FCSTD DOCUMENT  (FreeCAD 0.16R6700 (Git))
Label: fuselage_simple2
License: All rights reserved
LicenseURL: http://en.wikipedia.org/wiki/All_rights_reserved
objects: Sketcher::SketchObject×101, PartDesign::Pocket×53, PartDesign::Fillet×46, PartDesign::Pad×29, Part::Extrusion×14, Part::Mirroring×8, Part::MultiFuse×6, PartDesign::Groove×5, Part::FeaturePython×5, Part::Cut×3, Mesh::Feature×2, Part::Part2DObjectPython×2, Part::MultiCommon×2, Part::Sweep×1, Part::Cylinder×1
note: 363 computed .brp shape members not serialized (recipe doc carries the construction recipe); baked Part::Feature solids carry a one-line shape summary decoded from their .brp

FEATURE [Mesh::Feature] cam_holder  label="cam+holder"
  Placement = pos=(-6.5,10.5,19) rot=(1,0,0;0.785398rad)
FEATURE [Sketcher::SketchObject] Sketch
  Placement = pos=(0,3,20) rot=(0.57735,0.57735,0.57735;2.0944rad)
  sketch-geometry (7):
    g0: Circle CenterX=0 CenterY=0 CenterZ=0 NormalX=0 NormalY=0 NormalZ=1 Radius=1.7
    g1: LineSegment StartX=-3.5 StartY=3 StartZ=0 EndX=1 EndY=3 EndZ=0
    g2: LineSegment StartX=3 StartY=1 StartZ=0 EndX=3 EndY=-1 EndZ=0
    g3: LineSegment StartX=1 StartY=-3 StartZ=0 EndX=-3.5 EndY=-3 EndZ=0
    g4: LineSegment StartX=-3.5 StartY=-3 StartZ=0 EndX=-3.5 EndY=3 EndZ=0
    g5: ArcOfCircle CenterX=1 CenterY=1 CenterZ=0 NormalX=0 NormalY=0 NormalZ=1 Radius=2 StartAngle=0 EndAngle=1.5708
    g6: ArcOfCircle CenterX=1 CenterY=-1 CenterZ=0 NormalX=0 NormalY=0 NormalZ=1 Radius=2 StartAngle=4.71239 EndAngle=6.28319
  constraints (18):
    c: Coincident(g0,g-1)
    c: Radius(g0) = 1.7
    c: Coincident(g3,g4)
    c: Coincident(g4,g1)
    c: Horizontal(g1)
    c: Horizontal(g3)
    c: Vertical(g2)
    c: Vertical(g4)
    c: Tangent(g1,g5) = 1.5708
    c: Tangent(g2,g5) = 1.5708
    c: Tangent(g2,g6) = 1.5708
    c: Tangent(g3,g6) = 1.5708
    c: Radius(g5) = 2
    c: Radius(g6) = 2
    c: Symmetric(g1,g3,g-1)
    c: DistanceX(g-1,g2) = 3
    c: DistanceY(g-1,g1) = 3
    c: DistanceX(g1,g-1) = 3.5
FEATURE [PartDesign::Pad] Pad
  Length = 3
  Length2 = 100
  Midplane = true
  Placement = pos=(0,3,20) rot=(0.57735,0.57735,0.57735;2.0944rad)
  Sketch = -> Sketch
  Type = 0
FEATURE [Sketcher::SketchObject] Sketch001
  Placement = pos=(0,0,0) rot=(1,0,0;1.5708rad)
  sketch-geometry (16):
    g0: LineSegment StartX=-10 StartY=40 StartZ=0 EndX=10 EndY=40 EndZ=0
    g1: LineSegment StartX=30 StartY=20 StartZ=0 EndX=30 EndY=-20 EndZ=0
    g2: LineSegment StartX=10 StartY=-40 StartZ=0 EndX=-10 EndY=-40 EndZ=0
    g3: LineSegment StartX=-30 StartY=-20 StartZ=0 EndX=-30 EndY=20 EndZ=0
    g4: ArcOfCircle CenterX=-10 CenterY=20 CenterZ=0 NormalX=0 NormalY=0 NormalZ=1 Radius=20 StartAngle=1.5708 EndAngle=3.14159
    g5: ArcOfCircle CenterX=10 CenterY=20 CenterZ=0 NormalX=0 NormalY=0 NormalZ=1 Radius=20 StartAngle=0 EndAngle=1.5708
    g6: ArcOfCircle CenterX=10 CenterY=-20 CenterZ=0 NormalX=0 NormalY=0 NormalZ=1 Radius=20 StartAngle=4.71239 EndAngle=6.28319
    g7: ArcOfCircle CenterX=-10 CenterY=-20 CenterZ=0 NormalX=0 NormalY=0 NormalZ=1 Radius=20 StartAngle=3.14159 EndAngle=4.71239
    g8: LineSegment StartX=-10 StartY=37 StartZ=0 EndX=10 EndY=37 EndZ=0
    g9: LineSegment StartX=27 StartY=20 StartZ=0 EndX=27 EndY=-20 EndZ=0
    g10: LineSegment StartX=10 StartY=-37 StartZ=0 EndX=-10 EndY=-37 EndZ=0
    g11: LineSegment StartX=-27 StartY=-20 StartZ=0 EndX=-27 EndY=20 EndZ=0
    g12: ArcOfCircle CenterX=-10 CenterY=20 CenterZ=0 NormalX=0 NormalY=0 NormalZ=1 Radius=17 StartAngle=1.5708 EndAngle=3.14159
    g13: ArcOfCircle CenterX=10 CenterY=20 CenterZ=0 NormalX=0 NormalY=0 NormalZ=1 Radius=17 StartAngle=0 EndAngle=1.5708
    g14: ArcOfCircle CenterX=10 CenterY=-20 CenterZ=0 NormalX=0 NormalY=0 NormalZ=1 Radius=17 StartAngle=4.71239 EndAngle=6.28319
    g15: ArcOfCircle CenterX=-10 CenterY=-20 CenterZ=0 NormalX=0 NormalY=0 NormalZ=1 Radius=17 StartAngle=3.14159 EndAngle=4.71239
  constraints (38):
    c: Horizontal(g0)
    c: Horizontal(g2)
    c: Vertical(g1)
    c: Tangent(g0,g4) = 1.5708
    c: Tangent(g3,g4) = 1.5708
    c: Tangent(g0,g5) = 1.5708
    c: Tangent(g1,g5) = 1.5708
    c: Tangent(g1,g6) = 1.5708
    c: Tangent(g2,g6) = 1.5708
    c: Tangent(g2,g7) = 1.5708
    c: Tangent(g3,g7) = 1.5708
    c: Radius(g4) = 20
    c: DistanceX(g3,g1) = 60
    c: Equal(g4,g5)
    c: Equal(g6,g4)
    c: Equal(g7,g4)
    c: DistanceY(g2,g0) = 80
    c: Horizontal(g8)
    c: Horizontal(g10)
    c: Vertical(g9)
    c: Tangent(g8,g12) = 1.5708
    c: Tangent(g11,g12) = 1.5708
    c: Tangent(g8,g13) = 1.5708
    c: Tangent(g9,g13) = 1.5708
    c: Tangent(g9,g14) = 1.5708
    c: Tangent(g10,g14) = 1.5708
    c: Tangent(g10,g15) = 1.5708
    c: Tangent(g11,g15) = 1.5708
    c: DistanceX(g11,g9) = 54
    c: DistanceY(g10,g8) = 74
    c: Radius(g12) = 17
    c: Equal(g12,g13)
    c: Equal(g15,g12)
    c: Equal(g14,g12)
    c: Symmetric(g1,g3,g-2)
    c: Symmetric(g11,g9,g-2)
    c: Symmetric(g8,g10,g-1)
    c: Symmetric(g0,g2,g-1)
FEATURE [Part::Extrusion] Extrude
  Base = -> Sketch001
  Dir = (0,120,0)
  Solid = true
FEATURE [Sketcher::SketchObject] Sketch002
  ExternalGeometry = -> [Extrude]
  Placement = pos=(0,0,0) rot=(1,0,0;1.5708rad)
  Support = -> Extrude [Face17]
  sketch-geometry (8):
    g0: ArcOfCircle CenterX=-10 CenterY=20 CenterZ=0 NormalX=0 NormalY=0 NormalZ=1 Radius=20 StartAngle=1.5708 EndAngle=3.14159
    g1: ArcOfCircle CenterX=10 CenterY=20 CenterZ=0 NormalX=0 NormalY=0 NormalZ=1 Radius=20 StartAngle=1.97396e-06 EndAngle=1.5708
    g2: ArcOfCircle CenterX=10 CenterY=-20 CenterZ=0 NormalX=0 NormalY=0 NormalZ=1 Radius=20 StartAngle=4.71239 EndAngle=6.28319
    g3: ArcOfCircle CenterX=-10 CenterY=-20 CenterZ=0 NormalX=0 NormalY=0 NormalZ=1 Radius=20 StartAngle=3.14159 EndAngle=4.71239
    g4: LineSegment StartX=-30 StartY=20 StartZ=0 EndX=-30 EndY=-20 EndZ=0
    g5: LineSegment StartX=-10 StartY=40 StartZ=0 EndX=10 EndY=40 EndZ=0
    g6: LineSegment StartX=30 StartY=20 StartZ=0 EndX=30 EndY=-20 EndZ=0
    g7: LineSegment StartX=10 StartY=-40 StartZ=0 EndX=-10 EndY=-40 EndZ=0
  constraints (20):
    c: Coincident(g0,g-3)
    c: Coincident(g1,g-4)
    c: Coincident(g3,g-6)
    c: Coincident(g2,g-5)
    c: Coincident(g2,g-5)
    c: Coincident(g2,g7)
    c: Coincident(g3,g7)
    c: Coincident(g3,g-6)
    c: Coincident(g3,g4)
    c: Coincident(g0,g4)
    c: Coincident(g0,g-3)
    c: Coincident(g5,g0)
    c: Coincident(g1,g5)
    c: Coincident(g1,g-4)
    c: Coincident(g1,g6)
    c: Coincident(g6,g2)
    c: Vertical(g6)
    c: Horizontal(g7)
    c: Vertical(g4)
    c: Horizontal(g5)
FEATURE [PartDesign::Pad] Pad001
  Length = 3
  Length2 = 100
  Sketch = -> Sketch002
  Type = 0
FEATURE [Part::Part2DObjectPython] Clone2D  label="Clone of Sketch002 (2D)"  # Draft 2D object (typed FeaturePython)
  Objects = -> [Sketch002]
  Placement = pos=(0,120,0) rot=(1,0,0;1.5708rad)
  Scale = (1,1,1)
FEATURE [PartDesign::Pad] Pad002
  Length = 3
  Length2 = 100
  Placement = pos=(0,120,0) rot=(1,0,0;1.5708rad)
  Reversed = true
  Sketch = -> Clone2D
  Type = 0
FEATURE [PartDesign::Fillet] Fillet
  Base = -> Pad001 [Edge49,Edge47,Edge46,Edge43,Edge42,Edge39,Edge38,Edge35]
  Radius = 17
FEATURE [PartDesign::Fillet] Fillet001
  Base = -> Fillet [Edge70,Edge68,Edge65,Edge79,Edge78,Edge75,Edge74,Edge71]
  Radius = 20
FEATURE [Sketcher::SketchObject] Sketch003
  Placement = pos=(0,-3,0) rot=(1,0,0;1.5708rad)
  Support = -> Fillet001 [Face9]
  sketch-geometry (4):
    g0: ArcOfCircle CenterX=0 CenterY=35 CenterZ=0 NormalX=0 NormalY=0 NormalZ=1 Radius=10 StartAngle=3.70592 EndAngle=5.71885
    g1: LineSegment StartX=-8.44947 StartY=29.6515 StartZ=0 EndX=-15 EndY=40 EndZ=0
    g2: LineSegment StartX=8.44947 StartY=29.6515 StartZ=0 EndX=15 EndY=40 EndZ=0
    g3: LineSegment StartX=-15 StartY=40 StartZ=0 EndX=15 EndY=40 EndZ=0
  constraints (13):
    c: PointOnObject(g0,g-2)
    c: Coincident(g1,g0)
    c: Coincident(g2,g0)
    c: Tangent(g1,g0)
    c: Tangent(g0,g2)
    c: Coincident(g3,g1)
    c: Coincident(g3,g2)
    c: Horizontal(g3)
    c: Symmetric(g2,g1,g-2)
    c: DistanceY(g-1,g2) = 40
    c: DistanceY(g-1,g0) = 35
    c: Radius(g0) = 10
    c: Distance(g3) = 30
FEATURE [PartDesign::Pocket] Pocket
  Length = 10
  Sketch = -> Sketch003
  Type = 0
FEATURE [Sketcher::SketchObject] Sketch004
  ExternalGeometry = -> [Pocket]
  Placement = pos=(0,7,0) rot=(1,0,0;1.5708rad)
  Support = -> Pocket [Face24]
  sketch-geometry (4):
    g0: LineSegment StartX=11.0184 StartY=33.71 StartZ=0 EndX=15.8321 EndY=41.3145 EndZ=0
    g1: LineSegment StartX=15.8321 StartY=41.3145 StartZ=0 EndX=0 EndY=41.3145 EndZ=0
    g2: LineSegment StartX=0 StartY=41.3145 StartZ=0 EndX=0 EndY=33.71 EndZ=0
    g3: LineSegment StartX=11.0184 StartY=33.71 StartZ=0 EndX=0 EndY=33.71 EndZ=0
  constraints (11):
    c: Coincident(g0,g-3)
    c: PointOnObject(g-3,g0)
    c: Distance(g0) = 9
    c: Coincident(g0,g1)
    c: PointOnObject(g1,g-2)
    c: Horizontal(g1)
    c: Horizontal(g3)
    c: Coincident(g2,g3)
    c: Coincident(g1,g2)
    c: Vertical(g2)
    c: Coincident(g0,g3)
FEATURE [PartDesign::Groove] Groove
  Angle = 360
  Axis = (0,0,1)
  Base = (0,7,0)
  ReferenceAxis = -> Sketch004 [V_Axis]
  Sketch = -> Sketch004
FEATURE [Sketcher::SketchObject] Sketch009
  Placement = pos=(15,32.5,-9) rot=(0,0.707107,-0.707107;3.14159rad)
  sketch-geometry (8):
    g0: LineSegment StartX=0 StartY=0 StartZ=0 EndX=20 EndY=0 EndZ=0
    g1: LineSegment StartX=20 StartY=0 StartZ=0 EndX=20 EndY=-26 EndZ=0
    g2: LineSegment StartX=10 StartY=-26 StartZ=0 EndX=0 EndY=-26 EndZ=0
    g3: LineSegment StartX=0 StartY=-26 StartZ=0 EndX=0 EndY=0 EndZ=0
    g4: LineSegment StartX=20 StartY=-26 StartZ=0 EndX=20 EndY=-41 EndZ=0
    g5: LineSegment StartX=20 StartY=-41 StartZ=0 EndX=10 EndY=-41 EndZ=0
    g6: LineSegment StartX=10 StartY=-41 StartZ=0 EndX=10 EndY=-26 EndZ=0
    g7: LineSegment [constr] StartX=10 StartY=-26 StartZ=0 EndX=20 EndY=-26 EndZ=0
  constraints (22):
    c: Coincident(g0,g1)
    c: Coincident(g2,g3)
    c: Coincident(g3,g0)
    c: Horizontal(g0)
    c: Horizontal(g2)
    c: Vertical(g1)
    c: Vertical(g3)
    c: Distance(g0) = 20
    c: DistanceY(g1,g1) = 26
    c: Coincident(g4,g1)
    c: Vertical(g4)
    c: DistanceY(g4,g4) = 15
    c: Coincident(g5,g4)
    c: Horizontal(g5)
    c: Distance(g5) = 10
    c: Coincident(g6,g5)
    c: Vertical(g6)
    c: Coincident(g2,g6)
    c: Coincident(g7,g2)
    c: Coincident(g7,g1)
    c: Horizontal(g7)
    c: Coincident(g0,g-1)
FEATURE [PartDesign::Pad] Pad003  label="video_tx_base"
  Length = 6
  Length2 = 100
  Placement = pos=(15,32.5,-9) rot=(0,0.707107,-0.707107;3.14159rad)
  Sketch = -> Sketch009
  Type = 0
FEATURE [Sketcher::SketchObject] Sketch010
  ExternalGeometry = -> [Pad003]
  Placement = pos=(15,26.5,-9) rot=(0,0.707107,-0.707107;3.14159rad)
  Support = -> Pad003 [Face9]
  sketch-geometry (8):
    g0: LineSegment StartX=0.5 StartY=-3 StartZ=0 EndX=19.5 EndY=-3 EndZ=0
    g1: LineSegment StartX=19.5 StartY=-3 StartZ=0 EndX=19.5 EndY=-23 EndZ=0
    g2: LineSegment StartX=19.5 StartY=-23 StartZ=0 EndX=0.5 EndY=-23 EndZ=0
    g3: LineSegment StartX=0.5 StartY=-23 StartZ=0 EndX=0.5 EndY=-3 EndZ=0
    g4: LineSegment StartX=10 StartY=-26 StartZ=0 EndX=20 EndY=-26 EndZ=0
    g5: LineSegment StartX=20 StartY=-26 StartZ=0 EndX=20 EndY=-41 EndZ=0
    g6: LineSegment StartX=20 StartY=-41 StartZ=0 EndX=10 EndY=-41 EndZ=0
    g7: LineSegment StartX=10 StartY=-26 StartZ=0 EndX=10 EndY=-41 EndZ=0
  constraints (21):
    c: Coincident(g0,g1)
    c: Coincident(g1,g2)
    c: Coincident(g2,g3)
    c: Coincident(g3,g0)
    c: Horizontal(g0)
    c: Horizontal(g2)
    c: Vertical(g1)
    c: Vertical(g3)
    c: Coincident(g4,g5)
    c: Coincident(g5,g6)
    c: Horizontal(g4)
    c: Horizontal(g6)
    c: Vertical(g5)
    c: Coincident(g4,g-3)
    c: Coincident(g5,g-4)
    c: Distance(g2) = 19
    c: Distance(g1) = 20
    c: DistanceX(g-1,g0) = 0.5
    c: DistanceY(g0,g-1) = 3
    c: Coincident(g7,g4)
    c: Coincident(g7,g6)
FEATURE [PartDesign::Pad] Pad004  label="video_tx"
  Length = 3
  Length2 = 100
  Placement = pos=(15,32.5,-9) rot=(0,0.707107,-0.707107;3.14159rad)
  Sketch = -> Sketch010
  Type = 0
FEATURE [Sketcher::SketchObject] Sketch011
  Placement = pos=(0,0,40) rot=(0,0,1;0rad)
  Support = -> Groove [Face10]
  sketch-geometry (1):
    g0: Circle CenterX=0 CenterY=28 CenterZ=0 NormalX=0 NormalY=0 NormalZ=1 Radius=5
  constraints (3):
    c: PointOnObject(g0,g-2)
    c: Radius(g0) = 5
    c: DistanceY(g-1,g0) = 28
FEATURE [PartDesign::Pocket] Pocket001
  Length = 5
  Sketch = -> Sketch011
  Type = 0
FEATURE [Sketcher::SketchObject] Sketch012
  ExternalGeometry = -> [Groove]
  Placement = pos=(27,0,0) rot=(0.57735,-0.57735,-0.57735;2.0944rad)
  Support = -> Groove [Face18]
  sketch-geometry (4):
    g0: LineSegment StartX=-29 StartY=16.5 StartZ=0 EndX=-25 EndY=16.5 EndZ=0
    g1: LineSegment StartX=-25 StartY=16.5 StartZ=0 EndX=-25 EndY=-11.5 EndZ=0
    g2: LineSegment StartX=-25 StartY=-11.5 StartZ=0 EndX=-29 EndY=-11.5 EndZ=0
    g3: LineSegment StartX=-29 StartY=-11.5 StartZ=0 EndX=-29 EndY=16.5 EndZ=0
  constraints (12):
    c: Coincident(g0,g1)
    c: Coincident(g1,g2)
    c: Coincident(g2,g3)
    c: Coincident(g3,g0)
    c: Horizontal(g0)
    c: Horizontal(g2)
    c: Vertical(g1)
    c: Vertical(g3)
    c: Distance(g2) = 4
    c: Distance(g1) = 28
    c: DistanceY(g0,g-3) = 3.5
    c: DistanceX(g0,g-3) = 8
FEATURE [PartDesign::Pad] Pad005
  Length = 55
  Length2 = 100
  Sketch = -> Sketch012
  Type = 0
FEATURE [Sketcher::SketchObject] Sketch013
  Placement = pos=(0,25,0) rot=(1,0,0;1.5708rad)
  Support = -> Pad005 [Face32]
  sketch-geometry (4):
    g0: LineSegment StartX=-4.75 StartY=14.25 StartZ=0 EndX=14.75 EndY=14.25 EndZ=0
    g1: LineSegment StartX=14.75 StartY=14.25 StartZ=0 EndX=14.75 EndY=-6.25 EndZ=0
    g2: LineSegment StartX=14.75 StartY=-6.25 StartZ=0 EndX=-4.75 EndY=-6.25 EndZ=0
    g3: LineSegment StartX=-4.75 StartY=-6.25 StartZ=0 EndX=-4.75 EndY=14.25 EndZ=0
  constraints (12):
    c: Coincident(g0,g1)
    c: Coincident(g1,g2)
    c: Coincident(g2,g3)
    c: Coincident(g3,g0)
    c: Horizontal(g0)
    c: Horizontal(g2)
    c: Vertical(g1)
    c: Vertical(g3)
    c: Distance(g0) = 19.5
    c: Distance(g1) = 20.5
    c: DistanceY(g2,g-1) = 6.25
    c: DistanceX(g2,g-1) = 4.75
FEATURE [PartDesign::Pocket] Pocket002
  Length = 5
  Sketch = -> Sketch013
  Type = 0
FEATURE [Sketcher::SketchObject] Sketch014
  Placement = pos=(0,29,0) rot=(0,0.707107,0.707107;3.14159rad)
  Support = -> Pocket002 [Face30]
  sketch-geometry (4):
    g0: LineSegment StartX=-15.25 StartY=17.25 StartZ=0 EndX=5.25 EndY=17.25 EndZ=0
    g1: LineSegment StartX=5.25 StartY=17.25 StartZ=0 EndX=5.25 EndY=-9.25 EndZ=0
    g2: LineSegment StartX=5.25 StartY=-9.25 StartZ=0 EndX=-15.25 EndY=-9.25 EndZ=0
    g3: LineSegment StartX=-15.25 StartY=-9.25 StartZ=0 EndX=-15.25 EndY=17.25 EndZ=0
  constraints (12):
    c: Coincident(g0,g1)
    c: Coincident(g1,g2)
    c: Coincident(g2,g3)
    c: Coincident(g3,g0)
    c: Horizontal(g0)
    c: Horizontal(g2)
    c: Vertical(g1)
    c: Vertical(g3)
    c: Distance(g2) = 20.5
    c: DistanceY(g3,g3) = 26.5
    c: DistanceY(g1,g-1) = 9.25
    c: DistanceX(g-1,g1) = 5.25
FEATURE [PartDesign::Pocket] Pocket003
  Length = 2
  Sketch = -> Sketch014
  Type = 0
FEATURE [Sketcher::SketchObject] Sketch015
  Placement = pos=(0,0,40) rot=(0,0,1;0rad)
  Support = -> Pocket003 [Face10]
  sketch-geometry (1):
    g0: Circle CenterX=0 CenterY=28 CenterZ=0 NormalX=0 NormalY=0 NormalZ=1 Radius=5
  constraints (3):
    c: Radius(g0) = 5
    c: DistanceY(g-1,g0) = 28
    c: PointOnObject(g0,g-2)
FEATURE [PartDesign::Pocket] Pocket004
  Length = 5
  Sketch = -> Sketch015
  Type = 0
FEATURE [Sketcher::SketchObject] Sketch016
  Placement = pos=(-17.5,40,5) rot=(0,0,1;0rad)
  sketch-geometry (4):
    g0: LineSegment StartX=0 StartY=80 StartZ=0 EndX=35 EndY=80 EndZ=0
    g1: LineSegment StartX=35 StartY=80 StartZ=0 EndX=35 EndY=0 EndZ=0
    g2: LineSegment StartX=35 StartY=0 StartZ=0 EndX=0 EndY=0 EndZ=0
    g3: LineSegment StartX=0 StartY=0 StartZ=0 EndX=0 EndY=80 EndZ=0
  constraints (11):
    c: Coincident(g0,g1)
    c: Coincident(g1,g2)
    c: Coincident(g2,g3)
    c: Coincident(g3,g0)
    c: Horizontal(g0)
    c: Horizontal(g2)
    c: Vertical(g1)
    c: Vertical(g3)
    c: Coincident(g2,g-1)
    c: Distance(g3) = 80
    c: Distance(g2) = 35
FEATURE [PartDesign::Pad] Pad006  label="battery"
  Length = 27
  Length2 = 100
  Placement = pos=(-17.5,40,5) rot=(0,0,1;0rad)
  Sketch = -> Sketch016
  Type = 0
FEATURE [Sketcher::SketchObject] Sketch017
  Placement = pos=(27,0,0) rot=(0.57735,-0.57735,-0.57735;2.0944rad)
  Support = -> Pocket004 [Face18]
  sketch-geometry (4):
    g0: LineSegment StartX=-39 StartY=30 StartZ=0 EndX=-34 EndY=30 EndZ=0
    g1: LineSegment StartX=-34 StartY=30 StartZ=0 EndX=-34 EndY=-10 EndZ=0
    g2: LineSegment StartX=-34 StartY=-10 StartZ=0 EndX=-39 EndY=-10 EndZ=0
    g3: LineSegment StartX=-39 StartY=-10 StartZ=0 EndX=-39 EndY=30 EndZ=0
  constraints (12):
    c: Coincident(g0,g1)
    c: Coincident(g1,g2)
    c: Coincident(g2,g3)
    c: Coincident(g3,g0)
    c: Horizontal(g0)
    c: Horizontal(g2)
    c: Vertical(g1)
    c: Vertical(g3)
    c: Distance(g2) = 5
    c: DistanceX(g0,g-1) = 34
    c: DistanceY(g1,g1) = 40
    c: DistanceY(g1,g-1) = 10
FEATURE [PartDesign::Pad] Pad007
  Length = 54
  Length2 = 100
  Sketch = -> Sketch017
  Type = 0
FEATURE [PartDesign::Fillet] Fillet002
  Base = -> Pad007 [Edge73,Edge79,Edge54,Edge64]
  Radius = 4
FEATURE [Sketcher::SketchObject] Sketch018
  Placement = pos=(0,39,0) rot=(0,0.707107,0.707107;3.14159rad)
  Support = -> Fillet002 [Face17]
  sketch-geometry (4):
    g0: LineSegment StartX=-27.5 StartY=4 StartZ=0 EndX=27.5 EndY=4 EndZ=0
    g1: LineSegment StartX=27.5 StartY=4 StartZ=0 EndX=27.5 EndY=0 EndZ=0
    g2: LineSegment StartX=27.5 StartY=0 StartZ=0 EndX=-27.5 EndY=0 EndZ=0
    g3: LineSegment StartX=-27.5 StartY=0 StartZ=0 EndX=-27.5 EndY=4 EndZ=0
  constraints (12):
    c: Coincident(g0,g1)
    c: Coincident(g1,g2)
    c: Coincident(g2,g3)
    c: Coincident(g3,g0)
    c: Horizontal(g0)
    c: Horizontal(g2)
    c: Vertical(g1)
    c: Vertical(g3)
    c: DistanceY(g3,g3) = 4
    c: PointOnObject(g1,g-1)
    c: Distance(g2) = 55
    c: Symmetric(g1,g2,g-2)
FEATURE [PartDesign::Pad] Pad008
  Length = 80
  Length2 = 100
  Sketch = -> Sketch018
  Type = 0
FEATURE [PartDesign::Fillet] Fillet003
  Base = -> Pad008 [Edge17,Edge74]
  Radius = 5
FEATURE [PartDesign::Fillet] Fillet004
  Base = -> Fillet003 [Edge41,Edge8]
  Radius = 2
FEATURE [Sketcher::SketchObject] Sketch019
  Placement = pos=(0,0,0) rot=(1,0,0;3.14159rad)
  Support = -> Fillet004 [Face27]
  sketch-geometry (4):
    g0: LineSegment StartX=-18 StartY=-119 StartZ=0 EndX=-26 EndY=-119 EndZ=0
    g1: LineSegment StartX=-26 StartY=-119 StartZ=0 EndX=-26 EndY=-111 EndZ=0
    g2: LineSegment StartX=-18 StartY=-119 StartZ=0 EndX=-18 EndY=-111 EndZ=0
    g3: ArcOfCircle CenterX=-22 CenterY=-111 CenterZ=0 NormalX=0 NormalY=0 NormalZ=1 Radius=4 StartAngle=6.70092e-06 EndAngle=3.14159
  constraints (13):
    c: Horizontal(g0)
    c: Coincident(g1,g0)
    c: Vertical(g1)
    c: Coincident(g2,g0)
    c: Vertical(g2)
    c: Coincident(g3,g2)
    c: Coincident(g3,g1)
    c: Tangent(g3,g1)
    c: Distance(g0) = 8
    c: Distance(g2) = 8
    c: DistanceY(g0,g-1) = 119
    c: DistanceX(g0,g-1) = 18
    c: Tangent(g3,g2)
FEATURE [PartDesign::Pocket] Pocket005
  Length = 10
  Midplane = true
  Sketch = -> Sketch019
  Type = 0
FEATURE [Mesh::Feature] cc3d_model  label="cc3d-model"
  Placement = pos=(0,67,-10) rot=(0,0,-1;1.5708rad)
FEATURE [Sketcher::SketchObject] Sketch020
  ExternalGeometry = -> [Pocket005]
  Placement = pos=(0,120,0) rot=(0,0.707107,0.707107;3.14159rad)
  Support = -> Pocket005 [Face6]
  sketch-geometry (8):
    g0: ArcOfCircle CenterX=-10 CenterY=20 CenterZ=0 NormalX=0 NormalY=0 NormalZ=1 Radius=20 StartAngle=1.5708 EndAngle=3.1416
    g1: ArcOfCircle CenterX=10 CenterY=20 CenterZ=0 NormalX=0 NormalY=0 NormalZ=1 Radius=20 StartAngle=4.90195e-07 EndAngle=1.5708
    g2: ArcOfCircle CenterX=10 CenterY=-20 CenterZ=0 NormalX=0 NormalY=0 NormalZ=1 Radius=20 StartAngle=4.71239 EndAngle=6.28319
    g3: ArcOfCircle CenterX=-10 CenterY=-20 CenterZ=0 NormalX=0 NormalY=0 NormalZ=1 Radius=20 StartAngle=3.14159 EndAngle=4.71239
    g4: LineSegment StartX=-30 StartY=19.9999 StartZ=0 EndX=-30 EndY=-20 EndZ=0
    g5: LineSegment StartX=30 StartY=20 StartZ=0 EndX=30 EndY=-20 EndZ=0
    g6: LineSegment StartX=-10 StartY=40 StartZ=0 EndX=10 EndY=40 EndZ=0
    g7: LineSegment StartX=-10 StartY=-40 StartZ=0 EndX=10 EndY=-40 EndZ=0
  constraints (20):
    c: Coincident(g0,g-6)
    c: Coincident(g0,g-6)
    c: Coincident(g1,g-3)
    c: Coincident(g1,g-3)
    c: Coincident(g2,g-4)
    c: Coincident(g2,g-4)
    c: Coincident(g3,g-5)
    c: Coincident(g3,g-5)
    c: Coincident(g4,g0)
    c: Coincident(g4,g3)
    c: Vertical(g4)
    c: Coincident(g5,g1)
    c: Coincident(g5,g2)
    c: Vertical(g5)
    c: Coincident(g6,g0)
    c: Coincident(g6,g1)
    c: Coincident(g7,g3)
    c: Coincident(g7,g2)
    c: Horizontal(g7)
    c: PointOnObject(g-5,g4)
FEATURE [Part::Extrusion] Extrude004
  Base = -> Sketch020
  Dir = (0,5,0)
  Solid = true
FEATURE [PartDesign::Fillet] Fillet005  label="rear"
  Base = -> Extrude004 [Edge4,Edge7,Edge10,Edge13,Edge16,Edge19,Edge22,Edge24]
  Radius = 4
FEATURE [Sketcher::SketchObject] Sketch021
  Placement = pos=(-30,0,1e-12) rot=(0.57735,-0.57735,-0.57735;2.0944rad)
  Support = -> Pocket005 [Face26]
  sketch-geometry (17):
    g0: LineSegment StartX=-60 StartY=15 StartZ=0 EndX=-40 EndY=15 EndZ=0
    g1: LineSegment StartX=-40 StartY=15 StartZ=0 EndX=-40 EndY=-15 EndZ=0
    g2: LineSegment StartX=-40 StartY=-15 StartZ=0 EndX=-60 EndY=-15 EndZ=0
    g3: LineSegment StartX=-60 StartY=-15 StartZ=0 EndX=-60 EndY=15 EndZ=0
    g4: Circle [constr] CenterX=-56.5 CenterY=11.5 CenterZ=0 NormalX=0 NormalY=0 NormalZ=1 Radius=3.5
    g5: Circle CenterX=-56.5 CenterY=11.5 CenterZ=0 NormalX=0 NormalY=0 NormalZ=1 Radius=1.7
    g6: GeomPoint [constr] X=-60 Y=11.5 Z=0
    g7: GeomPoint [constr] X=-56.5 Y=15 Z=0
    g8: Circle CenterX=-56.5 CenterY=-11.5 CenterZ=0 NormalX=0 NormalY=0 NormalZ=1 Radius=1.7
    g9: Circle [constr] CenterX=-56.5 CenterY=-11.5 CenterZ=0 NormalX=0 NormalY=0 NormalZ=1 Radius=3.5
    g10: Circle CenterX=-43.5 CenterY=11.5 CenterZ=0 NormalX=0 NormalY=0 NormalZ=1 Radius=1.7
    g11: Circle [constr] CenterX=-43.5 CenterY=11.5 CenterZ=0 NormalX=0 NormalY=0 NormalZ=1 Radius=3.5
    g12: LineSegment [constr] StartX=-56.5 StartY=11.5 StartZ=0 EndX=-43.5 EndY=11.5 EndZ=0
    g13: LineSegment [constr] StartX=-43.5 StartY=11.5 StartZ=0 EndX=-43.5 EndY=-11.5 EndZ=0
    g14: LineSegment [constr] StartX=-56.5 StartY=-11.5 StartZ=0 EndX=-43.5 EndY=-11.5 EndZ=0
    g15: Circle [constr] CenterX=-43.5 CenterY=-11.5 CenterZ=0 NormalX=0 NormalY=0 NormalZ=1 Radius=3.5
    g16: Circle CenterX=-43.5 CenterY=-11.5 CenterZ=0 NormalX=0 NormalY=0 NormalZ=1 Radius=1.7
  constraints (43):
    c: Coincident(g0,g1)
    c: Coincident(g1,g2)
    c: Coincident(g2,g3)
    c: Coincident(g3,g0)
    c: Horizontal(g0)
    c: Horizontal(g2)
    c: Vertical(g1)
    c: Vertical(g3)
    c: Radius(g4) = 3.5
    c: Coincident(g5,g4)
    c: Radius(g5) = 1.7
    c: PointOnObject(g6,g3)
    c: PointOnObject(g7,g0)
    c: PointOnObject(g7,g4)
    c: PointOnObject(g6,g4)
    c: Tangent(g4,g0)
    c: Tangent(g4,g3)
    c: Equal(g4,g9) = 3.5
    c: Coincident(g8,g9)
    c: Equal(g5,g8) = 1.7
    c: Tangent(g9,g3)
    c: Tangent(g9,g2)
    c: Distance(g3) = 30
    c: Equal(g4,g11) = 3.5
    c: Coincident(g10,g11)
    c: Equal(g5,g10) = 1.7
    c: Tangent(g11,g1)
    c: Coincident(g12,g4)
    c: Coincident(g12,g10)
    c: Horizontal(g12)
    c: Coincident(g13,g10)
    c: Vertical(g13)
    c: Coincident(g14,g8)
    c: Coincident(g14,g13)
    c: Horizontal(g14)
    c: Coincident(g16,g15)
    c: Coincident(g12,g13)
    c: Equal(g15,g4)
    c: Equal(g16,g5)
    c: Coincident(g13,g15)
    c: Distance(g0) = 20
    c: DistanceX(g0,g-1) = 40
    c: DistanceY(g-1,g0) = 15
FEATURE [Part::Extrusion] Extrude005  label="arm base"
  Base = -> Sketch021
  Dir = (-5,0,0)
  Solid = true
FEATURE [Sketcher::SketchObject] Sketch022
  Placement = pos=(0,0,0) rot=(1,0,0;1.5708rad)
  sketch-geometry (16):
    g0: LineSegment StartX=-10 StartY=40 StartZ=0 EndX=10 EndY=40 EndZ=0
    g1: LineSegment StartX=30 StartY=20 StartZ=0 EndX=30 EndY=-20 EndZ=0
    g2: LineSegment StartX=10 StartY=-40 StartZ=0 EndX=-10 EndY=-40 EndZ=0
    g3: LineSegment StartX=-30 StartY=-20 StartZ=0 EndX=-30 EndY=20 EndZ=0
    g4: ArcOfCircle CenterX=-10 CenterY=20 CenterZ=0 NormalX=0 NormalY=0 NormalZ=1 Radius=20 StartAngle=1.5708 EndAngle=3.14159
    g5: ArcOfCircle CenterX=10 CenterY=20 CenterZ=0 NormalX=0 NormalY=0 NormalZ=1 Radius=20 StartAngle=0 EndAngle=1.5708
    g6: ArcOfCircle CenterX=10 CenterY=-20 CenterZ=0 NormalX=0 NormalY=0 NormalZ=1 Radius=20 StartAngle=4.71239 EndAngle=6.28319
    g7: ArcOfCircle CenterX=-10 CenterY=-20 CenterZ=0 NormalX=0 NormalY=0 NormalZ=1 Radius=20 StartAngle=3.14159 EndAngle=4.71239
    g8: LineSegment StartX=-10 StartY=37 StartZ=0 EndX=10 EndY=37 EndZ=0
    g9: LineSegment StartX=27 StartY=20 StartZ=0 EndX=27 EndY=-20 EndZ=0
    g10: LineSegment StartX=10 StartY=-37 StartZ=0 EndX=-10 EndY=-37 EndZ=0
    g11: LineSegment StartX=-27 StartY=-20 StartZ=0 EndX=-27 EndY=20 EndZ=0
    g12: ArcOfCircle CenterX=-10 CenterY=20 CenterZ=0 NormalX=0 NormalY=0 NormalZ=1 Radius=17 StartAngle=1.5708 EndAngle=3.14159
    g13: ArcOfCircle CenterX=10 CenterY=20 CenterZ=0 NormalX=0 NormalY=0 NormalZ=1 Radius=17 StartAngle=0 EndAngle=1.5708
    g14: ArcOfCircle CenterX=10 CenterY=-20 CenterZ=0 NormalX=0 NormalY=0 NormalZ=1 Radius=17 StartAngle=4.71239 EndAngle=6.28319
    g15: ArcOfCircle CenterX=-10 CenterY=-20 CenterZ=0 NormalX=0 NormalY=0 NormalZ=1 Radius=17 StartAngle=3.14159 EndAngle=4.71239
  constraints (38):
    c: Horizontal(g0)
    c: Horizontal(g2)
    c: Vertical(g1)
    c: Tangent(g0,g4) = 1.5708
    c: Tangent(g3,g4) = 1.5708
    c: Tangent(g0,g5) = 1.5708
    c: Tangent(g1,g5) = 1.5708
    c: Tangent(g1,g6) = 1.5708
    c: Tangent(g2,g6) = 1.5708
    c: Tangent(g2,g7) = 1.5708
    c: Tangent(g3,g7) = 1.5708
    c: Radius(g4) = 20
    c: DistanceX(g3,g1) = 60
    c: Equal(g4,g5)
    c: Equal(g6,g4)
    c: Equal(g7,g4)
    c: DistanceY(g2,g0) = 80
    c: Horizontal(g8)
    c: Horizontal(g10)
    c: Vertical(g9)
    c: Tangent(g8,g12) = 1.5708
    c: Tangent(g11,g12) = 1.5708
    c: Tangent(g8,g13) = 1.5708
    c: Tangent(g9,g13) = 1.5708
    c: Tangent(g9,g14) = 1.5708
    c: Tangent(g10,g14) = 1.5708
    c: Tangent(g10,g15) = 1.5708
    c: Tangent(g11,g15) = 1.5708
    c: DistanceX(g11,g9) = 54
    c: DistanceY(g10,g8) = 74
    c: Radius(g12) = 17
    c: Equal(g12,g13)
    c: Equal(g15,g12)
    c: Equal(g14,g12)
    c: Symmetric(g1,g3,g-2)
    c: Symmetric(g11,g9,g-2)
    c: Symmetric(g8,g10,g-1)
    c: Symmetric(g0,g2,g-1)
FEATURE [Part::Extrusion] Extrude006
  Base = -> Sketch022
  Dir = (0,120,0)
  Solid = true
FEATURE [Sketcher::SketchObject] Sketch023
  ExternalGeometry = -> [Extrude006]
  Placement = pos=(0,0,0) rot=(1,0,0;1.5708rad)
  Support = -> Extrude006 [Face17]
  sketch-geometry (8):
    g0: ArcOfCircle CenterX=-10 CenterY=20 CenterZ=0 NormalX=0 NormalY=0 NormalZ=1 Radius=20 StartAngle=1.5708 EndAngle=3.14159
    g1: ArcOfCircle CenterX=10 CenterY=20 CenterZ=0 NormalX=0 NormalY=0 NormalZ=1 Radius=20 StartAngle=1.97396e-06 EndAngle=1.5708
    g2: ArcOfCircle CenterX=10 CenterY=-20 CenterZ=0 NormalX=0 NormalY=0 NormalZ=1 Radius=20 StartAngle=4.71239 EndAngle=6.28319
    g3: ArcOfCircle CenterX=-10 CenterY=-20 CenterZ=0 NormalX=0 NormalY=0 NormalZ=1 Radius=20 StartAngle=3.14159 EndAngle=4.71239
    g4: LineSegment StartX=-30 StartY=20 StartZ=0 EndX=-30 EndY=-20 EndZ=0
    g5: LineSegment StartX=-10 StartY=40 StartZ=0 EndX=10 EndY=40 EndZ=0
    g6: LineSegment StartX=30 StartY=20 StartZ=0 EndX=30 EndY=-20 EndZ=0
    g7: LineSegment StartX=10 StartY=-40 StartZ=0 EndX=-10 EndY=-40 EndZ=0
  constraints (20):
    c: Coincident(g0,g-3)
    c: Coincident(g1,g-4)
    c: Coincident(g3,g-6)
    c: Coincident(g2,g-5)
    c: Coincident(g2,g-5)
    c: Coincident(g2,g7)
    c: Coincident(g3,g7)
    c: Coincident(g3,g-6)
    c: Coincident(g3,g4)
    c: Coincident(g0,g4)
    c: Coincident(g0,g-3)
    c: Coincident(g5,g0)
    c: Coincident(g1,g5)
    c: Coincident(g1,g-4)
    c: Coincident(g1,g6)
    c: Coincident(g6,g2)
    c: Vertical(g6)
    c: Horizontal(g7)
    c: Vertical(g4)
    c: Horizontal(g5)
FEATURE [PartDesign::Pad] Pad009
  Length = 3
  Length2 = 100
  Sketch = -> Sketch023
  Type = 0
FEATURE [PartDesign::Fillet] Fillet006
  Base = -> Pad009 [Edge49,Edge47,Edge46,Edge43,Edge42,Edge39,Edge38,Edge35]
  Radius = 17
FEATURE [PartDesign::Fillet] Fillet007
  Base = -> Fillet006 [Edge70,Edge68,Edge65,Edge79,Edge78,Edge75,Edge74,Edge71]
  Radius = 20
FEATURE [Sketcher::SketchObject] Sketch024
  Placement = pos=(0,-3,0) rot=(1,0,0;1.5708rad)
  Support = -> Fillet007 [Face9]
  sketch-geometry (4):
    g0: ArcOfCircle CenterX=0 CenterY=35 CenterZ=0 NormalX=0 NormalY=0 NormalZ=1 Radius=10 StartAngle=3.70592 EndAngle=5.71885
    g1: LineSegment StartX=-8.44947 StartY=29.6515 StartZ=0 EndX=-15 EndY=40 EndZ=0
    g2: LineSegment StartX=8.44947 StartY=29.6515 StartZ=0 EndX=15 EndY=40 EndZ=0
    g3: LineSegment StartX=-15 StartY=40 StartZ=0 EndX=15 EndY=40 EndZ=0
  constraints (13):
    c: PointOnObject(g0,g-2)
    c: Coincident(g1,g0)
    c: Coincident(g2,g0)
    c: Tangent(g1,g0)
    c: Tangent(g0,g2)
    c: Coincident(g3,g1)
    c: Coincident(g3,g2)
    c: Horizontal(g3)
    c: Symmetric(g2,g1,g-2)
    c: DistanceY(g-1,g2) = 40
    c: DistanceY(g-1,g0) = 35
    c: Radius(g0) = 10
    c: Distance(g3) = 30
FEATURE [PartDesign::Pocket] Pocket006
  Length = 10
  Sketch = -> Sketch024
  Type = 0
FEATURE [Sketcher::SketchObject] Sketch025
  ExternalGeometry = -> [Pocket006]
  Placement = pos=(0,7,0) rot=(1,0,0;1.5708rad)
  Support = -> Pocket006 [Face24]
  sketch-geometry (4):
    g0: LineSegment StartX=11.0184 StartY=33.71 StartZ=0 EndX=15.8321 EndY=41.3145 EndZ=0
    g1: LineSegment StartX=15.8321 StartY=41.3145 StartZ=0 EndX=0 EndY=41.3145 EndZ=0
    g2: LineSegment StartX=0 StartY=41.3145 StartZ=0 EndX=0 EndY=33.71 EndZ=0
    g3: LineSegment StartX=11.0184 StartY=33.71 StartZ=0 EndX=0 EndY=33.71 EndZ=0
  constraints (11):
    c: Coincident(g0,g-3)
    c: PointOnObject(g-3,g0)
    c: Distance(g0) = 9
    c: Coincident(g0,g1)
    c: PointOnObject(g1,g-2)
    c: Horizontal(g1)
    c: Horizontal(g3)
    c: Coincident(g2,g3)
    c: Coincident(g1,g2)
    c: Vertical(g2)
    c: Coincident(g0,g3)
FEATURE [PartDesign::Groove] Groove001
  Angle = 360
  Axis = (0,0,1)
  Base = (0,7,0)
  ReferenceAxis = -> Sketch025 [V_Axis]
  Sketch = -> Sketch025
FEATURE [Sketcher::SketchObject] Sketch026
  ExternalGeometry = -> [Groove001]
  Placement = pos=(27,0,0) rot=(0.57735,-0.57735,-0.57735;2.0944rad)
  Support = -> Groove001 [Face18]
  sketch-geometry (4):
    g0: LineSegment StartX=-29 StartY=16.5 StartZ=0 EndX=-25 EndY=16.5 EndZ=0
    g1: LineSegment StartX=-25 StartY=16.5 StartZ=0 EndX=-25 EndY=-11.5 EndZ=0
    g2: LineSegment StartX=-25 StartY=-11.5 StartZ=0 EndX=-29 EndY=-11.5 EndZ=0
    g3: LineSegment StartX=-29 StartY=-11.5 StartZ=0 EndX=-29 EndY=16.5 EndZ=0
  constraints (12):
    c: Coincident(g0,g1)
    c: Coincident(g1,g2)
    c: Coincident(g2,g3)
    c: Coincident(g3,g0)
    c: Horizontal(g0)
    c: Horizontal(g2)
    c: Vertical(g1)
    c: Vertical(g3)
    c: Distance(g2) = 4
    c: Distance(g1) = 28
    c: DistanceY(g0,g-3) = 3.5
    c: DistanceX(g0,g-3) = 8
FEATURE [PartDesign::Pad] Pad010
  Length = 55
  Length2 = 100
  Sketch = -> Sketch026
  Type = 0
FEATURE [Sketcher::SketchObject] Sketch027
  Placement = pos=(0,25,0) rot=(1,0,0;1.5708rad)
  Support = -> Pad010 [Face32]
  sketch-geometry (4):
    g0: LineSegment StartX=-4.75 StartY=14.25 StartZ=0 EndX=14.75 EndY=14.25 EndZ=0
    g1: LineSegment StartX=14.75 StartY=14.25 StartZ=0 EndX=14.75 EndY=-6.25 EndZ=0
    g2: LineSegment StartX=14.75 StartY=-6.25 StartZ=0 EndX=-4.75 EndY=-6.25 EndZ=0
    g3: LineSegment StartX=-4.75 StartY=-6.25 StartZ=0 EndX=-4.75 EndY=14.25 EndZ=0
  constraints (12):
    c: Coincident(g0,g1)
    c: Coincident(g1,g2)
    c: Coincident(g2,g3)
    c: Coincident(g3,g0)
    c: Horizontal(g0)
    c: Horizontal(g2)
    c: Vertical(g1)
    c: Vertical(g3)
    c: Distance(g0) = 19.5
    c: Distance(g1) = 20.5
    c: DistanceY(g2,g-1) = 6.25
    c: DistanceX(g2,g-1) = 4.75
FEATURE [PartDesign::Pocket] Pocket007
  Length = 5
  Sketch = -> Sketch027
  Type = 0
FEATURE [Sketcher::SketchObject] Sketch028
  Placement = pos=(0,29,0) rot=(0,0.707107,0.707107;3.14159rad)
  Support = -> Pocket007 [Face30]
  sketch-geometry (4):
    g0: LineSegment StartX=-15.25 StartY=17.25 StartZ=0 EndX=5.25 EndY=17.25 EndZ=0
    g1: LineSegment StartX=5.25 StartY=17.25 StartZ=0 EndX=5.25 EndY=-9.25 EndZ=0
    g2: LineSegment StartX=5.25 StartY=-9.25 StartZ=0 EndX=-15.25 EndY=-9.25 EndZ=0
    g3: LineSegment StartX=-15.25 StartY=-9.25 StartZ=0 EndX=-15.25 EndY=17.25 EndZ=0
  constraints (12):
    c: Coincident(g0,g1)
    c: Coincident(g1,g2)
    c: Coincident(g2,g3)
    c: Coincident(g3,g0)
    c: Horizontal(g0)
    c: Horizontal(g2)
    c: Vertical(g1)
    c: Vertical(g3)
    c: Distance(g2) = 20.5
    c: DistanceY(g3,g3) = 26.5
    c: DistanceY(g1,g-1) = 9.25
    c: DistanceX(g-1,g1) = 5.25
FEATURE [PartDesign::Pocket] Pocket008
  Length = 2
  Sketch = -> Sketch028
  Type = 0
FEATURE [Sketcher::SketchObject] Sketch029
  Placement = pos=(0,0,40) rot=(0,0,1;0rad)
  Support = -> Pocket008 [Face10]
  sketch-geometry (1):
    g0: Circle CenterX=0 CenterY=28 CenterZ=0 NormalX=0 NormalY=0 NormalZ=1 Radius=5
  constraints (3):
    c: Radius(g0) = 5
    c: DistanceY(g-1,g0) = 28
    c: PointOnObject(g0,g-2)
FEATURE [PartDesign::Pocket] Pocket009
  Length = 5
  Sketch = -> Sketch029
  Type = 0
FEATURE [Sketcher::SketchObject] Sketch030
  Placement = pos=(27,0,0) rot=(0.57735,-0.57735,-0.57735;2.0944rad)
  Support = -> Pocket009 [Face18]
  sketch-geometry (4):
    g0: LineSegment StartX=-39 StartY=30 StartZ=0 EndX=-34 EndY=30 EndZ=0
    g1: LineSegment StartX=-34 StartY=30 StartZ=0 EndX=-34 EndY=-10 EndZ=0
    g2: LineSegment StartX=-34 StartY=-10 StartZ=0 EndX=-39 EndY=-10 EndZ=0
    g3: LineSegment StartX=-39 StartY=-10 StartZ=0 EndX=-39 EndY=30 EndZ=0
  constraints (12):
    c: Coincident(g0,g1)
    c: Coincident(g1,g2)
    c: Coincident(g2,g3)
    c: Coincident(g3,g0)
    c: Horizontal(g0)
    c: Horizontal(g2)
    c: Vertical(g1)
    c: Vertical(g3)
    c: Distance(g2) = 5
    c: DistanceX(g0,g-1) = 34
    c: DistanceY(g1,g1) = 40
    c: DistanceY(g1,g-1) = 10
FEATURE [PartDesign::Pad] Pad011
  Length = 54
  Length2 = 100
  Sketch = -> Sketch030
  Type = 0
FEATURE [PartDesign::Fillet] Fillet008
  Base = -> Pad011 [Edge73,Edge79,Edge54,Edge64]
  Radius = 4
FEATURE [Sketcher::SketchObject] Sketch031
  Placement = pos=(0,39,0) rot=(0,0.707107,0.707107;3.14159rad)
  Support = -> Fillet008 [Face17]
  sketch-geometry (4):
    g0: LineSegment StartX=-27.5 StartY=4 StartZ=0 EndX=27.5 EndY=4 EndZ=0
    g1: LineSegment StartX=27.5 StartY=4 StartZ=0 EndX=27.5 EndY=0 EndZ=0
    g2: LineSegment StartX=27.5 StartY=0 StartZ=0 EndX=-27.5 EndY=0 EndZ=0
    g3: LineSegment StartX=-27.5 StartY=0 StartZ=0 EndX=-27.5 EndY=4 EndZ=0
  constraints (12):
    c: Coincident(g0,g1)
    c: Coincident(g1,g2)
    c: Coincident(g2,g3)
    c: Coincident(g3,g0)
    c: Horizontal(g0)
    c: Horizontal(g2)
    c: Vertical(g1)
    c: Vertical(g3)
    c: DistanceY(g3,g3) = 4
    c: PointOnObject(g1,g-1)
    c: Distance(g2) = 55
    c: Symmetric(g1,g2,g-2)
FEATURE [PartDesign::Pad] Pad012
  Length = 80
  Length2 = 100
  Sketch = -> Sketch031
  Type = 0
FEATURE [PartDesign::Fillet] Fillet009
  Base = -> Pad012 [Edge17,Edge74]
  Radius = 5
FEATURE [PartDesign::Fillet] Fillet010
  Base = -> Fillet009 [Edge41,Edge8]
  Radius = 2
FEATURE [Sketcher::SketchObject] Sketch032
  Placement = pos=(0,0,0) rot=(1,0,0;3.14159rad)
  Support = -> Fillet010 [Face27]
  sketch-geometry (4):
    g0: LineSegment StartX=-18 StartY=-119 StartZ=0 EndX=-26 EndY=-119 EndZ=0
    g1: LineSegment StartX=-26 StartY=-119 StartZ=0 EndX=-26 EndY=-111 EndZ=0
    g2: LineSegment StartX=-18 StartY=-119 StartZ=0 EndX=-18 EndY=-111 EndZ=0
    g3: ArcOfCircle CenterX=-22 CenterY=-111 CenterZ=0 NormalX=0 NormalY=0 NormalZ=1 Radius=4 StartAngle=6.70092e-06 EndAngle=3.14159
  constraints (13):
    c: Horizontal(g0)
    c: Coincident(g1,g0)
    c: Vertical(g1)
    c: Coincident(g2,g0)
    c: Vertical(g2)
    c: Coincident(g3,g2)
    c: Coincident(g3,g1)
    c: Tangent(g3,g1)
    c: Distance(g0) = 8
    c: Distance(g2) = 8
    c: DistanceY(g0,g-1) = 119
    c: DistanceX(g0,g-1) = 18
    c: Tangent(g3,g2)
FEATURE [PartDesign::Pocket] Pocket010
  Length = 10
  Midplane = true
  Sketch = -> Sketch032
  Type = 0
FEATURE [Sketcher::SketchObject] Sketch033
  Placement = pos=(-30,0,1e-12) rot=(0.57735,-0.57735,-0.57735;2.0944rad)
  Support = -> Pocket010 [Face26]
  sketch-geometry (7):
    g0: Circle CenterX=-61.5 CenterY=-8.5 CenterZ=0 NormalX=0 NormalY=0 NormalZ=1 Radius=1.7
    g1: Circle CenterX=-61.5 CenterY=-16.5 CenterZ=0 NormalX=0 NormalY=0 NormalZ=1 Radius=1.7
    g2: Circle CenterX=-43.5 CenterY=-8.5 CenterZ=0 NormalX=0 NormalY=0 NormalZ=1 Radius=1.7
    g3: LineSegment [constr] StartX=-61.5 StartY=-8.5 StartZ=0 EndX=-43.5 EndY=-8.5 EndZ=0
    g4: LineSegment [constr] StartX=-43.5 StartY=-8.5 StartZ=0 EndX=-43.5 EndY=-16.5 EndZ=0
    g5: LineSegment [constr] StartX=-61.5 StartY=-16.5 StartZ=0 EndX=-43.5 EndY=-16.5 EndZ=0
    g6: Circle CenterX=-43.5 CenterY=-16.5 CenterZ=0 NormalX=0 NormalY=0 NormalZ=1 Radius=1.7
  constraints (19):
    c: Radius(g0) = 1.7
    c: Equal(g0,g1) = 1.7
    c: Equal(g0,g2) = 1.7
    c: Coincident(g3,g2)
    c: Horizontal(g3)
    c: Coincident(g4,g2)
    c: Vertical(g4)
    c: Coincident(g5,g1)
    c: Coincident(g5,g4)
    c: Horizontal(g5)
    c: Coincident(g3,g4)
    c: Equal(g6,g0)
    c: DistanceX(g2,g-1) = 43.5
    c: DistanceY(g2,g-1) = 8.5
    c: DistanceX(g3,g3) = 18
    c: DistanceY(g4,g4) = 8
    c: DistanceX(g5,g5) = 18
    c: Coincident(g0,g3)
    c: Coincident(g4,g6)
FEATURE [PartDesign::Pocket] Pocket011
  Length = 100
  Sketch = -> Sketch033
  Type = 0
FEATURE [Sketcher::SketchObject] Sketch034
  Placement = pos=(0,0,0) rot=(1,0,0;1.5708rad)
  sketch-geometry (16):
    g0: LineSegment StartX=-10 StartY=40 StartZ=0 EndX=10 EndY=40 EndZ=0
    g1: LineSegment StartX=30 StartY=20 StartZ=0 EndX=30 EndY=-20 EndZ=0
    g2: LineSegment StartX=10 StartY=-40 StartZ=0 EndX=-10 EndY=-40 EndZ=0
    g3: LineSegment StartX=-30 StartY=-20 StartZ=0 EndX=-30 EndY=20 EndZ=0
    g4: ArcOfCircle CenterX=-10 CenterY=20 CenterZ=0 NormalX=0 NormalY=0 NormalZ=1 Radius=20 StartAngle=1.5708 EndAngle=3.14159
    g5: ArcOfCircle CenterX=10 CenterY=20 CenterZ=0 NormalX=0 NormalY=0 NormalZ=1 Radius=20 StartAngle=0 EndAngle=1.5708
    g6: ArcOfCircle CenterX=10 CenterY=-20 CenterZ=0 NormalX=0 NormalY=0 NormalZ=1 Radius=20 StartAngle=4.71239 EndAngle=6.28319
    g7: ArcOfCircle CenterX=-10 CenterY=-20 CenterZ=0 NormalX=0 NormalY=0 NormalZ=1 Radius=20 StartAngle=3.14159 EndAngle=4.71239
    g8: LineSegment StartX=-10 StartY=37 StartZ=0 EndX=10 EndY=37 EndZ=0
    g9: LineSegment StartX=27 StartY=20 StartZ=0 EndX=27 EndY=-20 EndZ=0
    g10: LineSegment StartX=10 StartY=-37 StartZ=0 EndX=-10 EndY=-37 EndZ=0
    g11: LineSegment StartX=-27 StartY=-20 StartZ=0 EndX=-27 EndY=20 EndZ=0
    g12: ArcOfCircle CenterX=-10 CenterY=20 CenterZ=0 NormalX=0 NormalY=0 NormalZ=1 Radius=17 StartAngle=1.5708 EndAngle=3.14159
    g13: ArcOfCircle CenterX=10 CenterY=20 CenterZ=0 NormalX=0 NormalY=0 NormalZ=1 Radius=17 StartAngle=0 EndAngle=1.5708
    g14: ArcOfCircle CenterX=10 CenterY=-20 CenterZ=0 NormalX=0 NormalY=0 NormalZ=1 Radius=17 StartAngle=4.71239 EndAngle=6.28319
    g15: ArcOfCircle CenterX=-10 CenterY=-20 CenterZ=0 NormalX=0 NormalY=0 NormalZ=1 Radius=17 StartAngle=3.14159 EndAngle=4.71239
  constraints (38):
    c: Horizontal(g0)
    c: Horizontal(g2)
    c: Vertical(g1)
    c: Tangent(g0,g4) = 1.5708
    c: Tangent(g3,g4) = 1.5708
    c: Tangent(g0,g5) = 1.5708
    c: Tangent(g1,g5) = 1.5708
    c: Tangent(g1,g6) = 1.5708
    c: Tangent(g2,g6) = 1.5708
    c: Tangent(g2,g7) = 1.5708
    c: Tangent(g3,g7) = 1.5708
    c: Radius(g4) = 20
    c: DistanceX(g3,g1) = 60
    c: Equal(g4,g5)
    c: Equal(g6,g4)
    c: Equal(g7,g4)
    c: DistanceY(g2,g0) = 80
    c: Horizontal(g8)
    c: Horizontal(g10)
    c: Vertical(g9)
    c: Tangent(g8,g12) = 1.5708
    c: Tangent(g11,g12) = 1.5708
    c: Tangent(g8,g13) = 1.5708
    c: Tangent(g9,g13) = 1.5708
    c: Tangent(g9,g14) = 1.5708
    c: Tangent(g10,g14) = 1.5708
    c: Tangent(g10,g15) = 1.5708
    c: Tangent(g11,g15) = 1.5708
    c: DistanceX(g11,g9) = 54
    c: DistanceY(g10,g8) = 74
    c: Radius(g12) = 17
    c: Equal(g12,g13)
    c: Equal(g15,g12)
    c: Equal(g14,g12)
    c: Symmetric(g1,g3,g-2)
    c: Symmetric(g11,g9,g-2)
    c: Symmetric(g8,g10,g-1)
    c: Symmetric(g0,g2,g-1)
FEATURE [Part::Extrusion] Extrude007
  Base = -> Sketch034
  Dir = (0,120,0)
  Solid = true
FEATURE [Sketcher::SketchObject] Sketch035
  ExternalGeometry = -> [Extrude007]
  Placement = pos=(0,0,0) rot=(1,0,0;1.5708rad)
  Support = -> Extrude007 [Face17]
  sketch-geometry (8):
    g0: ArcOfCircle CenterX=-10 CenterY=20 CenterZ=0 NormalX=0 NormalY=0 NormalZ=1 Radius=20 StartAngle=1.5708 EndAngle=3.14159
    g1: ArcOfCircle CenterX=10 CenterY=20 CenterZ=0 NormalX=0 NormalY=0 NormalZ=1 Radius=20 StartAngle=1.97396e-06 EndAngle=1.5708
    g2: ArcOfCircle CenterX=10 CenterY=-20 CenterZ=0 NormalX=0 NormalY=0 NormalZ=1 Radius=20 StartAngle=4.71239 EndAngle=6.28319
    g3: ArcOfCircle CenterX=-10 CenterY=-20 CenterZ=0 NormalX=0 NormalY=0 NormalZ=1 Radius=20 StartAngle=3.14159 EndAngle=4.71239
    g4: LineSegment StartX=-30 StartY=20 StartZ=0 EndX=-30 EndY=-20 EndZ=0
    g5: LineSegment StartX=-10 StartY=40 StartZ=0 EndX=10 EndY=40 EndZ=0
    g6: LineSegment StartX=30 StartY=20 StartZ=0 EndX=30 EndY=-20 EndZ=0
    g7: LineSegment StartX=10 StartY=-40 StartZ=0 EndX=-10 EndY=-40 EndZ=0
  constraints (20):
    c: Coincident(g0,g-3)
    c: Coincident(g1,g-4)
    c: Coincident(g3,g-6)
    c: Coincident(g2,g-5)
    c: Coincident(g2,g-5)
    c: Coincident(g2,g7)
    c: Coincident(g3,g7)
    c: Coincident(g3,g-6)
    c: Coincident(g3,g4)
    c: Coincident(g0,g4)
    c: Coincident(g0,g-3)
    c: Coincident(g5,g0)
    c: Coincident(g1,g5)
    c: Coincident(g1,g-4)
    c: Coincident(g1,g6)
    c: Coincident(g6,g2)
    c: Vertical(g6)
    c: Horizontal(g7)
    c: Vertical(g4)
    c: Horizontal(g5)
FEATURE [PartDesign::Pad] Pad013
  Length = 3
  Length2 = 100
  Sketch = -> Sketch035
  Type = 0
FEATURE [PartDesign::Fillet] Fillet011
  Base = -> Pad013 [Edge49,Edge47,Edge46,Edge43,Edge42,Edge39,Edge38,Edge35]
  Radius = 17
FEATURE [PartDesign::Fillet] Fillet012
  Base = -> Fillet011 [Edge70,Edge68,Edge65,Edge79,Edge78,Edge75,Edge74,Edge71]
  Radius = 20
FEATURE [Sketcher::SketchObject] Sketch036
  Placement = pos=(0,-3,0) rot=(1,0,0;1.5708rad)
  Support = -> Fillet012 [Face9]
  sketch-geometry (4):
    g0: ArcOfCircle CenterX=0 CenterY=35 CenterZ=0 NormalX=0 NormalY=0 NormalZ=1 Radius=10 StartAngle=3.70592 EndAngle=5.71885
    g1: LineSegment StartX=-8.44947 StartY=29.6515 StartZ=0 EndX=-15 EndY=40 EndZ=0
    g2: LineSegment StartX=8.44947 StartY=29.6515 StartZ=0 EndX=15 EndY=40 EndZ=0
    g3: LineSegment StartX=-15 StartY=40 StartZ=0 EndX=15 EndY=40 EndZ=0
  constraints (13):
    c: PointOnObject(g0,g-2)
    c: Coincident(g1,g0)
    c: Coincident(g2,g0)
    c: Tangent(g1,g0)
    c: Tangent(g0,g2)
    c: Coincident(g3,g1)
    c: Coincident(g3,g2)
    c: Horizontal(g3)
    c: Symmetric(g2,g1,g-2)
    c: DistanceY(g-1,g2) = 40
    c: DistanceY(g-1,g0) = 35
    c: Radius(g0) = 10
    c: Distance(g3) = 30
FEATURE [PartDesign::Pocket] Pocket012
  Length = 10
  Sketch = -> Sketch036
  Type = 0
FEATURE [Sketcher::SketchObject] Sketch037
  ExternalGeometry = -> [Pocket012]
  Placement = pos=(0,7,0) rot=(1,0,0;1.5708rad)
  Support = -> Pocket012 [Face24]
  sketch-geometry (4):
    g0: LineSegment StartX=11.0184 StartY=33.71 StartZ=0 EndX=15.8321 EndY=41.3145 EndZ=0
    g1: LineSegment StartX=15.8321 StartY=41.3145 StartZ=0 EndX=0 EndY=41.3145 EndZ=0
    g2: LineSegment StartX=0 StartY=41.3145 StartZ=0 EndX=0 EndY=33.71 EndZ=0
    g3: LineSegment StartX=11.0184 StartY=33.71 StartZ=0 EndX=0 EndY=33.71 EndZ=0
  constraints (11):
    c: Coincident(g0,g-3)
    c: PointOnObject(g-3,g0)
    c: Distance(g0) = 9
    c: Coincident(g0,g1)
    c: PointOnObject(g1,g-2)
    c: Horizontal(g1)
    c: Horizontal(g3)
    c: Coincident(g2,g3)
    c: Coincident(g1,g2)
    c: Vertical(g2)
    c: Coincident(g0,g3)
FEATURE [PartDesign::Groove] Groove002
  Angle = 360
  Axis = (0,0,1)
  Base = (0,7,0)
  ReferenceAxis = -> Sketch037 [V_Axis]
  Sketch = -> Sketch037
FEATURE [Sketcher::SketchObject] Sketch038
  ExternalGeometry = -> [Groove002]
  Placement = pos=(27,0,0) rot=(0.57735,-0.57735,-0.57735;2.0944rad)
  Support = -> Groove002 [Face18]
  sketch-geometry (4):
    g0: LineSegment StartX=-29 StartY=16.5 StartZ=0 EndX=-25 EndY=16.5 EndZ=0
    g1: LineSegment StartX=-25 StartY=16.5 StartZ=0 EndX=-25 EndY=-11.5 EndZ=0
    g2: LineSegment StartX=-25 StartY=-11.5 StartZ=0 EndX=-29 EndY=-11.5 EndZ=0
    g3: LineSegment StartX=-29 StartY=-11.5 StartZ=0 EndX=-29 EndY=16.5 EndZ=0
  constraints (12):
    c: Coincident(g0,g1)
    c: Coincident(g1,g2)
    c: Coincident(g2,g3)
    c: Coincident(g3,g0)
    c: Horizontal(g0)
    c: Horizontal(g2)
    c: Vertical(g1)
    c: Vertical(g3)
    c: Distance(g2) = 4
    c: Distance(g1) = 28
    c: DistanceY(g0,g-3) = 3.5
    c: DistanceX(g0,g-3) = 8
FEATURE [PartDesign::Pad] Pad014
  Length = 55
  Length2 = 100
  Sketch = -> Sketch038
  Type = 0
FEATURE [Sketcher::SketchObject] Sketch039
  Placement = pos=(0,25,0) rot=(1,0,0;1.5708rad)
  Support = -> Pad014 [Face32]
  sketch-geometry (4):
    g0: LineSegment StartX=-4.75 StartY=14.25 StartZ=0 EndX=14.75 EndY=14.25 EndZ=0
    g1: LineSegment StartX=14.75 StartY=14.25 StartZ=0 EndX=14.75 EndY=-6.25 EndZ=0
    g2: LineSegment StartX=14.75 StartY=-6.25 StartZ=0 EndX=-4.75 EndY=-6.25 EndZ=0
    g3: LineSegment StartX=-4.75 StartY=-6.25 StartZ=0 EndX=-4.75 EndY=14.25 EndZ=0
  constraints (12):
    c: Coincident(g0,g1)
    c: Coincident(g1,g2)
    c: Coincident(g2,g3)
    c: Coincident(g3,g0)
    c: Horizontal(g0)
    c: Horizontal(g2)
    c: Vertical(g1)
    c: Vertical(g3)
    c: Distance(g0) = 19.5
    c: Distance(g1) = 20.5
    c: DistanceY(g2,g-1) = 6.25
    c: DistanceX(g2,g-1) = 4.75
FEATURE [PartDesign::Pocket] Pocket013
  Length = 5
  Sketch = -> Sketch039
  Type = 0
FEATURE [Sketcher::SketchObject] Sketch040
  Placement = pos=(0,29,0) rot=(0,0.707107,0.707107;3.14159rad)
  Support = -> Pocket013 [Face30]
  sketch-geometry (4):
    g0: LineSegment StartX=-15.25 StartY=17.25 StartZ=0 EndX=5.25 EndY=17.25 EndZ=0
    g1: LineSegment StartX=5.25 StartY=17.25 StartZ=0 EndX=5.25 EndY=-9.25 EndZ=0
    g2: LineSegment StartX=5.25 StartY=-9.25 StartZ=0 EndX=-15.25 EndY=-9.25 EndZ=0
    g3: LineSegment StartX=-15.25 StartY=-9.25 StartZ=0 EndX=-15.25 EndY=17.25 EndZ=0
  constraints (12):
    c: Coincident(g0,g1)
    c: Coincident(g1,g2)
    c: Coincident(g2,g3)
    c: Coincident(g3,g0)
    c: Horizontal(g0)
    c: Horizontal(g2)
    c: Vertical(g1)
    c: Vertical(g3)
    c: Distance(g2) = 20.5
    c: DistanceY(g3,g3) = 26.5
    c: DistanceY(g1,g-1) = 9.25
    c: DistanceX(g-1,g1) = 5.25
FEATURE [PartDesign::Pocket] Pocket014
  Length = 2
  Sketch = -> Sketch040
  Type = 0
FEATURE [Sketcher::SketchObject] Sketch041
  Placement = pos=(0,0,40) rot=(0,0,1;0rad)
  Support = -> Pocket014 [Face10]
  sketch-geometry (1):
    g0: Circle CenterX=0 CenterY=28 CenterZ=0 NormalX=0 NormalY=0 NormalZ=1 Radius=5
  constraints (3):
    c: Radius(g0) = 5
    c: DistanceY(g-1,g0) = 28
    c: PointOnObject(g0,g-2)
FEATURE [PartDesign::Pocket] Pocket015
  Length = 5
  Sketch = -> Sketch041
  Type = 0
FEATURE [Sketcher::SketchObject] Sketch042
  Placement = pos=(27,0,0) rot=(0.57735,-0.57735,-0.57735;2.0944rad)
  Support = -> Pocket015 [Face18]
  sketch-geometry (4):
    g0: LineSegment StartX=-39 StartY=30 StartZ=0 EndX=-34 EndY=30 EndZ=0
    g1: LineSegment StartX=-34 StartY=30 StartZ=0 EndX=-34 EndY=-10 EndZ=0
    g2: LineSegment StartX=-34 StartY=-10 StartZ=0 EndX=-39 EndY=-10 EndZ=0
    g3: LineSegment StartX=-39 StartY=-10 StartZ=0 EndX=-39 EndY=30 EndZ=0
  constraints (12):
    c: Coincident(g0,g1)
    c: Coincident(g1,g2)
    c: Coincident(g2,g3)
    c: Coincident(g3,g0)
    c: Horizontal(g0)
    c: Horizontal(g2)
    c: Vertical(g1)
    c: Vertical(g3)
    c: Distance(g2) = 5
    c: DistanceX(g0,g-1) = 34
    c: DistanceY(g1,g1) = 40
    c: DistanceY(g1,g-1) = 10
FEATURE [PartDesign::Pad] Pad015
  Length = 54
  Length2 = 100
  Sketch = -> Sketch042
  Type = 0
FEATURE [PartDesign::Fillet] Fillet013
  Base = -> Pad015 [Edge73,Edge79,Edge54,Edge64]
  Radius = 4
FEATURE [Sketcher::SketchObject] Sketch043
  Placement = pos=(0,39,0) rot=(0,0.707107,0.707107;3.14159rad)
  Support = -> Fillet013 [Face17]
  sketch-geometry (4):
    g0: LineSegment StartX=-27.5 StartY=4 StartZ=0 EndX=27.5 EndY=4 EndZ=0
    g1: LineSegment StartX=27.5 StartY=4 StartZ=0 EndX=27.5 EndY=0 EndZ=0
    g2: LineSegment StartX=27.5 StartY=0 StartZ=0 EndX=-27.5 EndY=0 EndZ=0
    g3: LineSegment StartX=-27.5 StartY=0 StartZ=0 EndX=-27.5 EndY=4 EndZ=0
  constraints (12):
    c: Coincident(g0,g1)
    c: Coincident(g1,g2)
    c: Coincident(g2,g3)
    c: Coincident(g3,g0)
    c: Horizontal(g0)
    c: Horizontal(g2)
    c: Vertical(g1)
    c: Vertical(g3)
    c: DistanceY(g3,g3) = 4
    c: PointOnObject(g1,g-1)
    c: Distance(g2) = 55
    c: Symmetric(g1,g2,g-2)
FEATURE [PartDesign::Pad] Pad016
  Length = 80
  Length2 = 100
  Sketch = -> Sketch043
  Type = 0
FEATURE [PartDesign::Fillet] Fillet014
  Base = -> Pad016 [Edge17,Edge74]
  Radius = 5
FEATURE [PartDesign::Fillet] Fillet015
  Base = -> Fillet014 [Edge41,Edge8]
  Radius = 2
FEATURE [Sketcher::SketchObject] Sketch046
  Placement = pos=(0,0,0) rot=(1,0,0;1.5708rad)
  sketch-geometry (16):
    g0: LineSegment StartX=-10 StartY=40 StartZ=0 EndX=10 EndY=40 EndZ=0
    g1: LineSegment StartX=30 StartY=20 StartZ=0 EndX=30 EndY=-20 EndZ=0
    g2: LineSegment StartX=10 StartY=-40 StartZ=0 EndX=-10 EndY=-40 EndZ=0
    g3: LineSegment StartX=-30 StartY=-20 StartZ=0 EndX=-30 EndY=20 EndZ=0
    g4: ArcOfCircle CenterX=-10 CenterY=20 CenterZ=0 NormalX=0 NormalY=0 NormalZ=1 Radius=20 StartAngle=1.5708 EndAngle=3.14159
    g5: ArcOfCircle CenterX=10 CenterY=20 CenterZ=0 NormalX=0 NormalY=0 NormalZ=1 Radius=20 StartAngle=0 EndAngle=1.5708
    g6: ArcOfCircle CenterX=10 CenterY=-20 CenterZ=0 NormalX=0 NormalY=0 NormalZ=1 Radius=20 StartAngle=4.71239 EndAngle=6.28319
    g7: ArcOfCircle CenterX=-10 CenterY=-20 CenterZ=0 NormalX=0 NormalY=0 NormalZ=1 Radius=20 StartAngle=3.14159 EndAngle=4.71239
    g8: LineSegment StartX=-10 StartY=37 StartZ=0 EndX=10 EndY=37 EndZ=0
    g9: LineSegment StartX=27 StartY=20 StartZ=0 EndX=27 EndY=-20 EndZ=0
    g10: LineSegment StartX=10 StartY=-37 StartZ=0 EndX=-10 EndY=-37 EndZ=0
    g11: LineSegment StartX=-27 StartY=-20 StartZ=0 EndX=-27 EndY=20 EndZ=0
    g12: ArcOfCircle CenterX=-10 CenterY=20 CenterZ=0 NormalX=0 NormalY=0 NormalZ=1 Radius=17 StartAngle=1.5708 EndAngle=3.14159
    g13: ArcOfCircle CenterX=10 CenterY=20 CenterZ=0 NormalX=0 NormalY=0 NormalZ=1 Radius=17 StartAngle=0 EndAngle=1.5708
    g14: ArcOfCircle CenterX=10 CenterY=-20 CenterZ=0 NormalX=0 NormalY=0 NormalZ=1 Radius=17 StartAngle=4.71239 EndAngle=6.28319
    g15: ArcOfCircle CenterX=-10 CenterY=-20 CenterZ=0 NormalX=0 NormalY=0 NormalZ=1 Radius=17 StartAngle=3.14159 EndAngle=4.71239
  constraints (38):
    c: Horizontal(g0)
    c: Horizontal(g2)
    c: Vertical(g1)
    c: Tangent(g0,g4) = 1.5708
    c: Tangent(g3,g4) = 1.5708
    c: Tangent(g0,g5) = 1.5708
    c: Tangent(g1,g5) = 1.5708
    c: Tangent(g1,g6) = 1.5708
    c: Tangent(g2,g6) = 1.5708
    c: Tangent(g2,g7) = 1.5708
    c: Tangent(g3,g7) = 1.5708
    c: Radius(g4) = 20
    c: DistanceX(g3,g1) = 60
    c: Equal(g4,g5)
    c: Equal(g6,g4)
    c: Equal(g7,g4)
    c: DistanceY(g2,g0) = 80
    c: Horizontal(g8)
    c: Horizontal(g10)
    c: Vertical(g9)
    c: Tangent(g8,g12) = 1.5708
    c: Tangent(g11,g12) = 1.5708
    c: Tangent(g8,g13) = 1.5708
    c: Tangent(g9,g13) = 1.5708
    c: Tangent(g9,g14) = 1.5708
    c: Tangent(g10,g14) = 1.5708
    c: Tangent(g10,g15) = 1.5708
    c: Tangent(g11,g15) = 1.5708
    c: DistanceX(g11,g9) = 54
    c: DistanceY(g10,g8) = 74
    c: Radius(g12) = 17
    c: Equal(g12,g13)
    c: Equal(g15,g12)
    c: Equal(g14,g12)
    c: Symmetric(g1,g3,g-2)
    c: Symmetric(g11,g9,g-2)
    c: Symmetric(g8,g10,g-1)
    c: Symmetric(g0,g2,g-1)
FEATURE [Part::Extrusion] Extrude008
  Base = -> Sketch046
  Dir = (0,120,0)
  Solid = true
FEATURE [Sketcher::SketchObject] Sketch047
  ExternalGeometry = -> [Extrude008]
  Placement = pos=(0,0,0) rot=(1,0,0;1.5708rad)
  Support = -> Extrude008 [Face17]
  sketch-geometry (8):
    g0: ArcOfCircle CenterX=-10 CenterY=20 CenterZ=0 NormalX=0 NormalY=0 NormalZ=1 Radius=20 StartAngle=1.5708 EndAngle=3.14159
    g1: ArcOfCircle CenterX=10 CenterY=20 CenterZ=0 NormalX=0 NormalY=0 NormalZ=1 Radius=20 StartAngle=1.97396e-06 EndAngle=1.5708
    g2: ArcOfCircle CenterX=10 CenterY=-20 CenterZ=0 NormalX=0 NormalY=0 NormalZ=1 Radius=20 StartAngle=4.71239 EndAngle=6.28319
    g3: ArcOfCircle CenterX=-10 CenterY=-20 CenterZ=0 NormalX=0 NormalY=0 NormalZ=1 Radius=20 StartAngle=3.14159 EndAngle=4.71239
    g4: LineSegment StartX=-30 StartY=20 StartZ=0 EndX=-30 EndY=-20 EndZ=0
    g5: LineSegment StartX=-10 StartY=40 StartZ=0 EndX=10 EndY=40 EndZ=0
    g6: LineSegment StartX=30 StartY=20 StartZ=0 EndX=30 EndY=-20 EndZ=0
    g7: LineSegment StartX=10 StartY=-40 StartZ=0 EndX=-10 EndY=-40 EndZ=0
  constraints (20):
    c: Coincident(g0,g-3)
    c: Coincident(g1,g-4)
    c: Coincident(g3,g-6)
    c: Coincident(g2,g-5)
    c: Coincident(g2,g-5)
    c: Coincident(g2,g7)
    c: Coincident(g3,g7)
    c: Coincident(g3,g-6)
    c: Coincident(g3,g4)
    c: Coincident(g0,g4)
    c: Coincident(g0,g-3)
    c: Coincident(g5,g0)
    c: Coincident(g1,g5)
    c: Coincident(g1,g-4)
    c: Coincident(g1,g6)
    c: Coincident(g6,g2)
    c: Vertical(g6)
    c: Horizontal(g7)
    c: Vertical(g4)
    c: Horizontal(g5)
FEATURE [PartDesign::Pad] Pad017
  Length = 3
  Length2 = 100
  Sketch = -> Sketch047
  Type = 0
FEATURE [PartDesign::Fillet] Fillet016
  Base = -> Pad017 [Edge49,Edge47,Edge46,Edge43,Edge42,Edge39,Edge38,Edge35]
  Radius = 17
FEATURE [PartDesign::Fillet] Fillet017
  Base = -> Fillet016 [Edge70,Edge68,Edge65,Edge79,Edge78,Edge75,Edge74,Edge71]
  Radius = 20
FEATURE [Sketcher::SketchObject] Sketch048
  Placement = pos=(0,-3,0) rot=(1,0,0;1.5708rad)
  Support = -> Fillet017 [Face9]
  sketch-geometry (4):
    g0: ArcOfCircle CenterX=0 CenterY=35 CenterZ=0 NormalX=0 NormalY=0 NormalZ=1 Radius=10 StartAngle=3.70592 EndAngle=5.71885
    g1: LineSegment StartX=-8.44947 StartY=29.6515 StartZ=0 EndX=-15 EndY=40 EndZ=0
    g2: LineSegment StartX=8.44947 StartY=29.6515 StartZ=0 EndX=15 EndY=40 EndZ=0
    g3: LineSegment StartX=-15 StartY=40 StartZ=0 EndX=15 EndY=40 EndZ=0
  constraints (13):
    c: PointOnObject(g0,g-2)
    c: Coincident(g1,g0)
    c: Coincident(g2,g0)
    c: Tangent(g1,g0)
    c: Tangent(g0,g2)
    c: Coincident(g3,g1)
    c: Coincident(g3,g2)
    c: Horizontal(g3)
    c: Symmetric(g2,g1,g-2)
    c: DistanceY(g-1,g2) = 40
    c: DistanceY(g-1,g0) = 35
    c: Radius(g0) = 10
    c: Distance(g3) = 30
FEATURE [PartDesign::Pocket] Pocket018
  Length = 10
  Sketch = -> Sketch048
  Type = 0
FEATURE [Sketcher::SketchObject] Sketch049
  ExternalGeometry = -> [Pocket018]
  Placement = pos=(0,7,0) rot=(1,0,0;1.5708rad)
  Support = -> Pocket018 [Face24]
  sketch-geometry (4):
    g0: LineSegment StartX=11.0184 StartY=33.71 StartZ=0 EndX=15.8321 EndY=41.3145 EndZ=0
    g1: LineSegment StartX=15.8321 StartY=41.3145 StartZ=0 EndX=0 EndY=41.3145 EndZ=0
    g2: LineSegment StartX=0 StartY=41.3145 StartZ=0 EndX=0 EndY=33.71 EndZ=0
    g3: LineSegment StartX=11.0184 StartY=33.71 StartZ=0 EndX=0 EndY=33.71 EndZ=0
  constraints (11):
    c: Coincident(g0,g-3)
    c: PointOnObject(g-3,g0)
    c: Distance(g0) = 9
    c: Coincident(g0,g1)
    c: PointOnObject(g1,g-2)
    c: Horizontal(g1)
    c: Horizontal(g3)
    c: Coincident(g2,g3)
    c: Coincident(g1,g2)
    c: Vertical(g2)
    c: Coincident(g0,g3)
FEATURE [PartDesign::Groove] Groove003
  Angle = 360
  Axis = (0,0,1)
  Base = (0,7,0)
  ReferenceAxis = -> Sketch049 [V_Axis]
  Sketch = -> Sketch049
FEATURE [Sketcher::SketchObject] Sketch050
  ExternalGeometry = -> [Groove003]
  Placement = pos=(27,0,0) rot=(0.57735,-0.57735,-0.57735;2.0944rad)
  Support = -> Groove003 [Face18]
  sketch-geometry (4):
    g0: LineSegment StartX=-29 StartY=16.5 StartZ=0 EndX=-25 EndY=16.5 EndZ=0
    g1: LineSegment StartX=-25 StartY=16.5 StartZ=0 EndX=-25 EndY=-11.5 EndZ=0
    g2: LineSegment StartX=-25 StartY=-11.5 StartZ=0 EndX=-29 EndY=-11.5 EndZ=0
    g3: LineSegment StartX=-29 StartY=-11.5 StartZ=0 EndX=-29 EndY=16.5 EndZ=0
  constraints (12):
    c: Coincident(g0,g1)
    c: Coincident(g1,g2)
    c: Coincident(g2,g3)
    c: Coincident(g3,g0)
    c: Horizontal(g0)
    c: Horizontal(g2)
    c: Vertical(g1)
    c: Vertical(g3)
    c: Distance(g2) = 4
    c: Distance(g1) = 28
    c: DistanceY(g0,g-3) = 3.5
    c: DistanceX(g0,g-3) = 8
FEATURE [PartDesign::Pad] Pad018
  Length = 55
  Length2 = 100
  Sketch = -> Sketch050
  Type = 0
FEATURE [Sketcher::SketchObject] Sketch051
  Placement = pos=(0,25,0) rot=(1,0,0;1.5708rad)
  Support = -> Pad018 [Face32]
  sketch-geometry (4):
    g0: LineSegment StartX=-4.75 StartY=14.25 StartZ=0 EndX=14.75 EndY=14.25 EndZ=0
    g1: LineSegment StartX=14.75 StartY=14.25 StartZ=0 EndX=14.75 EndY=-6.25 EndZ=0
    g2: LineSegment StartX=14.75 StartY=-6.25 StartZ=0 EndX=-4.75 EndY=-6.25 EndZ=0
    g3: LineSegment StartX=-4.75 StartY=-6.25 StartZ=0 EndX=-4.75 EndY=14.25 EndZ=0
  constraints (12):
    c: Coincident(g0,g1)
    c: Coincident(g1,g2)
    c: Coincident(g2,g3)
    c: Coincident(g3,g0)
    c: Horizontal(g0)
    c: Horizontal(g2)
    c: Vertical(g1)
    c: Vertical(g3)
    c: Distance(g0) = 19.5
    c: Distance(g1) = 20.5
    c: DistanceY(g2,g-1) = 6.25
    c: DistanceX(g2,g-1) = 4.75
FEATURE [PartDesign::Pocket] Pocket019
  Length = 5
  Sketch = -> Sketch051
  Type = 0
FEATURE [Sketcher::SketchObject] Sketch052
  Placement = pos=(0,29,0) rot=(0,0.707107,0.707107;3.14159rad)
  Support = -> Pocket019 [Face30]
  sketch-geometry (4):
    g0: LineSegment StartX=-15.25 StartY=17.25 StartZ=0 EndX=5.25 EndY=17.25 EndZ=0
    g1: LineSegment StartX=5.25 StartY=17.25 StartZ=0 EndX=5.25 EndY=-9.25 EndZ=0
    g2: LineSegment StartX=5.25 StartY=-9.25 StartZ=0 EndX=-15.25 EndY=-9.25 EndZ=0
    g3: LineSegment StartX=-15.25 StartY=-9.25 StartZ=0 EndX=-15.25 EndY=17.25 EndZ=0
  constraints (12):
    c: Coincident(g0,g1)
    c: Coincident(g1,g2)
    c: Coincident(g2,g3)
    c: Coincident(g3,g0)
    c: Horizontal(g0)
    c: Horizontal(g2)
    c: Vertical(g1)
    c: Vertical(g3)
    c: Distance(g2) = 20.5
    c: DistanceY(g3,g3) = 26.5
    c: DistanceY(g1,g-1) = 9.25
    c: DistanceX(g-1,g1) = 5.25
FEATURE [PartDesign::Pocket] Pocket020
  Length = 2
  Sketch = -> Sketch052
  Type = 0
FEATURE [Sketcher::SketchObject] Sketch053
  Placement = pos=(0,0,40) rot=(0,0,1;0rad)
  Support = -> Pocket020 [Face10]
  sketch-geometry (1):
    g0: Circle CenterX=0 CenterY=28 CenterZ=0 NormalX=0 NormalY=0 NormalZ=1 Radius=5
  constraints (3):
    c: Radius(g0) = 5
    c: DistanceY(g-1,g0) = 28
    c: PointOnObject(g0,g-2)
FEATURE [PartDesign::Pocket] Pocket021
  Length = 5
  Sketch = -> Sketch053
  Type = 0
FEATURE [Sketcher::SketchObject] Sketch054
  Placement = pos=(27,0,0) rot=(0.57735,-0.57735,-0.57735;2.0944rad)
  Support = -> Pocket021 [Face18]
  sketch-geometry (4):
    g0: LineSegment StartX=-39 StartY=30 StartZ=0 EndX=-34 EndY=30 EndZ=0
    g1: LineSegment StartX=-34 StartY=30 StartZ=0 EndX=-34 EndY=-10 EndZ=0
    g2: LineSegment StartX=-34 StartY=-10 StartZ=0 EndX=-39 EndY=-10 EndZ=0
    g3: LineSegment StartX=-39 StartY=-10 StartZ=0 EndX=-39 EndY=30 EndZ=0
  constraints (12):
    c: Coincident(g0,g1)
    c: Coincident(g1,g2)
    c: Coincident(g2,g3)
    c: Coincident(g3,g0)
    c: Horizontal(g0)
    c: Horizontal(g2)
    c: Vertical(g1)
    c: Vertical(g3)
    c: Distance(g2) = 5
    c: DistanceX(g0,g-1) = 34
    c: DistanceY(g1,g1) = 40
    c: DistanceY(g1,g-1) = 10
FEATURE [PartDesign::Pad] Pad019
  Length = 54
  Length2 = 100
  Sketch = -> Sketch054
  Type = 0
FEATURE [PartDesign::Fillet] Fillet018
  Base = -> Pad019 [Edge73,Edge79,Edge54,Edge64]
  Radius = 4
FEATURE [Sketcher::SketchObject] Sketch055
  Placement = pos=(0,39,0) rot=(0,0.707107,0.707107;3.14159rad)
  Support = -> Fillet018 [Face17]
  sketch-geometry (4):
    g0: LineSegment StartX=-27.5 StartY=4 StartZ=0 EndX=27.5 EndY=4 EndZ=0
    g1: LineSegment StartX=27.5 StartY=4 StartZ=0 EndX=27.5 EndY=0 EndZ=0
    g2: LineSegment StartX=27.5 StartY=0 StartZ=0 EndX=-27.5 EndY=0 EndZ=0
    g3: LineSegment StartX=-27.5 StartY=0 StartZ=0 EndX=-27.5 EndY=4 EndZ=0
  constraints (12):
    c: Coincident(g0,g1)
    c: Coincident(g1,g2)
    c: Coincident(g2,g3)
    c: Coincident(g3,g0)
    c: Horizontal(g0)
    c: Horizontal(g2)
    c: Vertical(g1)
    c: Vertical(g3)
    c: DistanceY(g3,g3) = 4
    c: PointOnObject(g1,g-1)
    c: Distance(g2) = 55
    c: Symmetric(g1,g2,g-2)
FEATURE [PartDesign::Pad] Pad020
  Length = 80
  Length2 = 100
  Sketch = -> Sketch055
  Type = 0
FEATURE [PartDesign::Fillet] Fillet019
  Base = -> Pad020 [Edge17,Edge74]
  Radius = 5
FEATURE [PartDesign::Fillet] Fillet020
  Base = -> Fillet019 [Edge41,Edge8]
  Radius = 2
FEATURE [Sketcher::SketchObject] Sketch056
  Placement = pos=(0,0,0) rot=(1,0,0;3.14159rad)
  Support = -> Fillet020 [Face27]
  sketch-geometry (4):
    g0: LineSegment StartX=-18 StartY=-119 StartZ=0 EndX=-26 EndY=-119 EndZ=0
    g1: LineSegment StartX=-26 StartY=-119 StartZ=0 EndX=-26 EndY=-111 EndZ=0
    g2: LineSegment StartX=-18 StartY=-119 StartZ=0 EndX=-18 EndY=-111 EndZ=0
    g3: ArcOfCircle CenterX=-22 CenterY=-111 CenterZ=0 NormalX=0 NormalY=0 NormalZ=1 Radius=4 StartAngle=6.70092e-06 EndAngle=3.14159
  constraints (13):
    c: Horizontal(g0)
    c: Coincident(g1,g0)
    c: Vertical(g1)
    c: Coincident(g2,g0)
    c: Vertical(g2)
    c: Coincident(g3,g2)
    c: Coincident(g3,g1)
    c: Tangent(g3,g1)
    c: Distance(g0) = 8
    c: Distance(g2) = 8
    c: DistanceY(g0,g-1) = 119
    c: DistanceX(g0,g-1) = 18
    c: Tangent(g3,g2)
FEATURE [PartDesign::Pocket] Pocket022
  Length = 10
  Midplane = true
  Sketch = -> Sketch056
  Type = 0
FEATURE [Sketcher::SketchObject] Sketch057
  Placement = pos=(-30,0,1e-12) rot=(0.57735,-0.57735,-0.57735;2.0944rad)
  Support = -> Pocket022 [Face26]
  sketch-geometry (7):
    g0: Circle CenterX=-56.5 CenterY=11.5 CenterZ=0 NormalX=0 NormalY=0 NormalZ=1 Radius=1.7
    g1: Circle CenterX=-56.5 CenterY=-11.5 CenterZ=0 NormalX=0 NormalY=0 NormalZ=1 Radius=1.7
    g2: Circle CenterX=-43.5 CenterY=11.5 CenterZ=0 NormalX=0 NormalY=0 NormalZ=1 Radius=1.7
    g3: LineSegment [constr] StartX=-56.5 StartY=11.5 StartZ=0 EndX=-43.5 EndY=11.5 EndZ=0
    g4: LineSegment [constr] StartX=-43.5 StartY=11.5 StartZ=0 EndX=-43.5 EndY=-11.5 EndZ=0
    g5: LineSegment [constr] StartX=-56.5 StartY=-11.5 StartZ=0 EndX=-43.5 EndY=-11.5 EndZ=0
    g6: Circle CenterX=-43.5 CenterY=-11.5 CenterZ=0 NormalX=0 NormalY=0 NormalZ=1 Radius=1.7
  constraints (19):
    c: Radius(g0) = 1.7
    c: Equal(g0,g1) = 1.7
    c: Equal(g0,g2) = 1.7
    c: Coincident(g3,g2)
    c: Horizontal(g3)
    c: Coincident(g4,g2)
    c: Vertical(g4)
    c: Coincident(g5,g1)
    c: Coincident(g5,g4)
    c: Horizontal(g5)
    c: Coincident(g3,g4)
    c: Equal(g6,g0)
    c: DistanceX(g2,g-1) = 43.5
    c: DistanceX(g3,g3) = 13
    c: DistanceY(g4,g4) = 23
    c: DistanceX(g5,g5) = 13
    c: Coincident(g0,g3)
    c: Coincident(g4,g6)
    c: DistanceY(g4,g-1) = 11.5
FEATURE [PartDesign::Pocket] Pocket023
  Length = 100
  Sketch = -> Sketch057
  Type = 0
FEATURE [Sketcher::SketchObject] Sketch058
  Placement = pos=(0,0,0) rot=(1,0,0;1.5708rad)
  sketch-geometry (16):
    g0: LineSegment StartX=-10 StartY=40 StartZ=0 EndX=10 EndY=40 EndZ=0
    g1: LineSegment StartX=30 StartY=20 StartZ=0 EndX=30 EndY=-20 EndZ=0
    g2: LineSegment StartX=10 StartY=-40 StartZ=0 EndX=-10 EndY=-40 EndZ=0
    g3: LineSegment StartX=-30 StartY=-20 StartZ=0 EndX=-30 EndY=20 EndZ=0
    g4: ArcOfCircle CenterX=-10 CenterY=20 CenterZ=0 NormalX=0 NormalY=0 NormalZ=1 Radius=20 StartAngle=1.5708 EndAngle=3.14159
    g5: ArcOfCircle CenterX=10 CenterY=20 CenterZ=0 NormalX=0 NormalY=0 NormalZ=1 Radius=20 StartAngle=0 EndAngle=1.5708
    g6: ArcOfCircle CenterX=10 CenterY=-20 CenterZ=0 NormalX=0 NormalY=0 NormalZ=1 Radius=20 StartAngle=4.71239 EndAngle=6.28319
    g7: ArcOfCircle CenterX=-10 CenterY=-20 CenterZ=0 NormalX=0 NormalY=0 NormalZ=1 Radius=20 StartAngle=3.14159 EndAngle=4.71239
    g8: LineSegment StartX=-10 StartY=37 StartZ=0 EndX=10 EndY=37 EndZ=0
    g9: LineSegment StartX=27 StartY=20 StartZ=0 EndX=27 EndY=-20 EndZ=0
    g10: LineSegment StartX=10 StartY=-37 StartZ=0 EndX=-10 EndY=-37 EndZ=0
    g11: LineSegment StartX=-27 StartY=-20 StartZ=0 EndX=-27 EndY=20 EndZ=0
    g12: ArcOfCircle CenterX=-10 CenterY=20 CenterZ=0 NormalX=0 NormalY=0 NormalZ=1 Radius=17 StartAngle=1.5708 EndAngle=3.14159
    g13: ArcOfCircle CenterX=10 CenterY=20 CenterZ=0 NormalX=0 NormalY=0 NormalZ=1 Radius=17 StartAngle=0 EndAngle=1.5708
    g14: ArcOfCircle CenterX=10 CenterY=-20 CenterZ=0 NormalX=0 NormalY=0 NormalZ=1 Radius=17 StartAngle=4.71239 EndAngle=6.28319
    g15: ArcOfCircle CenterX=-10 CenterY=-20 CenterZ=0 NormalX=0 NormalY=0 NormalZ=1 Radius=17 StartAngle=3.14159 EndAngle=4.71239
  constraints (38):
    c: Horizontal(g0)
    c: Horizontal(g2)
    c: Vertical(g1)
    c: Tangent(g0,g4) = 1.5708
    c: Tangent(g3,g4) = 1.5708
    c: Tangent(g0,g5) = 1.5708
    c: Tangent(g1,g5) = 1.5708
    c: Tangent(g1,g6) = 1.5708
    c: Tangent(g2,g6) = 1.5708
    c: Tangent(g2,g7) = 1.5708
    c: Tangent(g3,g7) = 1.5708
    c: Radius(g4) = 20
    c: DistanceX(g3,g1) = 60
    c: Equal(g4,g5)
    c: Equal(g6,g4)
    c: Equal(g7,g4)
    c: DistanceY(g2,g0) = 80
    c: Horizontal(g8)
    c: Horizontal(g10)
    c: Vertical(g9)
    c: Tangent(g8,g12) = 1.5708
    c: Tangent(g11,g12) = 1.5708
    c: Tangent(g8,g13) = 1.5708
    c: Tangent(g9,g13) = 1.5708
    c: Tangent(g9,g14) = 1.5708
    c: Tangent(g10,g14) = 1.5708
    c: Tangent(g10,g15) = 1.5708
    c: Tangent(g11,g15) = 1.5708
    c: DistanceX(g11,g9) = 54
    c: DistanceY(g10,g8) = 74
    c: Radius(g12) = 17
    c: Equal(g12,g13)
    c: Equal(g15,g12)
    c: Equal(g14,g12)
    c: Symmetric(g1,g3,g-2)
    c: Symmetric(g11,g9,g-2)
    c: Symmetric(g8,g10,g-1)
    c: Symmetric(g0,g2,g-1)
FEATURE [Part::Extrusion] Extrude009
  Base = -> Sketch058
  Dir = (0,120,0)
  Solid = true
FEATURE [Sketcher::SketchObject] Sketch059
  ExternalGeometry = -> [Extrude009]
  Placement = pos=(0,0,0) rot=(1,0,0;1.5708rad)
  Support = -> Extrude009 [Face17]
  sketch-geometry (8):
    g0: ArcOfCircle CenterX=-10 CenterY=20 CenterZ=0 NormalX=0 NormalY=0 NormalZ=1 Radius=20 StartAngle=1.5708 EndAngle=3.14159
    g1: ArcOfCircle CenterX=10 CenterY=20 CenterZ=0 NormalX=0 NormalY=0 NormalZ=1 Radius=20 StartAngle=1.97396e-06 EndAngle=1.5708
    g2: ArcOfCircle CenterX=10 CenterY=-20 CenterZ=0 NormalX=0 NormalY=0 NormalZ=1 Radius=20 StartAngle=4.71239 EndAngle=6.28319
    g3: ArcOfCircle CenterX=-10 CenterY=-20 CenterZ=0 NormalX=0 NormalY=0 NormalZ=1 Radius=20 StartAngle=3.14159 EndAngle=4.71239
    g4: LineSegment StartX=-30 StartY=20 StartZ=0 EndX=-30 EndY=-20 EndZ=0
    g5: LineSegment StartX=-10 StartY=40 StartZ=0 EndX=10 EndY=40 EndZ=0
    g6: LineSegment StartX=30 StartY=20 StartZ=0 EndX=30 EndY=-20 EndZ=0
    g7: LineSegment StartX=10 StartY=-40 StartZ=0 EndX=-10 EndY=-40 EndZ=0
  constraints (20):
    c: Coincident(g0,g-3)
    c: Coincident(g1,g-4)
    c: Coincident(g3,g-6)
    c: Coincident(g2,g-5)
    c: Coincident(g2,g-5)
    c: Coincident(g2,g7)
    c: Coincident(g3,g7)
    c: Coincident(g3,g-6)
    c: Coincident(g3,g4)
    c: Coincident(g0,g4)
    c: Coincident(g0,g-3)
    c: Coincident(g5,g0)
    c: Coincident(g1,g5)
    c: Coincident(g1,g-4)
    c: Coincident(g1,g6)
    c: Coincident(g6,g2)
    c: Vertical(g6)
    c: Horizontal(g7)
    c: Vertical(g4)
    c: Horizontal(g5)
FEATURE [PartDesign::Pad] Pad021
  Length = 3
  Length2 = 100
  Sketch = -> Sketch059
  Type = 0
FEATURE [PartDesign::Fillet] Fillet021
  Base = -> Pad021 [Edge49,Edge47,Edge46,Edge43,Edge42,Edge39,Edge38,Edge35]
  Radius = 17
FEATURE [PartDesign::Fillet] Fillet022
  Base = -> Fillet021 [Edge70,Edge68,Edge65,Edge79,Edge78,Edge75,Edge74,Edge71]
  Radius = 20
FEATURE [Sketcher::SketchObject] Sketch060
  Placement = pos=(0,-3,0) rot=(1,0,0;1.5708rad)
  Support = -> Fillet022 [Face9]
  sketch-geometry (4):
    g0: ArcOfCircle CenterX=0 CenterY=35 CenterZ=0 NormalX=0 NormalY=0 NormalZ=1 Radius=10 StartAngle=3.70592 EndAngle=5.71885
    g1: LineSegment StartX=-8.44947 StartY=29.6515 StartZ=0 EndX=-15 EndY=40 EndZ=0
    g2: LineSegment StartX=8.44947 StartY=29.6515 StartZ=0 EndX=15 EndY=40 EndZ=0
    g3: LineSegment StartX=-15 StartY=40 StartZ=0 EndX=15 EndY=40 EndZ=0
  constraints (13):
    c: PointOnObject(g0,g-2)
    c: Coincident(g1,g0)
    c: Coincident(g2,g0)
    c: Tangent(g1,g0)
    c: Tangent(g0,g2)
    c: Coincident(g3,g1)
    c: Coincident(g3,g2)
    c: Horizontal(g3)
    c: Symmetric(g2,g1,g-2)
    c: DistanceY(g-1,g2) = 40
    c: DistanceY(g-1,g0) = 35
    c: Radius(g0) = 10
    c: Distance(g3) = 30
FEATURE [PartDesign::Pocket] Pocket024
  Length = 10
  Sketch = -> Sketch060
  Type = 0
FEATURE [Sketcher::SketchObject] Sketch061
  ExternalGeometry = -> [Pocket024]
  Placement = pos=(0,7,0) rot=(1,0,0;1.5708rad)
  Support = -> Pocket024 [Face24]
  sketch-geometry (4):
    g0: LineSegment StartX=11.0184 StartY=33.71 StartZ=0 EndX=15.8321 EndY=41.3145 EndZ=0
    g1: LineSegment StartX=15.8321 StartY=41.3145 StartZ=0 EndX=0 EndY=41.3145 EndZ=0
    g2: LineSegment StartX=0 StartY=41.3145 StartZ=0 EndX=0 EndY=33.71 EndZ=0
    g3: LineSegment StartX=11.0184 StartY=33.71 StartZ=0 EndX=0 EndY=33.71 EndZ=0
  constraints (11):
    c: Coincident(g0,g-3)
    c: PointOnObject(g-3,g0)
    c: Distance(g0) = 9
    c: Coincident(g0,g1)
    c: PointOnObject(g1,g-2)
    c: Horizontal(g1)
    c: Horizontal(g3)
    c: Coincident(g2,g3)
    c: Coincident(g1,g2)
    c: Vertical(g2)
    c: Coincident(g0,g3)
FEATURE [PartDesign::Groove] Groove004
  Angle = 360
  Axis = (0,0,1)
  Base = (0,7,0)
  ReferenceAxis = -> Sketch061 [V_Axis]
  Sketch = -> Sketch061
FEATURE [Sketcher::SketchObject] Sketch062
  ExternalGeometry = -> [Groove004]
  Placement = pos=(27,0,0) rot=(0.57735,-0.57735,-0.57735;2.0944rad)
  Support = -> Groove004 [Face18]
  sketch-geometry (4):
    g0: LineSegment StartX=-29 StartY=16.5 StartZ=0 EndX=-25 EndY=16.5 EndZ=0
    g1: LineSegment StartX=-25 StartY=16.5 StartZ=0 EndX=-25 EndY=-11.5 EndZ=0
    g2: LineSegment StartX=-25 StartY=-11.5 StartZ=0 EndX=-29 EndY=-11.5 EndZ=0
    g3: LineSegment StartX=-29 StartY=-11.5 StartZ=0 EndX=-29 EndY=16.5 EndZ=0
  constraints (12):
    c: Coincident(g0,g1)
    c: Coincident(g1,g2)
    c: Coincident(g2,g3)
    c: Coincident(g3,g0)
    c: Horizontal(g0)
    c: Horizontal(g2)
    c: Vertical(g1)
    c: Vertical(g3)
    c: Distance(g2) = 4
    c: Distance(g1) = 28
    c: DistanceY(g0,g-3) = 3.5
    c: DistanceX(g0,g-3) = 8
FEATURE [PartDesign::Pad] Pad022
  Length = 55
  Length2 = 100
  Sketch = -> Sketch062
  Type = 0
FEATURE [Sketcher::SketchObject] Sketch063
  Placement = pos=(0,25,0) rot=(1,0,0;1.5708rad)
  Support = -> Pad022 [Face32]
  sketch-geometry (4):
    g0: LineSegment StartX=-4.75 StartY=14.25 StartZ=0 EndX=14.75 EndY=14.25 EndZ=0
    g1: LineSegment StartX=14.75 StartY=14.25 StartZ=0 EndX=14.75 EndY=-6.25 EndZ=0
    g2: LineSegment StartX=14.75 StartY=-6.25 StartZ=0 EndX=-4.75 EndY=-6.25 EndZ=0
    g3: LineSegment StartX=-4.75 StartY=-6.25 StartZ=0 EndX=-4.75 EndY=14.25 EndZ=0
  constraints (12):
    c: Coincident(g0,g1)
    c: Coincident(g1,g2)
    c: Coincident(g2,g3)
    c: Coincident(g3,g0)
    c: Horizontal(g0)
    c: Horizontal(g2)
    c: Vertical(g1)
    c: Vertical(g3)
    c: Distance(g0) = 19.5
    c: Distance(g1) = 20.5
    c: DistanceY(g2,g-1) = 6.25
    c: DistanceX(g2,g-1) = 4.75
FEATURE [PartDesign::Pocket] Pocket025
  Length = 5
  Sketch = -> Sketch063
  Type = 0
FEATURE [Sketcher::SketchObject] Sketch064
  Placement = pos=(0,29,0) rot=(0,0.707107,0.707107;3.14159rad)
  Support = -> Pocket025 [Face30]
  sketch-geometry (4):
    g0: LineSegment StartX=-15.25 StartY=17.25 StartZ=0 EndX=5.25 EndY=17.25 EndZ=0
    g1: LineSegment StartX=5.25 StartY=17.25 StartZ=0 EndX=5.25 EndY=-9.25 EndZ=0
    g2: LineSegment StartX=5.25 StartY=-9.25 StartZ=0 EndX=-15.25 EndY=-9.25 EndZ=0
    g3: LineSegment StartX=-15.25 StartY=-9.25 StartZ=0 EndX=-15.25 EndY=17.25 EndZ=0
  constraints (12):
    c: Coincident(g0,g1)
    c: Coincident(g1,g2)
    c: Coincident(g2,g3)
    c: Coincident(g3,g0)
    c: Horizontal(g0)
    c: Horizontal(g2)
    c: Vertical(g1)
    c: Vertical(g3)
    c: Distance(g2) = 20.5
    c: DistanceY(g3,g3) = 26.5
    c: DistanceY(g1,g-1) = 9.25
    c: DistanceX(g-1,g1) = 5.25
FEATURE [PartDesign::Pocket] Pocket026
  Length = 2
  Sketch = -> Sketch064
  Type = 0
FEATURE [Sketcher::SketchObject] Sketch065
  Placement = pos=(0,0,40) rot=(0,0,1;0rad)
  Support = -> Pocket026 [Face10]
  sketch-geometry (1):
    g0: Circle CenterX=0 CenterY=28 CenterZ=0 NormalX=0 NormalY=0 NormalZ=1 Radius=5
  constraints (3):
    c: Radius(g0) = 5
    c: DistanceY(g-1,g0) = 28
    c: PointOnObject(g0,g-2)
FEATURE [PartDesign::Pocket] Pocket027
  Length = 5
  Sketch = -> Sketch065
  Type = 0
FEATURE [Sketcher::SketchObject] Sketch066
  Placement = pos=(27,0,0) rot=(0.57735,-0.57735,-0.57735;2.0944rad)
  Support = -> Pocket027 [Face18]
  sketch-geometry (4):
    g0: LineSegment StartX=-39 StartY=30 StartZ=0 EndX=-34 EndY=30 EndZ=0
    g1: LineSegment StartX=-34 StartY=30 StartZ=0 EndX=-34 EndY=-10 EndZ=0
    g2: LineSegment StartX=-34 StartY=-10 StartZ=0 EndX=-39 EndY=-10 EndZ=0
    g3: LineSegment StartX=-39 StartY=-10 StartZ=0 EndX=-39 EndY=30 EndZ=0
  constraints (12):
    c: Coincident(g0,g1)
    c: Coincident(g1,g2)
    c: Coincident(g2,g3)
    c: Coincident(g3,g0)
    c: Horizontal(g0)
    c: Horizontal(g2)
    c: Vertical(g1)
    c: Vertical(g3)
    c: Distance(g2) = 5
    c: DistanceX(g0,g-1) = 34
    c: DistanceY(g1,g1) = 40
    c: DistanceY(g1,g-1) = 10
FEATURE [PartDesign::Pad] Pad023
  Length = 54
  Length2 = 100
  Sketch = -> Sketch066
  Type = 0
FEATURE [PartDesign::Fillet] Fillet023
  Base = -> Pad023 [Edge73,Edge79,Edge54,Edge64]
  Radius = 4
FEATURE [Sketcher::SketchObject] Sketch067
  Placement = pos=(0,39,0) rot=(0,0.707107,0.707107;3.14159rad)
  Support = -> Fillet023 [Face17]
  sketch-geometry (4):
    g0: LineSegment StartX=-27.5 StartY=4 StartZ=0 EndX=27.5 EndY=4 EndZ=0
    g1: LineSegment StartX=27.5 StartY=4 StartZ=0 EndX=27.5 EndY=0 EndZ=0
    g2: LineSegment StartX=27.5 StartY=0 StartZ=0 EndX=-27.5 EndY=0 EndZ=0
    g3: LineSegment StartX=-27.5 StartY=0 StartZ=0 EndX=-27.5 EndY=4 EndZ=0
  constraints (12):
    c: Coincident(g0,g1)
    c: Coincident(g1,g2)
    c: Coincident(g2,g3)
    c: Coincident(g3,g0)
    c: Horizontal(g0)
    c: Horizontal(g2)
    c: Vertical(g1)
    c: Vertical(g3)
    c: DistanceY(g3,g3) = 4
    c: PointOnObject(g1,g-1)
    c: Distance(g2) = 55
    c: Symmetric(g1,g2,g-2)
FEATURE [PartDesign::Pad] Pad024
  Length = 80
  Length2 = 100
  Sketch = -> Sketch067
  Type = 0
FEATURE [PartDesign::Fillet] Fillet024
  Base = -> Pad024 [Edge17,Edge74]
  Radius = 5
FEATURE [PartDesign::Fillet] Fillet025
  Base = -> Fillet024 [Edge41,Edge8]
  Radius = 2
FEATURE [Sketcher::SketchObject] Sketch068
  Placement = pos=(0,0,0) rot=(1,0,0;3.14159rad)
  Support = -> Fillet025 [Face27]
  sketch-geometry (4):
    g0: LineSegment StartX=-18 StartY=-119 StartZ=0 EndX=-26 EndY=-119 EndZ=0
    g1: LineSegment StartX=-26 StartY=-119 StartZ=0 EndX=-26 EndY=-111 EndZ=0
    g2: LineSegment StartX=-18 StartY=-119 StartZ=0 EndX=-18 EndY=-111 EndZ=0
    g3: ArcOfCircle CenterX=-22 CenterY=-111 CenterZ=0 NormalX=0 NormalY=0 NormalZ=1 Radius=4 StartAngle=6.70092e-06 EndAngle=3.14159
  constraints (13):
    c: Horizontal(g0)
    c: Coincident(g1,g0)
    c: Vertical(g1)
    c: Coincident(g2,g0)
    c: Vertical(g2)
    c: Coincident(g3,g2)
    c: Coincident(g3,g1)
    c: Tangent(g3,g1)
    c: Distance(g0) = 8
    c: Distance(g2) = 8
    c: DistanceY(g0,g-1) = 119
    c: DistanceX(g0,g-1) = 18
    c: Tangent(g3,g2)
FEATURE [PartDesign::Pocket] Pocket028
  Length = 10
  Midplane = true
  Sketch = -> Sketch068
  Type = 0
FEATURE [Sketcher::SketchObject] Sketch070
  ExternalGeometry = -> [Extrude005]
  Placement = pos=(-35,0,1e-12) rot=(0.57735,-0.57735,-0.57735;2.0944rad)
  Support = -> Extrude005 [Face10]
  sketch-geometry (5):
    g0: ArcOfCircle CenterX=-50 CenterY=2.5 CenterZ=0 NormalX=0 NormalY=0 NormalZ=1 Radius=7.5 StartAngle=0 EndAngle=3.14159
    g1: ArcOfCircle CenterX=-50 CenterY=-2.5 CenterZ=0 NormalX=0 NormalY=0 NormalZ=1 Radius=7.5 StartAngle=3.14159 EndAngle=6.28319
    g2: LineSegment StartX=-57.5 StartY=2.5 StartZ=0 EndX=-57.5 EndY=-2.5 EndZ=0
    g3: LineSegment StartX=-42.5 StartY=2.5 StartZ=0 EndX=-42.5 EndY=-2.5 EndZ=0
    g4: LineSegment [constr] StartX=-50 StartY=10 StartZ=0 EndX=-50 EndY=-10 EndZ=0
  constraints (14):
    c: Tangent(g0,g3) = 1.5708
    c: Tangent(g0,g2) = -1.5708
    c: Tangent(g2,g1) = -1.5708
    c: Tangent(g3,g1) = 1.5708
    c: Vertical(g2)
    c: Equal(g0,g1)
    c: Distance(g0,g0) = 15
    c: PointOnObject(g4,g0)
    c: PointOnObject(g4,g1)
    c: PointOnObject(g1,g4)
    c: PointOnObject(g0,g4)
    c: Symmetric(g-3,g-3,g4)
    c: DistanceY(g4,g4) = 20
    c: DistanceY(g4,g-3) = 5
FEATURE [Sketcher::SketchObject] Sketch071
  ExternalGeometry = -> [Extrude005]
  Placement = pos=(0,0,15) rot=(0,0,1;0rad)
  Support = -> Extrude005 [Face1]
  sketch-geometry (1):
    g0: LineSegment StartX=-35 StartY=47.5 StartZ=0 EndX=-85 EndY=22.5 EndZ=0
  constraints (4):
    c: PointOnObject(g0,g-3)
    c: Distance(g0,g-3) = 12.5
    c: DistanceX(g0,g0) = 50
    c: DistanceY(g0,g0) = 25
FEATURE [Part::Sweep] Sweep
  Frenet = true
  Sections = -> [Sketch070]
  Solid = true
  Spine = -> Sketch071 [Edge1]
  Transition = 1
FEATURE [Part::MultiFuse] Fusion
  Shapes = -> [Extrude005,Sweep]
FEATURE [Part::Part2DObjectPython] Clone2D001  label="Clone of Sketch057 (2D)"  # Draft 2D object (typed FeaturePython)
  Objects = -> [Sketch057]
  Placement = pos=(-30,60,1e-12) rot=(0.57735,-0.57735,-0.57735;2.0944rad)
  Scale = (1,1,1)
FEATURE [Part::Extrusion] Extrude010
  Base = -> Clone2D001
  Dir = (100,0,0)
  Solid = true
FEATURE [Part::Cut] Cut
  Base = -> Pocket023
  Tool = -> Extrude010
FEATURE [Part::Cylinder] Cylinder
  Angle = 360
  Height = 20
  Placement = pos=(-85,25,-10) rot=(0,0,1;0rad)
  Radius = 10
FEATURE [PartDesign::Fillet] Fillet026
  Base = -> Cylinder [Edge3]
  Placement = pos=(-85,25,-10) rot=(0,0,1;0rad)
  Radius = 5
FEATURE [Part::MultiFuse] Fusion001
  Shapes = -> [Fillet026,Fusion]
FEATURE [Sketcher::SketchObject] Sketch072
  Placement = pos=(0,0,10) rot=(0,0,1;0rad)
  Support = -> Fusion001 [Face19]
  sketch-geometry (1):
    g0: Circle CenterX=-85 CenterY=25 CenterZ=0 NormalX=0 NormalY=0 NormalZ=1 Radius=2.5
  constraints (3):
    c: Radius(g0) = 2.5
    c: DistanceX(g0,g-1) = 85
    c: DistanceY(g-1,g0) = 25
FEATURE [PartDesign::Pocket] Pocket029
  Length = 2
  Sketch = -> Sketch072
  Type = 0
FEATURE [Sketcher::SketchObject] Sketch073
  Placement = pos=(0,0,10) rot=(0,0,1;0rad)
  Support = -> Pocket029 [Face19]
  sketch-geometry (7):
    g0: Circle CenterX=-85 CenterY=30.5 CenterZ=0 NormalX=0 NormalY=0 NormalZ=1 Radius=1.2
    g1: Circle [constr] CenterX=-85 CenterY=25 CenterZ=0 NormalX=0 NormalY=0 NormalZ=1 Radius=5.5
    g2: LineSegment [constr] StartX=-85 StartY=30.5 StartZ=0 EndX=-85 EndY=19.5 EndZ=0
    g3: LineSegment [constr] StartX=-79.5 StartY=25 StartZ=0 EndX=-90.5 EndY=25 EndZ=0
    g4: Circle CenterX=-79.5 CenterY=25 CenterZ=0 NormalX=0 NormalY=0 NormalZ=1 Radius=1.2
    g5: Circle CenterX=-90.5 CenterY=25 CenterZ=0 NormalX=0 NormalY=0 NormalZ=1 Radius=1.2
    g6: Circle CenterX=-85 CenterY=19.5 CenterZ=0 NormalX=0 NormalY=0 NormalZ=1 Radius=1.2
  constraints (19):
    c: Radius(g1) = 5.5
    c: PointOnObject(g0,g1)
    c: DistanceX(g1,g-1) = 85
    c: DistanceY(g-1,g1) = 25
    c: Coincident(g2,g0)
    c: PointOnObject(g2,g1)
    c: PointOnObject(g3,g1)
    c: PointOnObject(g3,g1)
    c: Horizontal(g3)
    c: PointOnObject(g1,g3)
    c: PointOnObject(g1,g2)
    c: Vertical(g2)
    c: Radius(g0) = 1.2
    c: Equal(g0,g4) = 1.2
    c: Equal(g0,g5) = 1.2
    c: Equal(g0,g6) = 1.2
    c: Coincident(g4,g3)
    c: Coincident(g5,g3)
    c: Coincident(g6,g2)
FEATURE [PartDesign::Pocket] Pocket030
  Length = 20
  Sketch = -> Sketch073
  Type = 0
FEATURE [Sketcher::SketchObject] Sketch074
  Placement = pos=(0,0,-10) rot=(1,0,0;3.14159rad)
  Support = -> Pocket030 [Face20]
  sketch-geometry (7):
    g0: Circle [constr] CenterX=-85 CenterY=-25 CenterZ=0 NormalX=0 NormalY=0 NormalZ=1 Radius=5.5
    g1: LineSegment [constr] StartX=-85 StartY=-19.5 StartZ=0 EndX=-85 EndY=-30.5 EndZ=0
    g2: LineSegment [constr] StartX=-90.5 StartY=-25 StartZ=0 EndX=-79.5 EndY=-25 EndZ=0
    g3: Circle CenterX=-79.5 CenterY=-25 CenterZ=0 NormalX=0 NormalY=0 NormalZ=1 Radius=2.25
    g4: Circle CenterX=-85 CenterY=-30.5 CenterZ=0 NormalX=0 NormalY=0 NormalZ=1 Radius=2.25
    g5: Circle CenterX=-90.5 CenterY=-25 CenterZ=0 NormalX=0 NormalY=0 NormalZ=1 Radius=2.25
    g6: Circle CenterX=-85 CenterY=-19.5 CenterZ=0 NormalX=0 NormalY=0 NormalZ=1 Radius=2.25
  constraints (19):
    c: PointOnObject(g1,g0)
    c: PointOnObject(g2,g0)
    c: Horizontal(g2)
    c: PointOnObject(g0,g1)
    c: PointOnObject(g0,g2)
    c: Radius(g0) = 5.5
    c: Coincident(g3,g2)
    c: Radius(g3) = 2.25
    c: Equal(g3,g4) = 2.25
    c: Equal(g3,g5) = 2.25
    c: Equal(g3,g6) = 2.25
    c: Coincident(g2,g5)
    c: PointOnObject(g2,g0)
    c: PointOnObject(g1,g0)
    c: Coincident(g6,g1)
    c: Vertical(g1)
    c: Coincident(g1,g4)
    c: DistanceX(g0,g-1) = 85
    c: DistanceY(g0,g-1) = 25
FEATURE [PartDesign::Pocket] Pocket031
  Length = 18
  Sketch = -> Sketch074
  Type = 0
FEATURE [Sketcher::SketchObject] Sketch075
  Placement = pos=(-30,60,1e-12) rot=(-0.164647,0.697457,0.697457;3.46796rad)
  Support = -> Pocket031 [Face14]
  sketch-geometry (4):
    g0: LineSegment StartX=10 StartY=6.5 StartZ=0 EndX=45 EndY=6.5 EndZ=0
    g1: LineSegment StartX=45 StartY=6.5 StartZ=0 EndX=45 EndY=-6.5 EndZ=0
    g2: LineSegment StartX=45 StartY=-6.5 StartZ=0 EndX=10 EndY=-6.5 EndZ=0
    g3: LineSegment StartX=10 StartY=-6.5 StartZ=0 EndX=10 EndY=6.5 EndZ=0
  constraints (12):
    c: Coincident(g0,g1)
    c: Coincident(g1,g2)
    c: Coincident(g2,g3)
    c: Coincident(g3,g0)
    c: Horizontal(g0)
    c: Horizontal(g2)
    c: Vertical(g1)
    c: Vertical(g3)
    c: Distance(g3) = 13
    c: DistanceX(g0,g0) = 35
    c: Symmetric(g0,g1,g-1)
    c: DistanceX(g-1,g0) = 10
FEATURE [PartDesign::Pocket] Pocket032
  Length = 3
  Sketch = -> Sketch075
  Type = 0
FEATURE [Sketcher::SketchObject] Sketch076
  Placement = pos=(-30,60,1e-12) rot=(-0.164647,0.697457,0.697457;3.46796rad)
  Support = -> Pocket032 [Face14]
  sketch-geometry (4):
    g0: LineSegment StartX=0 StartY=-2.5 StartZ=0 EndX=10 EndY=-2.5 EndZ=0
    g1: LineSegment StartX=10 StartY=-2.5 StartZ=0 EndX=10 EndY=-6.5 EndZ=0
    g2: LineSegment StartX=10 StartY=-6.5 StartZ=0 EndX=0 EndY=-6.5 EndZ=0
    g3: LineSegment StartX=0 StartY=-6.5 StartZ=0 EndX=0 EndY=-2.5 EndZ=0
  constraints (12):
    c: Coincident(g0,g1)
    c: Coincident(g1,g2)
    c: Coincident(g2,g3)
    c: Coincident(g3,g0)
    c: Horizontal(g0)
    c: Horizontal(g2)
    c: Vertical(g1)
    c: Vertical(g3)
    c: PointOnObject(g0,g-2)
    c: Distance(g0) = 10
    c: DistanceY(g1,g1) = 4
    c: DistanceY(g0,g-1) = 2.5
FEATURE [PartDesign::Pocket] Pocket033  label="arm_rf"
  Length = 5
  Midplane = true
  Sketch = -> Sketch076
  Type = 0
FEATURE [Sketcher::SketchObject] Sketch077
  Placement = pos=(-30,0,1e-12) rot=(0.57735,-0.57735,-0.57735;2.0944rad)
  Support = -> Cut [Face31]
  sketch-geometry (9):
    g0: ArcOfCircle CenterX=-68 CenterY=-4.5 CenterZ=0 NormalX=0 NormalY=0 NormalZ=1 Radius=1.5 StartAngle=1.5708 EndAngle=4.71239
    g1: ArcOfCircle CenterX=-59 CenterY=-4.5 CenterZ=0 NormalX=0 NormalY=0 NormalZ=1 Radius=1.5 StartAngle=4.71239 EndAngle=7.85398
    g2: LineSegment StartX=-68 StartY=-6 StartZ=0 EndX=-59 EndY=-6 EndZ=0
    g3: LineSegment StartX=-68 StartY=-3 StartZ=0 EndX=-59 EndY=-3 EndZ=0
    g4: ArcOfCircle CenterX=-101 CenterY=-4.5 CenterZ=0 NormalX=0 NormalY=0 NormalZ=1 Radius=1.5 StartAngle=1.5708 EndAngle=4.71239
    g5: ArcOfCircle CenterX=-92 CenterY=-4.5 CenterZ=0 NormalX=0 NormalY=0 NormalZ=1 Radius=1.5 StartAngle=4.71239 EndAngle=7.85398
    g6: LineSegment StartX=-101 StartY=-6 StartZ=0 EndX=-92 EndY=-6 EndZ=0
    g7: LineSegment StartX=-101 StartY=-3 StartZ=0 EndX=-92 EndY=-3 EndZ=0
    g8: LineSegment [constr] StartX=-92 StartY=-4.5 StartZ=0 EndX=-68 EndY=-4.5 EndZ=0
  constraints (22):
    c: Tangent(g0,g3) = 1.5708
    c: Tangent(g0,g2) = -1.5708
    c: Tangent(g2,g1) = -1.5708
    c: Tangent(g3,g1) = 1.5708
    c: Horizontal(g2)
    c: Equal(g0,g1)
    c: DistanceY(g0,g0) = 3
    c: Distance(g3) = 9
    c: DistanceX(g1,g-1) = 59
    c: DistanceY(g1,g-1) = 3
    c: Tangent(g4,g7) = 1.5708
    c: Tangent(g4,g6) = -1.5708
    c: Tangent(g6,g5) = -1.5708
    c: Tangent(g7,g5) = 1.5708
    c: Horizontal(g6)
    c: Equal(g4,g5)
    c: Equal(g0,g4) = 3
    c: Equal(g3,g7) = 9
    c: Coincident(g8,g5)
    c: Coincident(g0,g8)
    c: Horizontal(g8)
    c: DistanceX(g8,g8) = 24
FEATURE [Part::FeaturePython] Clone  label="Clone of arm"  # Draft clone (typed FeaturePython)
  Objects = -> [Pocket033]
  Scale = (1,1,1)
FEATURE [Part::Mirroring] Part__Mirroring  label="arm_rr"
  Base = (0,0,0)
  Normal = (0,1,0)
  Placement = pos=(0,160,0) rot=(0,0,1;0rad)
  Source = -> Clone
FEATURE [PartDesign::Pocket] Pocket034
  Length = 100
  Sketch = -> Sketch077
  Type = 0
FEATURE [Part::FeaturePython] Clone001  label="Clone of arm_rf"  # Draft clone (typed FeaturePython)
  Objects = -> [Pocket033]
  Scale = (1,1,1)
FEATURE [Part::FeaturePython] Clone002  label="Clone of arm_rr"  # Draft clone (typed FeaturePython)
  Objects = -> [Part__Mirroring]
  Placement = pos=(0,160,0) rot=(0,0,1;0rad)
  Scale = (1,1,1)
FEATURE [Part::Mirroring] Part__Mirroring001  label="arm_lf"
  Base = (0,37.5069,1e-12)
  Normal = (1,0,-1.19209e-07)
  Source = -> Clone001
FEATURE [Part::Mirroring] Part__Mirroring002  label="arm_lr"
  Base = (0,0,0)
  Normal = (1,0,0)
  Source = -> Clone002
FEATURE [Sketcher::SketchObject] Sketch078
  Placement = pos=(30,0,0) rot=(0.57735,0.57735,0.57735;2.0944rad)
  Support = -> Pocket034 [Face41]
  sketch-geometry (8):
    g0: LineSegment StartX=62.5 StartY=-8 StartZ=0 EndX=71.5 EndY=-8 EndZ=0
    g1: LineSegment StartX=72.5 StartY=-9 StartZ=0 EndX=72.5 EndY=-17 EndZ=0
    g2: LineSegment StartX=71.5 StartY=-18 StartZ=0 EndX=62.5 EndY=-18 EndZ=0
    g3: LineSegment StartX=61.5 StartY=-17 StartZ=0 EndX=61.5 EndY=-9 EndZ=0
    g4: ArcOfCircle CenterX=62.5 CenterY=-9 CenterZ=0 NormalX=0 NormalY=0 NormalZ=1 Radius=1 StartAngle=1.5708 EndAngle=3.14159
    g5: ArcOfCircle CenterX=71.5 CenterY=-9 CenterZ=0 NormalX=0 NormalY=0 NormalZ=1 Radius=1 StartAngle=0 EndAngle=1.5708
    g6: ArcOfCircle CenterX=71.5 CenterY=-17 CenterZ=0 NormalX=0 NormalY=0 NormalZ=1 Radius=1 StartAngle=4.71239 EndAngle=6.28319
    g7: ArcOfCircle CenterX=62.5 CenterY=-17 CenterZ=0 NormalX=0 NormalY=0 NormalZ=1 Radius=1 StartAngle=3.14159 EndAngle=4.71239
  constraints (20):
    c: Horizontal(g0)
    c: Horizontal(g2)
    c: Vertical(g1)
    c: Vertical(g3)
    c: Tangent(g0,g4) = 1.5708
    c: Tangent(g3,g4) = 1.5708
    c: Tangent(g0,g5) = 1.5708
    c: Tangent(g1,g5) = 1.5708
    c: Tangent(g1,g6) = 1.5708
    c: Tangent(g2,g6) = 1.5708
    c: Tangent(g3,g7) = 1.5708
    c: Tangent(g2,g7) = 1.5708
    c: Radius(g7) = 1
    c: Radius(g4) = 1
    c: Radius(g5) = 1
    c: Radius(g6) = 1
    c: DistanceY(g2,g0) = 10
    c: DistanceX(g3,g1) = 11
    c: DistanceX(g-1,g3) = 61.5
    c: DistanceY(g3,g-1) = 17
FEATURE [PartDesign::Pocket] Pocket035
  Length = 5
  Sketch = -> Sketch078
  Type = 0
FEATURE [Sketcher::SketchObject] Sketch079
  Placement = pos=(-27,0,0) rot=(0.57735,0.57735,0.57735;2.0944rad)
  Support = -> Pocket035 [Face1]
  sketch-geometry (60):
    g0: LineSegment StartX=116.5 StartY=17.1003 StartZ=0 EndX=111.65 EndY=14.3001 EndZ=0
    g1: LineSegment StartX=111.65 StartY=14.3001 StartZ=0 EndX=111.65 EndY=8.69985 EndZ=0
    g2: LineSegment StartX=111.65 StartY=8.69985 StartZ=0 EndX=116.5 EndY=5.8997 EndZ=0
    g3: LineSegment StartX=116.5 StartY=5.8997 StartZ=0 EndX=121.35 EndY=8.69985 EndZ=0
    g4: LineSegment StartX=121.35 StartY=8.69985 StartZ=0 EndX=121.35 EndY=14.3001 EndZ=0
    g5: LineSegment StartX=121.35 StartY=14.3001 StartZ=0 EndX=116.5 EndY=17.1003 EndZ=0
    g6: Circle [constr] CenterX=116.5 CenterY=11.5 CenterZ=0 NormalX=0 NormalY=0 NormalZ=1 Radius=5.6003
    g7: LineSegment StartX=116.5 StartY=14.7909 StartZ=0 EndX=113.65 EndY=13.1454 EndZ=0
    g8: LineSegment StartX=113.65 StartY=13.1454 StartZ=0 EndX=113.65 EndY=9.85455 EndZ=0
    g9: LineSegment StartX=113.65 StartY=9.85455 StartZ=0 EndX=116.5 EndY=8.2091 EndZ=0
    g10: LineSegment StartX=116.5 StartY=8.2091 StartZ=0 EndX=119.35 EndY=9.85455 EndZ=0
    g11: LineSegment StartX=119.35 StartY=9.85455 StartZ=0 EndX=119.35 EndY=13.1454 EndZ=0
    g12: LineSegment StartX=119.35 StartY=13.1454 StartZ=0 EndX=116.5 EndY=14.7909 EndZ=0
    g13: Circle [constr] CenterX=116.5 CenterY=11.5 CenterZ=0 NormalX=0 NormalY=0 NormalZ=1 Radius=3.2909
    g14: LineSegment StartX=103.5 StartY=17.1003 StartZ=0 EndX=98.65 EndY=14.3001 EndZ=0
    g15: LineSegment StartX=98.65 StartY=14.3001 StartZ=0 EndX=98.65 EndY=8.69985 EndZ=0
    g16: LineSegment StartX=98.65 StartY=8.69985 StartZ=0 EndX=103.5 EndY=5.8997 EndZ=0
    g17: LineSegment StartX=103.5 StartY=5.8997 StartZ=0 EndX=108.35 EndY=8.69985 EndZ=0
    g18: LineSegment StartX=108.35 StartY=8.69985 StartZ=0 EndX=108.35 EndY=14.3001 EndZ=0
    g19: LineSegment StartX=108.35 StartY=14.3001 StartZ=0 EndX=103.5 EndY=17.1003 EndZ=0
    g20: Circle [constr] CenterX=103.5 CenterY=11.5 CenterZ=0 NormalX=0 NormalY=0 NormalZ=1 Radius=5.6003
    g21: LineSegment StartX=103.5 StartY=14.7909 StartZ=0 EndX=100.65 EndY=13.1454 EndZ=0
    g22: LineSegment StartX=100.65 StartY=13.1454 StartZ=0 EndX=100.65 EndY=9.85455 EndZ=0
    g23: LineSegment StartX=100.65 StartY=9.85455 StartZ=0 EndX=103.5 EndY=8.2091 EndZ=0
    g24: LineSegment StartX=103.5 StartY=8.2091 StartZ=0 EndX=106.35 EndY=9.85455 EndZ=0
    g25: LineSegment StartX=106.35 StartY=9.85455 StartZ=0 EndX=106.35 EndY=13.1454 EndZ=0
    g26: LineSegment StartX=106.35 StartY=13.1454 StartZ=0 EndX=103.5 EndY=14.7909 EndZ=0
    g27: Circle [constr] CenterX=103.5 CenterY=11.5 CenterZ=0 NormalX=0 NormalY=0 NormalZ=1 Radius=3.2909
    g28: LineSegment StartX=116.5 StartY=-5.8997 StartZ=0 EndX=111.65 EndY=-8.69985 EndZ=0
    g29: LineSegment StartX=111.65 StartY=-8.69985 StartZ=0 EndX=111.65 EndY=-14.3001 EndZ=0
    g30: LineSegment StartX=111.65 StartY=-14.3001 StartZ=0 EndX=116.5 EndY=-17.1003 EndZ=0
    g31: LineSegment StartX=116.5 StartY=-17.1003 StartZ=0 EndX=121.35 EndY=-14.3001 EndZ=0
    g32: LineSegment StartX=121.35 StartY=-14.3001 StartZ=0 EndX=121.35 EndY=-8.69985 EndZ=0
    g33: LineSegment StartX=121.35 StartY=-8.69985 StartZ=0 EndX=116.5 EndY=-5.8997 EndZ=0
    g34: Circle [constr] CenterX=116.5 CenterY=-11.5 CenterZ=0 NormalX=0 NormalY=0 NormalZ=1 Radius=5.6003
    g35: LineSegment StartX=116.5 StartY=-8.2091 StartZ=0 EndX=113.65 EndY=-9.85455 EndZ=0
    g36: LineSegment StartX=113.65 StartY=-9.85455 StartZ=0 EndX=113.65 EndY=-13.1454 EndZ=0
    g37: LineSegment StartX=113.65 StartY=-13.1454 StartZ=0 EndX=116.5 EndY=-14.7909 EndZ=0
    g38: LineSegment StartX=116.5 StartY=-14.7909 StartZ=0 EndX=119.35 EndY=-13.1454 EndZ=0
    g39: LineSegment StartX=119.35 StartY=-13.1454 StartZ=0 EndX=119.35 EndY=-9.85455 EndZ=0
    g40: LineSegment StartX=119.35 StartY=-9.85455 StartZ=0 EndX=116.5 EndY=-8.2091 EndZ=0
    g41: Circle [constr] CenterX=116.5 CenterY=-11.5 CenterZ=0 NormalX=0 NormalY=0 NormalZ=1 Radius=3.2909
    g42: LineSegment StartX=103.5 StartY=-5.8997 StartZ=0 EndX=98.65 EndY=-8.69985 EndZ=0
    g43: LineSegment StartX=98.65 StartY=-8.69985 StartZ=0 EndX=98.65 EndY=-14.3001 EndZ=0
    g44: LineSegment StartX=98.65 StartY=-14.3001 StartZ=0 EndX=103.5 EndY=-17.1003 EndZ=0
    g45: LineSegment StartX=103.5 StartY=-17.1003 StartZ=0 EndX=108.35 EndY=-14.3001 EndZ=0
    g46: LineSegment StartX=108.35 StartY=-14.3001 StartZ=0 EndX=108.35 EndY=-8.69985 EndZ=0
    g47: LineSegment StartX=108.35 StartY=-8.69985 StartZ=0 EndX=103.5 EndY=-5.8997 EndZ=0
    g48: Circle [constr] CenterX=103.5 CenterY=-11.5 CenterZ=0 NormalX=0 NormalY=0 NormalZ=1 Radius=5.6003
    g49: LineSegment StartX=103.5 StartY=-8.2091 StartZ=0 EndX=100.65 EndY=-9.85455 EndZ=0
    g50: LineSegment StartX=100.65 StartY=-9.85455 StartZ=0 EndX=100.65 EndY=-13.1454 EndZ=0
    g51: LineSegment StartX=100.65 StartY=-13.1454 StartZ=0 EndX=103.5 EndY=-14.7909 EndZ=0
    g52: LineSegment StartX=103.5 StartY=-14.7909 StartZ=0 EndX=106.35 EndY=-13.1454 EndZ=0
    g53: LineSegment StartX=106.35 StartY=-13.1454 StartZ=0 EndX=106.35 EndY=-9.85455 EndZ=0
    g54: LineSegment StartX=106.35 StartY=-9.85455 StartZ=0 EndX=103.5 EndY=-8.2091 EndZ=0
    g55: Circle [constr] CenterX=103.5 CenterY=-11.5 CenterZ=0 NormalX=0 NormalY=0 NormalZ=1 Radius=3.2909
    g56: LineSegment [constr] StartX=116.5 StartY=11.5 StartZ=0 EndX=116.5 EndY=-11.5 EndZ=0
    g57: LineSegment [constr] StartX=103.5 StartY=11.5 StartZ=0 EndX=103.5 EndY=-11.5 EndZ=0
    g58: LineSegment [constr] StartX=103.5 StartY=11.5 StartZ=0 EndX=116.5 EndY=11.5 EndZ=0
    g59: LineSegment [constr] StartX=103.5 StartY=-11.5 StartZ=0 EndX=116.5 EndY=-11.5 EndZ=0
  constraints (140):
    c: Coincident(g0,g1)
    c: Coincident(g1,g2)
    c: Coincident(g2,g3)
    c: Coincident(g3,g4)
    c: Coincident(g4,g5)
    c: Coincident(g5,g0)
    c: Equal(g0, g1-g5) x5
    c: PointOnObject(g0,g6)
    c: PointOnObject(g1,g6)
    c: PointOnObject(g2,g6)
    c: PointOnObject(g3,g6)
    c: PointOnObject(g4,g6)
    c: PointOnObject(g5,g6)
    c: Coincident(g7,g8)
    c: Coincident(g8,g9)
    c: Coincident(g9,g10)
    c: Coincident(g10,g11)
    c: Coincident(g11,g12)
    c: Coincident(g12,g7)
    c: Equal(g7, g8-g12) x5
    c: PointOnObject(g7,g13)
    c: PointOnObject(g8,g13)
    c: PointOnObject(g9,g13)
    c: PointOnObject(g10,g13)
    c: PointOnObject(g11,g13)
    c: PointOnObject(g12,g13)
    c: Distance(g7,g11) = 5.7
    c: Vertical(g11)
    c: Coincident(g6,g13)
    c: Vertical(g1)
    c: DistanceX(g1,g8) = 2
    c: DistanceX(g-1,g6) = 116.5
    c: DistanceY(g-1,g6) = 11.5
    c: Coincident(g14,g15)
    c: Coincident(g15,g16)
    c: Coincident(g16,g17)
    c: Coincident(g17,g18)
    c: Coincident(g18,g19)
    c: Coincident(g19,g14)
    c: Equal(g14, g15-g19) x5
    c: PointOnObject(g14,g20)
    c: PointOnObject(g15,g20)
    c: PointOnObject(g16,g20)
    c: PointOnObject(g17,g20)
    c: PointOnObject(g18,g20)
    c: PointOnObject(g19,g20)
    c: Coincident(g21,g22)
    c: Coincident(g22,g23)
    c: Coincident(g23,g24)
    c: Coincident(g24,g25)
    c: Coincident(g25,g26)
    c: Coincident(g26,g21)
    c: Equal(g21, g22-g26) x5
    c: PointOnObject(g21,g27)
    c: PointOnObject(g22,g27)
    c: PointOnObject(g23,g27)
    c: PointOnObject(g24,g27)
    c: PointOnObject(g25,g27)
    c: PointOnObject(g26,g27)
    c: Distance(g21,g25) = 5.7
    c: Vertical(g25)
    c: Coincident(g20,g27)
    c: Vertical(g15)
    c: DistanceX(g15,g22) = 2
    c: Coincident(g28,g29)
    c: Coincident(g29,g30)
    c: Coincident(g30,g31)
    c: Coincident(g31,g32)
    c: Coincident(g32,g33)
    c: Coincident(g33,g28)
    c: Equal(g28, g29-g33) x5
    c: PointOnObject(g28,g34)
    c: PointOnObject(g29,g34)
    c: PointOnObject(g30,g34)
    c: PointOnObject(g31,g34)
    c: PointOnObject(g32,g34)
    c: PointOnObject(g33,g34)
    c: Coincident(g35,g36)
    c: Coincident(g36,g37)
    c: Coincident(g37,g38)
    c: Coincident(g38,g39)
    c: Coincident(g39,g40)
    c: Coincident(g40,g35)
    c: Equal(g35, g36-g40) x5
    c: PointOnObject(g35,g41)
    c: PointOnObject(g36,g41)
    c: PointOnObject(g37,g41)
    c: PointOnObject(g38,g41)
    c: PointOnObject(g39,g41)
    c: PointOnObject(g40,g41)
    c: Distance(g35,g39) = 5.7
    c: Vertical(g39)
    c: Coincident(g34,g41)
    c: Vertical(g29)
    c: DistanceX(g29,g36) = 2
    c: Coincident(g42,g43)
    c: Coincident(g43,g44)
    c: Coincident(g44,g45)
    c: Coincident(g45,g46)
    c: Coincident(g46,g47)
    c: Coincident(g47,g42)
    c: Equal(g42, g43-g47) x5
    c: PointOnObject(g42,g48)
    c: PointOnObject(g43,g48)
    c: PointOnObject(g44,g48)
    c: PointOnObject(g45,g48)
    c: PointOnObject(g46,g48)
    c: PointOnObject(g47,g48)
    c: Coincident(g49,g50)
    c: Coincident(g50,g51)
    c: Coincident(g51,g52)
    c: Coincident(g52,g53)
    c: Coincident(g53,g54)
    c: Coincident(g54,g49)
    c: Equal(g49, g50-g54) x5
    c: PointOnObject(g49,g55)
    c: PointOnObject(g50,g55)
    c: PointOnObject(g51,g55)
    c: PointOnObject(g52,g55)
    c: PointOnObject(g53,g55)
    c: PointOnObject(g54,g55)
    c: Distance(g49,g53) = 5.7
    c: Vertical(g53)
    c: Coincident(g48,g55)
    c: Vertical(g43)
    c: DistanceX(g43,g50) = 2
    c: Coincident(g56,g6)
    c: Coincident(g56,g34)
    c: Vertical(g56)
    c: Coincident(g57,g20)
    c: Coincident(g57,g48)
    c: Vertical(g57)
    c: Coincident(g58,g6)
    c: Horizontal(g58)
    c: Coincident(g59,g48)
    c: Coincident(g59,g34)
    c: Horizontal(g59)
    c: Coincident(g20,g58)
    c: Distance(g58) = 13
    c: Distance(g56) = 23
FEATURE [Part::Extrusion] Extrude013
  Base = -> Sketch079
  Dir = (3,0,0)
  Solid = true
FEATURE [Part::FeaturePython] Clone003  label="Clone of Extrude013"  # Draft clone (typed FeaturePython)
  Objects = -> [Extrude013]
  Placement = pos=(0,-60,0) rot=(0,0,1;0rad)
  Scale = (1,1,1)
FEATURE [Part::MultiFuse] Fusion002  label="nut_holes"
  Shapes = -> [Extrude013,Clone003]
FEATURE [Sketcher::SketchObject] Sketch080
  Placement = pos=(-27,0,0) rot=(0.57735,0.57735,0.57735;2.0944rad)
  Support = -> Pocket035 [Face1]
  sketch-geometry (4):
    g0: LineSegment StartX=120 StartY=20 StartZ=0 EndX=130 EndY=20 EndZ=0
    g1: LineSegment StartX=130 StartY=20 StartZ=0 EndX=130 EndY=-20 EndZ=0
    g2: LineSegment StartX=130 StartY=-20 StartZ=0 EndX=120 EndY=-20 EndZ=0
    g3: LineSegment StartX=120 StartY=-20 StartZ=0 EndX=120 EndY=20 EndZ=0
  constraints (12):
    c: Coincident(g0,g1)
    c: Coincident(g1,g2)
    c: Coincident(g2,g3)
    c: Coincident(g3,g0)
    c: Horizontal(g0)
    c: Horizontal(g2)
    c: Vertical(g1)
    c: Vertical(g3)
    c: DistanceX(g-1,g0) = 120
    c: DistanceX(g0,g0) = 10
    c: DistanceY(g1,g1) = 40
    c: Symmetric(g0,g1,g-1)
FEATURE [Part::Extrusion] Extrude015
  Base = -> Sketch080
  Dir = (5,0,0)
  Solid = true
FEATURE [Part::Cut] Cut001  label="nut_holes_cut"
  Base = -> Fusion002
  Tool = -> Extrude015
FEATURE [Part::FeaturePython] Clone004  label="Clone of nut_holes_cut"  # Draft clone (typed FeaturePython)
  Objects = -> [Cut001]
  Scale = (1,1,1)
FEATURE [Part::Mirroring] Part__Mirroring003  label="Clone of nut_holes_cut (Mirror #4)"
  Base = (0,0,0)
  Normal = (1,0,0)
  Source = -> Clone004
FEATURE [Sketcher::SketchObject] Sketch081
  Placement = pos=(0,0,0) rot=(1,0,0;3.14159rad)
  Support = -> Pocket035 [Face55]
  sketch-geometry (8):
    g0: Circle CenterX=-15.2 CenterY=-51.7 CenterZ=0 NormalX=0 NormalY=0 NormalZ=1 Radius=1.7
    g1: Circle CenterX=15.3 CenterY=-51.7 CenterZ=0 NormalX=0 NormalY=0 NormalZ=1 Radius=1.7
    g2: Circle CenterX=-15.2 CenterY=-82.2 CenterZ=0 NormalX=0 NormalY=0 NormalZ=1 Radius=1.7
    g3: Circle CenterX=15.3 CenterY=-82.2 CenterZ=0 NormalX=0 NormalY=0 NormalZ=1 Radius=1.7
    g4: LineSegment [constr] StartX=-15.2 StartY=-51.7 StartZ=0 EndX=15.3 EndY=-51.7 EndZ=0
    g5: LineSegment [constr] StartX=-15.2 StartY=-51.7 StartZ=0 EndX=-15.2 EndY=-82.2 EndZ=0
    g6: LineSegment [constr] StartX=-15.2 StartY=-82.2 StartZ=0 EndX=15.3 EndY=-82.2 EndZ=0
    g7: LineSegment [constr] StartX=15.3 StartY=-82.2 StartZ=0 EndX=15.3 EndY=-51.7 EndZ=0
  constraints (20):
    c: Radius(g0) = 1.7
    c: DistanceX(g0,g-1) = 15.2
    c: DistanceY(g0,g-1) = 51.7
    c: Equal(g0,g1) = 1.7
    c: Equal(g0,g2) = 1.7
    c: Equal(g0,g3) = 1.7
    c: Coincident(g4,g0)
    c: Horizontal(g4)
    c: Coincident(g1,g4)
    c: Vertical(g5)
    c: Coincident(g2,g5)
    c: Coincident(g0,g5)
    c: Horizontal(g6)
    c: Vertical(g7)
    c: Coincident(g1,g7)
    c: Coincident(g3,g6)
    c: Coincident(g3,g7)
    c: Coincident(g2,g6)
    c: Distance(g5) = 30.5
    c: Distance(g6) = 30.5
FEATURE [PartDesign::Pocket] Pocket036
  Length = 5
  Sketch = -> Sketch081
  Type = 0
FEATURE [Part::MultiFuse] Fusion003
  Shapes = -> [Cut001,Part__Mirroring003,Pocket036]
FEATURE [Sketcher::SketchObject] Sketch082
  ExternalGeometry = -> [Fusion003]
  Placement = pos=(0,120,0) rot=(0,0.707107,0.707107;3.14159rad)
  Support = -> Fusion003 [Face12]
  sketch-geometry (15):
    g0: LineSegment [constr] StartX=-20.15 StartY=21.3546 StartZ=0 EndX=-20.15 EndY=24.6454 EndZ=0
    g1: LineSegment [constr] StartX=-20.15 StartY=24.6454 StartZ=0 EndX=-23 EndY=26.2909 EndZ=0
    g2: LineSegment [constr] StartX=-23 StartY=26.2909 StartZ=0 EndX=-25.85 EndY=24.6454 EndZ=0
    g3: LineSegment [constr] StartX=-25.85 StartY=24.6454 StartZ=0 EndX=-25.85 EndY=21.3546 EndZ=0
    g4: LineSegment [constr] StartX=-25.85 StartY=21.3546 StartZ=0 EndX=-23 EndY=19.7091 EndZ=0
    g5: LineSegment [constr] StartX=-23 StartY=19.7091 StartZ=0 EndX=-20.15 EndY=21.3546 EndZ=0
    g6: Circle [constr] CenterX=-23 CenterY=23 CenterZ=0 NormalX=0 NormalY=0 NormalZ=1 Radius=3.2909
    g7: LineSegment StartX=-25 StartY=28 StartZ=0 EndX=-21 EndY=28 EndZ=0
    g8: LineSegment StartX=-19 StartY=26 StartZ=0 EndX=-19 EndY=20 EndZ=0
    g9: LineSegment StartX=-27 StartY=18 StartZ=0 EndX=-21 EndY=18 EndZ=0
    g10: ArcOfCircle CenterX=-21 CenterY=26 CenterZ=0 NormalX=0 NormalY=0 NormalZ=1 Radius=2 StartAngle=0 EndAngle=1.5708
    g11: ArcOfCircle CenterX=-21 CenterY=20 CenterZ=0 NormalX=0 NormalY=0 NormalZ=1 Radius=2 StartAngle=4.71239 EndAngle=6.28319
    g12: LineSegment [constr] StartX=-23 StartY=23 StartZ=0 EndX=-20.15 EndY=23 EndZ=0
    g13: LineSegment StartX=-27 StartY=20 StartZ=0 EndX=-27 EndY=18 EndZ=0
    g14: ArcOfCircle CenterX=-10 CenterY=20 CenterZ=0 NormalX=0 NormalY=0 NormalZ=1 Radius=17 StartAngle=2.65164 EndAngle=3.14159
  constraints (39):
    c: Coincident(g0,g1)
    c: Coincident(g1,g2)
    c: Coincident(g2,g3)
    c: Coincident(g3,g4)
    c: Coincident(g4,g5)
    c: Coincident(g5,g0)
    c: Equal(g0, g1-g5) x5
    c: PointOnObject(g0,g6)
    c: PointOnObject(g1,g6)
    c: PointOnObject(g2,g6)
    c: PointOnObject(g3,g6)
    c: PointOnObject(g4,g6)
    c: PointOnObject(g5,g6)
    c: Vertical(g0)
    c: Distance(g2,g0) = 5.7
    c: DistanceX(g6,g-1) = 23
    c: DistanceY(g-1,g6) = 23
    c: PointOnObject(g7,g-3)
    c: Horizontal(g7)
    c: Vertical(g8)
    c: Horizontal(g9)
    c: Tangent(g7,g10) = 1.5708
    c: Tangent(g8,g10) = 1.5708
    c: Tangent(g8,g11) = 1.5708
    c: Tangent(g9,g11) = -1.5708
    c: Radius(g11) = 2
    c: Equal(g10,g11)
    c: DistanceX(g9,g8) = 8
    c: DistanceY(g9,g7) = 10
    c: Coincident(g12,g6)
    c: Horizontal(g12)
    c: PointOnObject(g12,g0)
    c: Symmetric(g9,g7,g12)
    c: Coincident(g13,g-3)
    c: Coincident(g13,g9)
    c: Vertical(g13)
    c: Coincident(g14,g-3)
    c: Coincident(g14,g13)
    c: Coincident(g14,g7)
FEATURE [Part::Extrusion] Extrude018
  Base = -> Sketch082
  Dir = (0,-10,0)
  Solid = true
FEATURE [Sketcher::SketchObject] Sketch083
  Placement = pos=(0,120,0) rot=(0,0.707107,0.707107;3.14159rad)
  Support = -> Extrude018 [Face8]
  sketch-geometry (1):
    g0: Circle CenterX=-23 CenterY=23 CenterZ=0 NormalX=0 NormalY=0 NormalZ=1 Radius=1.7
  constraints (3):
    c: Radius(g0) = 1.7
    c: DistanceY(g-1,g0) = 23
    c: DistanceX(g0,g-1) = 23
FEATURE [PartDesign::Pocket] Pocket037
  Length = 10
  Sketch = -> Sketch083
  Type = 0
FEATURE [Sketcher::SketchObject] Sketch084
  Placement = pos=(0,110,0) rot=(1,0,0;1.5708rad)
  Support = -> Pocket037 [Face5]
  sketch-geometry (7):
    g0: LineSegment StartX=25.85 StartY=24.6454 StartZ=0 EndX=23 EndY=26.2909 EndZ=0
    g1: LineSegment StartX=23 StartY=26.2909 StartZ=0 EndX=20.15 EndY=24.6454 EndZ=0
    g2: LineSegment StartX=20.15 StartY=24.6454 StartZ=0 EndX=20.15 EndY=21.3546 EndZ=0
    g3: LineSegment StartX=20.15 StartY=21.3546 StartZ=0 EndX=23 EndY=19.7091 EndZ=0
    g4: LineSegment StartX=23 StartY=19.7091 StartZ=0 EndX=25.85 EndY=21.3546 EndZ=0
    g5: LineSegment StartX=25.85 StartY=21.3546 StartZ=0 EndX=25.85 EndY=24.6454 EndZ=0
    g6: Circle [constr] CenterX=23 CenterY=23 CenterZ=0 NormalX=0 NormalY=0 NormalZ=1 Radius=3.2909
  constraints (17):
    c: Coincident(g0,g1)
    c: Coincident(g1,g2)
    c: Coincident(g2,g3)
    c: Coincident(g3,g4)
    c: Coincident(g4,g5)
    c: Coincident(g5,g0)
    c: Equal(g0, g1-g5) x5
    c: PointOnObject(g0,g6)
    c: PointOnObject(g1,g6)
    c: PointOnObject(g2,g6)
    c: PointOnObject(g3,g6)
    c: PointOnObject(g4,g6)
    c: PointOnObject(g5,g6)
    c: Vertical(g5)
    c: DistanceY(g-1,g6) = 23
    c: DistanceX(g-1,g6) = 23
    c: Distance(g0,g1) = 5.7
FEATURE [PartDesign::Pocket] Pocket038
  Length = 5
  Sketch = -> Sketch084
  Type = 0
FEATURE [Part::Mirroring] Part__Mirroring004  label="Pocket038 (Mirror #5)"
  Base = (0,0,0)
  Normal = (0,0,1)
  Source = -> Pocket038
FEATURE [Part::Mirroring] Part__Mirroring005  label="Pocket038 (Mirror #6)"
  Base = (0,0,0)
  Normal = (1,0,0)
  Source = -> Pocket038
FEATURE [Part::Mirroring] Part__Mirroring006  label="Pocket038 (Mirror #7)"
  Base = (0,0,0)
  Normal = (1,0,0)
  Source = -> Part__Mirroring004
FEATURE [Part::MultiFuse] Fusion004
  Shapes = -> [Pocket038,Part__Mirroring005,Part__Mirroring004,Part__Mirroring006,Fusion003,Pad]
FEATURE [Sketcher::SketchObject] Sketch085
  Placement = pos=(0,120,0) rot=(1,0,0;1.5708rad)
  Support = -> Fillet005 [Face4]
  sketch-geometry (8):
    g0: Circle CenterX=23 CenterY=-23 CenterZ=0 NormalX=0 NormalY=0 NormalZ=1 Radius=1.7
    g1: Circle CenterX=-23 CenterY=-23 CenterZ=0 NormalX=0 NormalY=0 NormalZ=1 Radius=1.7
    g2: Circle CenterX=23 CenterY=23 CenterZ=0 NormalX=0 NormalY=0 NormalZ=1 Radius=1.7
    g3: Circle CenterX=-23 CenterY=23 CenterZ=0 NormalX=0 NormalY=0 NormalZ=1 Radius=1.7
    g4: LineSegment [constr] StartX=-23 StartY=23 StartZ=0 EndX=23 EndY=23 EndZ=0
    g5: LineSegment [constr] StartX=23 StartY=23 StartZ=0 EndX=23 EndY=-23 EndZ=0
    g6: LineSegment [constr] StartX=23 StartY=-23 StartZ=0 EndX=-23 EndY=-23 EndZ=0
    g7: LineSegment [constr] StartX=-23 StartY=23 StartZ=0 EndX=-23 EndY=-23 EndZ=0
  constraints (20):
    c: Radius(g0) = 1.7
    c: Equal(g0,g1)
    c: Equal(g0,g2) = 1.7
    c: DistanceX(g3,g-1) = 23
    c: DistanceY(g-1,g3) = 23
    c: Horizontal(g4)
    c: Vertical(g5)
    c: Coincident(g1,g6)
    c: Coincident(g1,g7)
    c: Coincident(g0,g5)
    c: Coincident(g0,g6)
    c: Coincident(g4,g5)
    c: Coincident(g4,g2)
    c: Coincident(g3,g4)
    c: Coincident(g3,g7)
    c: DistanceX(g6,g6) = 46
    c: Vertical(g7)
    c: Horizontal(g6)
    c: DistanceY(g7,g7) = 46
    c: Equal(g3,g0)
FEATURE [PartDesign::Pocket] Pocket039  label="rear001"
  Length = 5
  Sketch = -> Sketch085
  Type = 0
FEATURE [PartDesign::Fillet] Fillet027  label="arm_frontR"
  Base = -> Pocket033 [Edge21,Edge20,Edge10,Edge4,Edge6]
  Radius = 1
FEATURE [PartDesign::Fillet] Fillet028  label="arm_rearR"
  Base = -> Part__Mirroring [Edge20,Edge21,Edge6,Edge4,Edge10]
  Placement = pos=(0,160,0) rot=(0,0,1;0rad)
  Radius = 1
FEATURE [PartDesign::Fillet] Fillet029  label="arm_rearL"
  Base = -> Part__Mirroring002 [Edge21,Edge6,Edge20,Edge4,Edge10]
  Radius = 1
FEATURE [PartDesign::Fillet] Fillet030  label="arm_frontL"
  Base = -> Part__Mirroring001 [Edge6,Edge21,Edge20,Edge10,Edge4]
  Radius = 1
FEATURE [Sketcher::SketchObject] Sketch086
  Placement = pos=(0,0,-5) rot=(0,0,1;0rad)
  sketch-geometry (4):
    g0: LineSegment StartX=-40 StartY=130 StartZ=0 EndX=40 EndY=130 EndZ=0
    g1: LineSegment StartX=40 StartY=130 StartZ=0 EndX=40 EndY=30 EndZ=0
    g2: LineSegment StartX=40 StartY=30 StartZ=0 EndX=-40 EndY=30 EndZ=0
    g3: LineSegment StartX=-40 StartY=30 StartZ=0 EndX=-40 EndY=130 EndZ=0
  constraints (12):
    c: Coincident(g0,g1)
    c: Coincident(g1,g2)
    c: Coincident(g2,g3)
    c: Coincident(g3,g0)
    c: Horizontal(g0)
    c: Horizontal(g2)
    c: Vertical(g1)
    c: Vertical(g3)
    c: Distance(g0) = 80
    c: DistanceY(g1,g1) = 100
    c: Symmetric(g0,g0,g-2)
    c: DistanceY(g-1,g2) = 30
FEATURE [Part::Extrusion] Extrude020
  Base = -> Sketch086
  Dir = (0,0,100)
  Solid = true
FEATURE [Sketcher::SketchObject] Sketch087
  Placement = pos=(30,0,0) rot=(0.57735,0.57735,0.57735;2.0944rad)
  Support = -> Fusion004 [Face143]
  sketch-geometry (1):
    g0: Circle CenterX=3 CenterY=20 CenterZ=0 NormalX=0 NormalY=0 NormalZ=1 Radius=3
  constraints (3):
    c: Radius(g0) = 3
    c: DistanceX(g-1,g0) = 3
    c: DistanceY(g-1,g0) = 20
FEATURE [PartDesign::Pocket] Pocket040
  Length = 20
  Sketch = -> Sketch087
  Type = 0
FEATURE [Sketcher::SketchObject] Sketch088
  ExternalGeometry = -> [Pocket040]
  Placement = pos=(0,0,4) rot=(0,0,1;0rad)
  Support = -> Pocket040 [Face161]
  sketch-geometry (4):
    g0: Circle CenterX=-15.2 CenterY=82.2 CenterZ=0 NormalX=0 NormalY=0 NormalZ=1 Radius=3.7
    g1: Circle CenterX=15.3 CenterY=82.2 CenterZ=0 NormalX=0 NormalY=0 NormalZ=1 Radius=3.7
    g2: Circle CenterX=15.3 CenterY=51.7 CenterZ=0 NormalX=0 NormalY=0 NormalZ=1 Radius=3.7
    g3: Circle CenterX=-15.2 CenterY=51.7 CenterZ=0 NormalX=0 NormalY=0 NormalZ=1 Radius=3.7
  constraints (8):
    c: Coincident(g0,g-3)
    c: Radius(g0) = 3.7
    c: Equal(g0,g1) = 3.7
    c: Coincident(g1,g-6)
    c: Coincident(g2,g-5)
    c: Equal(g0,g3) = 3.7
    c: Coincident(g3,g-4)
    c: Equal(g2,g0)
FEATURE [PartDesign::Pocket] Pocket041
  Length = 2
  Sketch = -> Sketch088
  Type = 0
FEATURE [Sketcher::SketchObject] Sketch089
  Placement = pos=(0,0,40) rot=(0,0,1;0rad)
  Support = -> Pocket041 [Face125]
  sketch-geometry (2):
    g0: Circle CenterX=20 CenterY=100 CenterZ=0 NormalX=0 NormalY=0 NormalZ=1 Radius=1
    g1: Circle CenterX=20 CenterY=100 CenterZ=0 NormalX=0 NormalY=0 NormalZ=1 Radius=3
  constraints (5):
    c: Coincident(g1,g0)
    c: Radius(g0) = 1
    c: Radius(g1) = 3
    c: DistanceY(g-1,g0) = 100
    c: DistanceX(g-1,g0) = 20
FEATURE [Part::Extrusion] Extrude021
  Base = -> Sketch089
  Dir = (0,0,5)
  Placement = pos=(-19,0,19) rot=(0,1,0;0.785398rad)
  Solid = true
FEATURE [Part::Mirroring] Part__Mirroring007  label="Extrude021 (Mirror #8)"
  Base = (0,0,0)
  Normal = (1,0,0)
  Source = -> Extrude021
FEATURE [Part::MultiFuse] Fusion005
  Shapes = -> [Pocket041,Part__Mirroring007,Extrude021]
FEATURE [Sketcher::SketchObject] Sketch090
  ExternalGeometry = -> [Fusion005]
  Placement = pos=(31.8198,0,31.8198) rot=(0.357407,0.357407,0.862856;1.71777rad)
  Support = -> Fusion005 [Face1]
  sketch-geometry (1):
    g0: Circle CenterX=100 CenterY=6.87006 CenterZ=0 NormalX=0 NormalY=0 NormalZ=1 Radius=1
  constraints (2):
    c: Coincident(g0,g-3)
    c: Equal(g0,g-3)
FEATURE [PartDesign::Pocket] Pocket042
  Length = 10
  Sketch = -> Sketch090
  Type = 0
FEATURE [Sketcher::SketchObject] Sketch091
  ExternalGeometry = -> [Pocket042]
  Placement = pos=(-31.8198,0,31.8198) rot=(0.357407,-0.357407,-0.862856;1.71777rad)
  Support = -> Pocket042 [Face310]
  sketch-geometry (1):
    g0: Circle CenterX=-100 CenterY=6.87006 CenterZ=0 NormalX=0 NormalY=0 NormalZ=1 Radius=1
  constraints (2):
    c: Coincident(g0,g-3)
    c: Equal(g0,g-3)
FEATURE [PartDesign::Pocket] Pocket043
  Length = 10
  Sketch = -> Sketch091
  Type = 0
FEATURE [Sketcher::SketchObject] Sketch092
  Placement = pos=(0,0,4) rot=(0,0,1;0rad)
  Support = -> Pocket043 [Face339]
  sketch-geometry (3):
    g0: Circle CenterX=-20 CenterY=100 CenterZ=0 NormalX=0 NormalY=0 NormalZ=1 Radius=1
    g1: Circle CenterX=20 CenterY=100 CenterZ=0 NormalX=0 NormalY=0 NormalZ=1 Radius=1
    g2: LineSegment [constr] StartX=-20 StartY=100 StartZ=0 EndX=20 EndY=100 EndZ=0
  constraints (8):
    c: Radius(g0) = 1
    c: Equal(g0,g1)
    c: Coincident(g2,g0)
    c: Coincident(g2,g1)
    c: Horizontal(g2)
    c: Symmetric(g1,g0,g-2)
    c: DistanceX(g-1,g1) = 20
    c: DistanceY(g-1,g1) = 100
FEATURE [PartDesign::Pocket] Pocket044
  Length = 5
  Sketch = -> Sketch092
  Type = 0
FEATURE [PartDesign::Fillet] Fillet031
  Base = -> Pocket044 [Edge528,Edge194,Edge1,Edge4,Edge5,Edge195]
  Radius = 1
FEATURE [PartDesign::Fillet] Fillet032
  Base = -> Fillet031 [Edge227]
  Radius = 0.5
FEATURE [PartDesign::Fillet] Fillet033
  Base = -> Fillet032 [Edge131,Edge462,Edge463,Edge176,Edge130,Edge461,Edge125,Edge448,Edge126,Edge450,Edge451,Edge172,Edge127,Edge173,Edge128,Edge174,Edge454,Edge455,Edge132,Edge177,Edge129,Edge178,Edge457,Edge458]
  Radius = 1
FEATURE [PartDesign::Fillet] Fillet034
  Base = -> Fillet033 [Edge546,Edge154,Edge540,Edge541,Edge276,Edge152,Edge278,Edge543,Edge544,Edge153,Edge527,Edge145,Edge523,Edge524,Edge280,Edge144,Edge282,Edge530,Edge531,Edge147,Edge281,Edge146,Edge277,Edge151]
  Radius = 1
FEATURE [PartDesign::Fillet] Fillet035
  Base = -> Fillet034 [Edge43,Edge139]
  Radius = 1
FEATURE [PartDesign::Fillet] Fillet036
  Base = -> Fillet035 [Edge27,Edge28,Edge29,Edge30,Edge31,Edge32,Edge33,Edge34]
  Radius = 0.5
FEATURE [PartDesign::Fillet] Fillet037
  Base = -> Fillet036 [Edge160,Edge156,Edge55,Edge161,Edge162,Edge163,Edge164,Edge165,Edge166,Edge167,Edge168,Edge169,Edge530,Edge532,Edge535,Edge536,Edge529,Edge1087,Edge1088,Edge525,Edge157,Edge527,Edge528]
  Radius = 0.5
FEATURE [Sketcher::SketchObject] Sketch093
  ExternalGeometry = -> [Fillet037]
  Placement = pos=(0,0,40) rot=(0,0,1;0rad)
  Support = -> Fillet037 [Face5]
  sketch-geometry (4):
    g0: Circle CenterX=-15.2 CenterY=82.2 CenterZ=0 NormalX=0 NormalY=0 NormalZ=1 Radius=3
    g1: Circle CenterX=15.3 CenterY=82.2 CenterZ=0 NormalX=0 NormalY=0 NormalZ=1 Radius=3
    g2: Circle CenterX=-15.2 CenterY=51.7 CenterZ=0 NormalX=0 NormalY=0 NormalZ=1 Radius=3
    g3: Circle CenterX=15.3 CenterY=51.7 CenterZ=0 NormalX=0 NormalY=0 NormalZ=1 Radius=3
  constraints (8):
    c: Coincident(g0,g-5)
    c: Radius(g0) = 3
    c: Equal(g0,g1) = 3
    c: Equal(g0,g2) = 3
    c: Equal(g0,g3) = 3
    c: Coincident(g1,g-3)
    c: Coincident(g-6,g2)
    c: Coincident(g-4,g3)
FEATURE [PartDesign::Pocket] Pocket045
  Length = 5
  Sketch = -> Sketch093
  Type = 0
FEATURE [PartDesign::Fillet] Fillet038
  Base = -> Pocket045 [Edge9,Edge8,Edge7,Edge6,Edge187,Edge188,Edge185,Edge186]
  Radius = 1
FEATURE [Sketcher::SketchObject] Sketch094
  Placement = pos=(0,-3,0) rot=(1,0,0;1.5708rad)
  Support = -> Fillet038 [Face17]
  sketch-geometry (15):
    g0: ArcOfCircle CenterX=10 CenterY=-32 CenterZ=0 NormalX=0 NormalY=0 NormalZ=1 Radius=2 StartAngle=4.71239 EndAngle=7.85398
    g1: ArcOfCircle CenterX=-10 CenterY=-32 CenterZ=0 NormalX=0 NormalY=0 NormalZ=1 Radius=2 StartAngle=1.5708 EndAngle=4.71239
    g2: LineSegment StartX=10 StartY=-30 StartZ=0 EndX=-10 EndY=-30 EndZ=0
    g3: LineSegment StartX=10 StartY=-34 StartZ=0 EndX=-10 EndY=-34 EndZ=0
    g4: LineSegment [constr] StartX=10 StartY=-32 StartZ=0 EndX=-10 EndY=-32 EndZ=0
    g5: ArcOfCircle CenterX=16 CenterY=-24 CenterZ=0 NormalX=0 NormalY=0 NormalZ=1 Radius=2 StartAngle=4.71239 EndAngle=7.85398
    g6: ArcOfCircle CenterX=-16 CenterY=-24 CenterZ=0 NormalX=0 NormalY=0 NormalZ=1 Radius=2 StartAngle=1.5708 EndAngle=4.71239
    g7: LineSegment StartX=16 StartY=-22 StartZ=0 EndX=-16 EndY=-22 EndZ=0
    g8: LineSegment StartX=16 StartY=-26 StartZ=0 EndX=-16 EndY=-26 EndZ=0
    g9: LineSegment [constr] StartX=16 StartY=-24 StartZ=0 EndX=-16 EndY=-24 EndZ=0
    g10: ArcOfCircle CenterX=20 CenterY=-16 CenterZ=0 NormalX=0 NormalY=0 NormalZ=1 Radius=2 StartAngle=4.71239 EndAngle=7.85398
    g11: ArcOfCircle CenterX=-20 CenterY=-16 CenterZ=0 NormalX=0 NormalY=0 NormalZ=1 Radius=2 StartAngle=1.5708 EndAngle=4.71239
    g12: LineSegment StartX=20 StartY=-14 StartZ=0 EndX=-20 EndY=-14 EndZ=0
    g13: LineSegment StartX=20 StartY=-18 StartZ=0 EndX=-20 EndY=-18 EndZ=0
    g14: LineSegment [constr] StartX=20 StartY=-16 StartZ=0 EndX=-20 EndY=-16 EndZ=0
  constraints (36):
    c: Tangent(g0,g3) = 1.5708
    c: Tangent(g0,g2) = -1.5708
    c: Tangent(g2,g1) = -1.5708
    c: Tangent(g3,g1) = 1.5708
    c: Equal(g0,g1)
    c: Coincident(g4,g1)
    c: Coincident(g0,g4)
    c: Distance(g0,g0) = 4
    c: Distance(g4) = 20
    c: Horizontal(g4)
    c: Symmetric(g1,g0,g-2)
    c: Tangent(g5,g8) = 1.5708
    c: Tangent(g5,g7) = -1.5708
    c: Tangent(g7,g6) = -1.5708
    c: Tangent(g8,g6) = 1.5708
    c: Equal(g5,g6)
    c: Coincident(g9,g6)
    c: Coincident(g5,g9)
    c: Equal(g0,g5) = 4
    c: Horizontal(g9)
    c: Tangent(g10,g13) = 1.5708
    c: Tangent(g10,g12) = -1.5708
    c: Tangent(g12,g11) = -1.5708
    c: Tangent(g13,g11) = 1.5708
    c: Equal(g10,g11)
    c: Coincident(g14,g11)
    c: Coincident(g10,g14)
    c: Horizontal(g14)
    c: Symmetric(g5,g6,g-2)
    c: Symmetric(g10,g11,g-2)
    c: DistanceY(g6,g11) = 8
    c: DistanceY(g1,g6) = 8
    c: Equal(g10,g5)
    c: Distance(g14) = 40
    c: Distance(g9) = 32
    c: DistanceY(g10,g-1) = 16
FEATURE [PartDesign::Pocket] Pocket046
  Length = 10
  Sketch = -> Sketch094
  Type = 0
FEATURE [Sketcher::SketchObject] Sketch095
  ExternalGeometry = -> [Pocket046]
  Placement = pos=(-30,0,1e-12) rot=(0.57735,-0.57735,-0.57735;2.0944rad)
  Support = -> Pocket046 [Face47]
  sketch-geometry (1):
    g0: Circle CenterX=-3 CenterY=20 CenterZ=0 NormalX=0 NormalY=0 NormalZ=1 Radius=3
  constraints (2):
    c: Coincident(g0,g-3)
    c: Radius(g0) = 3
FEATURE [PartDesign::Pocket] Pocket047
  Length = 20
  Sketch = -> Sketch095
  Type = 0
FEATURE [PartDesign::Fillet] Fillet039
  Base = -> Pocket047 [Edge518,Edge507,Edge506]
  Radius = 1
FEATURE [PartDesign::Fillet] Fillet040  label="body"
  Base = -> Fillet039 [Edge99,Edge100,Edge88,Edge87,Edge18,Edge16,Edge14,Edge12,Edge22,Edge45,Edge226,Edge228,Edge258,Edge236,Edge237,Edge77,Edge76,Edge74,Edge75,Edge80,Edge79,Edge242,Edge252,Edge81,Edge251,Edge257,Edge245]
  Radius = 1
FEATURE [Sketcher::SketchObject] Sketch096
  Placement = pos=(0,125,0) rot=(0,0.707107,0.707107;3.14159rad)
  Support = -> Pocket039 [Face8]
  sketch-geometry (16):
    g0: ArcOfCircle CenterX=-15 CenterY=34 CenterZ=0 NormalX=0 NormalY=0 NormalZ=1 Radius=2 StartAngle=1.5708 EndAngle=4.71239
    g1: ArcOfCircle CenterX=15 CenterY=34 CenterZ=0 NormalX=0 NormalY=0 NormalZ=1 Radius=2 StartAngle=4.71239 EndAngle=7.85398
    g2: LineSegment StartX=-15 StartY=32 StartZ=0 EndX=15 EndY=32 EndZ=0
    g3: LineSegment StartX=-15 StartY=36 StartZ=0 EndX=15 EndY=36 EndZ=0
    g4: ArcOfCircle CenterX=-20 CenterY=16 CenterZ=0 NormalX=0 NormalY=0 NormalZ=1 Radius=2 StartAngle=0 EndAngle=3.14159
    g5: ArcOfCircle CenterX=-20 CenterY=6 CenterZ=0 NormalX=0 NormalY=0 NormalZ=1 Radius=2 StartAngle=3.14159 EndAngle=6.28319
    g6: LineSegment StartX=-22 StartY=16 StartZ=0 EndX=-22 EndY=6 EndZ=0
    g7: LineSegment StartX=-18 StartY=16 StartZ=0 EndX=-18 EndY=6 EndZ=0
    g8: ArcOfCircle CenterX=20 CenterY=16 CenterZ=0 NormalX=0 NormalY=0 NormalZ=1 Radius=2 StartAngle=0 EndAngle=3.14159
    g9: ArcOfCircle CenterX=20 CenterY=6 CenterZ=0 NormalX=0 NormalY=0 NormalZ=1 Radius=2 StartAngle=3.14159 EndAngle=6.28319
    g10: LineSegment StartX=18 StartY=16 StartZ=0 EndX=18 EndY=6 EndZ=0
    g11: LineSegment StartX=22 StartY=16 StartZ=0 EndX=22 EndY=6 EndZ=0
    g12: ArcOfCircle CenterX=-15 CenterY=-32 CenterZ=0 NormalX=0 NormalY=0 NormalZ=1 Radius=2 StartAngle=1.5708 EndAngle=4.71239
    g13: ArcOfCircle CenterX=15 CenterY=-32 CenterZ=0 NormalX=0 NormalY=0 NormalZ=1 Radius=2 StartAngle=4.71239 EndAngle=7.85398
    g14: LineSegment StartX=-15 StartY=-34 StartZ=0 EndX=15 EndY=-34 EndZ=0
    g15: LineSegment StartX=-15 StartY=-30 StartZ=0 EndX=15 EndY=-30 EndZ=0
  constraints (40):
    c: Tangent(g0,g3) = 1.5708
    c: Tangent(g0,g2) = -1.5708
    c: Tangent(g2,g1) = -1.5708
    c: Tangent(g3,g1) = 1.5708
    c: Horizontal(g2)
    c: Equal(g0,g1)
    c: DistanceY(g0,g0) = 4
    c: Symmetric(g1,g0,g-2)
    c: Distance(g3) = 30
    c: DistanceY(g-1,g1) = 36
    c: Tangent(g4,g7) = 1.5708
    c: Tangent(g4,g6) = -1.5708
    c: Tangent(g6,g5) = -1.5708
    c: Tangent(g7,g5) = 1.5708
    c: Vertical(g6)
    c: Equal(g4,g5)
    c: DistanceX(g4,g4) = 4
    c: DistanceY(g7,g7) = 10
    c: DistanceY(g-1,g5) = 6
    c: Tangent(g8,g11) = 1.5708
    c: Tangent(g8,g10) = -1.5708
    c: Tangent(g10,g9) = -1.5708
    c: Tangent(g11,g9) = 1.5708
    c: Vertical(g10)
    c: Equal(g8,g9)
    c: Equal(g4,g8) = 4
    c: Equal(g7,g11) = 10
    c: DistanceX(g5,g-1) = 20
    c: DistanceX(g-1,g9) = 20
    c: DistanceY(g-1,g9) = 6
    c: Tangent(g12,g15) = 1.5708
    c: Tangent(g12,g14) = -1.5708
    c: Tangent(g14,g13) = -1.5708
    c: Tangent(g15,g13) = 1.5708
    c: Horizontal(g14)
    c: Equal(g12,g13)
    c: Equal(g0,g12) = 4
    c: Equal(g3,g15) = 30
    c: Symmetric(g13,g12,g-2)
    c: DistanceY(g12,g-1) = 32
FEATURE [PartDesign::Pocket] Pocket048
  Length = 5
  Sketch = -> Sketch096
  Type = 0
FEATURE [PartDesign::Fillet] Fillet041  label="rear_w_vents"
  Base = -> Pocket048 [Edge59,Edge60,Edge61,Edge58,Edge64,Edge65,Edge62,Edge63,Edge69,Edge70,Edge67,Edge68,Edge42,Edge45,Edge92,Edge56,Edge57,Edge48,Edge10,Edge9]
  Radius = 0.5
FEATURE [Part::MultiCommon] Common  label="body_top"
  Shapes = -> [Fillet040,Extrude020]
FEATURE [Sketcher::SketchObject] Sketch097
  sketch-geometry (4):
    g0: LineSegment StartX=-128.622 StartY=162.63 StartZ=0 EndX=128.622 EndY=162.63 EndZ=0
    g1: LineSegment StartX=128.622 StartY=162.63 StartZ=0 EndX=128.622 EndY=-20 EndZ=0
    g2: LineSegment StartX=128.622 StartY=-20 StartZ=0 EndX=-128.622 EndY=-20 EndZ=0
    g3: LineSegment StartX=-128.622 StartY=-20 StartZ=0 EndX=-128.622 EndY=162.63 EndZ=0
  constraints (12):
    c: Coincident(g0,g1)
    c: Coincident(g1,g2)
    c: Coincident(g2,g3)
    c: Coincident(g3,g0)
    c: Horizontal(g0)
    c: Horizontal(g2)
    c: Vertical(g1)
    c: Vertical(g3)
    c: DistanceX(g0,g0) = 257.244
    c: DistanceY(g3,g3) = 182.63
    c: Symmetric(g1,g2,g-2)
    c: DistanceY(g1,g-1) = 20
FEATURE [Part::Extrusion] Extrude022
  Base = -> Sketch097
  Dir = (0,0,200)
  Placement = pos=(0,0,-100) rot=(0,0,1;0rad)
  Solid = true
FEATURE [Part::Cut] Cut002
  Base = -> Extrude022
  Tool = -> Extrude020
FEATURE [Part::MultiCommon] Common001  label="body_bottom"
  Shapes = -> [Cut002,Fillet040]
FEATURE [Sketcher::SketchObject] Sketch098
  ExternalGeometry = -> [Common]
  Placement = pos=(0,0,-5) rot=(1,0,0;3.14159rad)
  Support = -> Common [Face79]
  sketch-geometry (14):
    g0: LineSegment StartX=-27 StartY=-75 StartZ=0 EndX=-22 EndY=-75 EndZ=0
    g1: LineSegment StartX=-19 StartY=-78 StartZ=0 EndX=-19 EndY=-82 EndZ=0
    g2: LineSegment StartX=-22 StartY=-85 StartZ=0 EndX=-27 EndY=-85 EndZ=0
    g3: ArcOfCircle CenterX=-22 CenterY=-78 CenterZ=0 NormalX=0 NormalY=0 NormalZ=1 Radius=3 StartAngle=0 EndAngle=1.5708
    g4: ArcOfCircle CenterX=-22 CenterY=-82 CenterZ=0 NormalX=0 NormalY=0 NormalZ=1 Radius=3 StartAngle=4.71239 EndAngle=6.28319
    g5: LineSegment StartX=-27 StartY=-75 StartZ=0 EndX=-27 EndY=-85 EndZ=0
    g6: LineSegment [constr] StartX=-22 StartY=-75 StartZ=0 EndX=27 EndY=-75 EndZ=0
    g7: LineSegment [constr] StartX=-22 StartY=-85 StartZ=0 EndX=27 EndY=-85 EndZ=0
    g8: LineSegment StartX=27 StartY=-75 StartZ=0 EndX=22 EndY=-75 EndZ=0
    g9: LineSegment StartX=27 StartY=-85 StartZ=0 EndX=22 EndY=-85 EndZ=0
    g10: LineSegment StartX=19 StartY=-78 StartZ=0 EndX=19 EndY=-82 EndZ=0
    g11: ArcOfCircle CenterX=22 CenterY=-82 CenterZ=0 NormalX=0 NormalY=0 NormalZ=1 Radius=3 StartAngle=3.14159 EndAngle=4.71239
    g12: ArcOfCircle CenterX=22 CenterY=-78 CenterZ=0 NormalX=0 NormalY=0 NormalZ=1 Radius=3 StartAngle=1.5708 EndAngle=3.14159
    g13: LineSegment StartX=27 StartY=-75 StartZ=0 EndX=27 EndY=-85 EndZ=0
  constraints (36):
    c: PointOnObject(g0,g-3)
    c: Horizontal(g0)
    c: Vertical(g1)
    c: PointOnObject(g2,g-3)
    c: Horizontal(g2)
    c: Tangent(g0,g3) = 1.5708
    c: Tangent(g1,g3) = 1.5708
    c: Tangent(g1,g4) = 1.5708
    c: Tangent(g2,g4) = 1.5708
    c: Coincident(g5,g0)
    c: Coincident(g5,g2)
    c: Distance(g5) = 10
    c: DistanceX(g2,g1) = 8
    c: Radius(g4) = 3
    c: Radius(g3) = 3
    c: DistanceY(g2,g-1) = 85
    c: Coincident(g6,g0)
    c: PointOnObject(g6,g-4)
    c: Horizontal(g6)
    c: Coincident(g7,g2)
    c: PointOnObject(g7,g-4)
    c: Horizontal(g7)
    c: Coincident(g8,g6)
    c: Coincident(g9,g7)
    c: Vertical(g10)
    c: Tangent(g9,g11) = 1.5708
    c: Tangent(g10,g11) = -1.5708
    c: Tangent(g8,g12) = -1.5708
    c: Tangent(g10,g12) = -1.5708
    c: Radius(g12) = 3
    c: Radius(g11) = 3
    c: Horizontal(g9)
    c: Horizontal(g8)
    c: DistanceX(g10,g7) = 8
    c: Coincident(g13,g6)
    c: Coincident(g13,g7)
FEATURE [PartDesign::Pad] Pad025
  Length = 7
  Length2 = 100
  Reversed = true
  Sketch = -> Sketch098
  Type = 0
FEATURE [Sketcher::SketchObject] Sketch099
  Placement = pos=(0,0,-5) rot=(1,0,0;3.14159rad)
  Support = -> Pad025 [Face219]
  sketch-geometry (3):
    g0: Circle CenterX=-23 CenterY=-80 CenterZ=0 NormalX=0 NormalY=0 NormalZ=1 Radius=1.7
    g1: Circle CenterX=23 CenterY=-80 CenterZ=0 NormalX=0 NormalY=0 NormalZ=1 Radius=1.7
    g2: LineSegment [constr] StartX=-23 StartY=-80 StartZ=0 EndX=23 EndY=-80 EndZ=0
  constraints (8):
    c: Radius(g0) = 1.7
    c: Equal(g0,g1)
    c: Coincident(g2,g0)
    c: Coincident(g2,g1)
    c: Horizontal(g2)
    c: Symmetric(g1,g0,g-2)
    c: DistanceY(g1,g-1) = 80
    c: DistanceX(g-1,g1) = 23
FEATURE [PartDesign::Pocket] Pocket049
  Length = 10
  Sketch = -> Sketch099
  Type = 0
FEATURE [Sketcher::SketchObject] Sketch100
  ExternalGeometry = -> [Pocket049]
  Placement = pos=(0,0,4) rot=(0,0,1;0rad)
  Support = -> Pocket049 [Face215]
  sketch-geometry (14):
    g0: LineSegment StartX=-20.15 StartY=81.6454 StartZ=0 EndX=-23 EndY=83.2909 EndZ=0
    g1: LineSegment StartX=-23 StartY=83.2909 StartZ=0 EndX=-25.85 EndY=81.6454 EndZ=0
    g2: LineSegment StartX=-25.85 StartY=81.6454 StartZ=0 EndX=-25.85 EndY=78.3546 EndZ=0
    g3: LineSegment StartX=-25.85 StartY=78.3546 StartZ=0 EndX=-23 EndY=76.7091 EndZ=0
    g4: LineSegment StartX=-23 StartY=76.7091 StartZ=0 EndX=-20.15 EndY=78.3546 EndZ=0
    g5: LineSegment StartX=-20.15 StartY=78.3546 StartZ=0 EndX=-20.15 EndY=81.6454 EndZ=0
    g6: Circle [constr] CenterX=-23 CenterY=80 CenterZ=0 NormalX=0 NormalY=0 NormalZ=1 Radius=3.2909
    g7: LineSegment StartX=25.85 StartY=81.6454 StartZ=0 EndX=23 EndY=83.2909 EndZ=0
    g8: LineSegment StartX=23 StartY=83.2909 StartZ=0 EndX=20.15 EndY=81.6454 EndZ=0
    g9: LineSegment StartX=20.15 StartY=81.6454 StartZ=0 EndX=20.15 EndY=78.3546 EndZ=0
    g10: LineSegment StartX=20.15 StartY=78.3546 StartZ=0 EndX=23 EndY=76.7091 EndZ=0
    g11: LineSegment StartX=23 StartY=76.7091 StartZ=0 EndX=25.85 EndY=78.3546 EndZ=0
    g12: LineSegment StartX=25.85 StartY=78.3546 StartZ=0 EndX=25.85 EndY=81.6454 EndZ=0
    g13: Circle [constr] CenterX=23 CenterY=80 CenterZ=0 NormalX=0 NormalY=0 NormalZ=1 Radius=3.2909
  constraints (32):
    c: Coincident(g0,g1)
    c: Coincident(g1,g2)
    c: Coincident(g2,g3)
    c: Coincident(g3,g4)
    c: Coincident(g4,g5)
    c: Coincident(g5,g0)
    c: Equal(g0, g1-g5) x5
    c: PointOnObject(g0,g6)
    c: PointOnObject(g1,g6)
    c: PointOnObject(g2,g6)
    c: PointOnObject(g3,g6)
    c: PointOnObject(g4,g6)
    c: PointOnObject(g5,g6)
    c: Coincident(g6,g-4)
    c: Distance(g0,g1) = 5.7
    c: Vertical(g5)
    c: Coincident(g7,g8)
    c: Coincident(g8,g9)
    c: Coincident(g9,g10)
    c: Coincident(g10,g11)
    c: Coincident(g11,g12)
    c: Coincident(g12,g7)
    c: Equal(g7, g8-g12) x5
    c: PointOnObject(g7,g13)
    c: PointOnObject(g8,g13)
    c: PointOnObject(g9,g13)
    c: PointOnObject(g10,g13)
    c: PointOnObject(g11,g13)
    c: PointOnObject(g12,g13)
    c: Coincident(g13,g-3)
    c: Vertical(g12)
    c: Distance(g8,g7) = 5.7
FEATURE [PartDesign::Pocket] Pocket050
  Length = 8
  Midplane = true
  Sketch = -> Sketch100
  Type = 0
FEATURE [Sketcher::SketchObject] Sketch101
  ExternalGeometry = -> [Pocket050]
  Placement = pos=(0,30,0) rot=(1,0,0;1.5708rad)
  Support = -> Pocket050 [Face36]
  sketch-geometry (12):
    g0: LineSegment StartX=-27 StartY=25 StartZ=0 EndX=-22 EndY=25 EndZ=0
    g1: LineSegment StartX=-19 StartY=22 StartZ=0 EndX=-19 EndY=18 EndZ=0
    g2: LineSegment StartX=-27 StartY=15 StartZ=0 EndX=-22 EndY=15 EndZ=0
    g3: LineSegment StartX=27 StartY=25 StartZ=0 EndX=22 EndY=25 EndZ=0
    g4: LineSegment StartX=19 StartY=22 StartZ=0 EndX=19 EndY=18 EndZ=0
    g5: LineSegment StartX=27 StartY=15 StartZ=0 EndX=22 EndY=15 EndZ=0
    g6: ArcOfCircle CenterX=-22 CenterY=22 CenterZ=0 NormalX=0 NormalY=0 NormalZ=1 Radius=3 StartAngle=0 EndAngle=1.5708
    g7: ArcOfCircle CenterX=-22 CenterY=18 CenterZ=0 NormalX=0 NormalY=0 NormalZ=1 Radius=3 StartAngle=4.71239 EndAngle=6.28319
    g8: ArcOfCircle CenterX=22 CenterY=22 CenterZ=0 NormalX=0 NormalY=0 NormalZ=1 Radius=3 StartAngle=1.5708 EndAngle=3.14159
    g9: ArcOfCircle CenterX=22 CenterY=18 CenterZ=0 NormalX=0 NormalY=0 NormalZ=1 Radius=3 StartAngle=3.14159 EndAngle=4.71239
    g10: LineSegment StartX=-27 StartY=25 StartZ=0 EndX=-27 EndY=15 EndZ=0
    g11: LineSegment StartX=27 StartY=25 StartZ=0 EndX=27 EndY=15 EndZ=0
  constraints (32):
    c: Horizontal(g0)
    c: Vertical(g1)
    c: Horizontal(g2)
    c: Horizontal(g3)
    c: Vertical(g4)
    c: PointOnObject(g5,g-3)
    c: Horizontal(g5)
    c: Tangent(g0,g6) = 1.5708
    c: Tangent(g1,g6) = 1.5708
    c: Tangent(g1,g7) = 1.5708
    c: Tangent(g2,g7) = -1.5708
    c: Tangent(g3,g8) = -1.5708
    c: Tangent(g4,g8) = -1.5708
    c: Tangent(g4,g9) = -1.5708
    c: Tangent(g5,g9) = 1.5708
    c: Equal(g8,g6)
    c: Equal(g6,g7)
    c: Equal(g7,g9)
    c: Radius(g6) = 3
    c: PointOnObject(g2,g-4)
    c: Distance(g2,g0) = 10
    c: DistanceX(g0,g1) = 8
    c: DistanceX(g4,g3) = 8
    c: DistanceY(g5,g3) = 10
    c: Coincident(g10,g2)
    c: Coincident(g11,g5)
    c: Coincident(g0,g10)
    c: Vertical(g10)
    c: DistanceY(g-4,g0) = 5
    c: Vertical(g11)
    c: Coincident(g3,g11)
    c: DistanceY(g-3,g3) = 5
FEATURE [PartDesign::Pad] Pad026
  Length = 5
  Length2 = 100
  Reversed = true
  Sketch = -> Sketch101
  Type = 0
FEATURE [Sketcher::SketchObject] Sketch102
  Placement = pos=(0,30,0) rot=(1,0,0;1.5708rad)
  Support = -> Pad026 [Face46]
  sketch-geometry (3):
    g0: Circle CenterX=-23 CenterY=20 CenterZ=0 NormalX=0 NormalY=0 NormalZ=1 Radius=1.7
    g1: Circle CenterX=23 CenterY=20 CenterZ=0 NormalX=0 NormalY=0 NormalZ=1 Radius=1.7
    g2: LineSegment [constr] StartX=-23 StartY=20 StartZ=0 EndX=23 EndY=20 EndZ=0
  constraints (8):
    c: Equal(g1,g0)
    c: Radius(g0) = 1.7
    c: DistanceY(g-1,g0) = 20
    c: DistanceX(g0,g-1) = 23
    c: Coincident(g2,g0)
    c: Coincident(g2,g1)
    c: Horizontal(g2)
    c: DistanceX(g-1,g1) = 23
FEATURE [PartDesign::Pocket] Pocket051
  Length = 10
  Sketch = -> Sketch102
  Type = 0
FEATURE [Sketcher::SketchObject] Sketch103
  ExternalGeometry = -> [Pocket051]
  Placement = pos=(0,39,0) rot=(0,0.707107,0.707107;3.14159rad)
  Support = -> Pocket051 [Face244]
  sketch-geometry (14):
    g0: LineSegment StartX=-20.15 StartY=21.6454 StartZ=0 EndX=-23 EndY=23.2909 EndZ=0
    g1: LineSegment StartX=-23 StartY=23.2909 StartZ=0 EndX=-25.85 EndY=21.6454 EndZ=0
    g2: LineSegment StartX=-25.85 StartY=21.6454 StartZ=0 EndX=-25.85 EndY=18.3546 EndZ=0
    g3: LineSegment StartX=-25.85 StartY=18.3546 StartZ=0 EndX=-23 EndY=16.7091 EndZ=0
    g4: LineSegment StartX=-23 StartY=16.7091 StartZ=0 EndX=-20.15 EndY=18.3546 EndZ=0
    g5: LineSegment StartX=-20.15 StartY=18.3546 StartZ=0 EndX=-20.15 EndY=21.6454 EndZ=0
    g6: Circle [constr] CenterX=-23 CenterY=20 CenterZ=0 NormalX=0 NormalY=0 NormalZ=1 Radius=3.2909
    g7: LineSegment StartX=25.85 StartY=21.6454 StartZ=0 EndX=23 EndY=23.2909 EndZ=0
    g8: LineSegment StartX=23 StartY=23.2909 StartZ=0 EndX=20.15 EndY=21.6454 EndZ=0
    g9: LineSegment StartX=20.15 StartY=21.6454 StartZ=0 EndX=20.15 EndY=18.3546 EndZ=0
    g10: LineSegment StartX=20.15 StartY=18.3546 StartZ=0 EndX=23 EndY=16.7091 EndZ=0
    g11: LineSegment StartX=23 StartY=16.7091 StartZ=0 EndX=25.85 EndY=18.3546 EndZ=0
    g12: LineSegment StartX=25.85 StartY=18.3546 StartZ=0 EndX=25.85 EndY=21.6454 EndZ=0
    g13: Circle [constr] CenterX=23 CenterY=20 CenterZ=0 NormalX=0 NormalY=0 NormalZ=1 Radius=3.2909
  constraints (32):
    c: Coincident(g0,g1)
    c: Coincident(g1,g2)
    c: Coincident(g2,g3)
    c: Coincident(g3,g4)
    c: Coincident(g4,g5)
    c: Coincident(g5,g0)
    c: Equal(g0, g1-g5) x5
    c: PointOnObject(g0,g6)
    c: PointOnObject(g1,g6)
    c: PointOnObject(g2,g6)
    c: PointOnObject(g3,g6)
    c: PointOnObject(g4,g6)
    c: PointOnObject(g5,g6)
    c: Coincident(g6,g-3)
    c: Vertical(g5)
    c: Coincident(g7,g8)
    c: Coincident(g8,g9)
    c: Coincident(g9,g10)
    c: Coincident(g10,g11)
    c: Coincident(g11,g12)
    c: Coincident(g12,g7)
    c: Equal(g7, g8-g12) x5
    c: PointOnObject(g7,g13)
    c: PointOnObject(g8,g13)
    c: PointOnObject(g9,g13)
    c: PointOnObject(g10,g13)
    c: PointOnObject(g11,g13)
    c: PointOnObject(g12,g13)
    c: Coincident(g13,g-5)
    c: Vertical(g12)
    c: Distance(g8,g7) = 5.7
    c: Distance(g1,g0) = 5.7
FEATURE [PartDesign::Pocket] Pocket052
  Length = 8
  Midplane = true
  Sketch = -> Sketch103
  Type = 0
FEATURE [PartDesign::Fillet] Fillet042
  Base = -> Pocket052 [Edge187,Edge188,Edge189,Edge190,Edge191,Edge179,Edge180,Edge181,Edge182,Edge183]
  Radius = 2
FEATURE [PartDesign::Fillet] Fillet043
  Base = -> Fillet042 [Edge152,Edge389,Edge390,Edge391,Edge734]
  Radius = 1
FEATURE [PartDesign::Fillet] Fillet044  label="body_top_w nuts"
  Base = -> Fillet043 [Edge138,Edge35,Edge33,Edge31,Edge116]
  Radius = 1
FEATURE [Sketcher::SketchObject] Sketch104
  Placement = pos=(0,0,-5) rot=(0,0,1;0rad)
  Support = -> Common001 [Face88]
  sketch-geometry (16):
    g0: LineSegment StartX=27 StartY=85 StartZ=0 EndX=22 EndY=85 EndZ=0
    g1: LineSegment StartX=19 StartY=82 StartZ=0 EndX=19 EndY=78 EndZ=0
    g2: LineSegment StartX=22 StartY=75 StartZ=0 EndX=27 EndY=75 EndZ=0
    g3: LineSegment StartX=27 StartY=85 StartZ=0 EndX=27 EndY=75 EndZ=0
    g4: ArcOfCircle CenterX=22 CenterY=82 CenterZ=0 NormalX=0 NormalY=0 NormalZ=1 Radius=3 StartAngle=1.5708 EndAngle=3.14159
    g5: ArcOfCircle CenterX=22 CenterY=78 CenterZ=0 NormalX=0 NormalY=0 NormalZ=1 Radius=3 StartAngle=3.14159 EndAngle=4.71239
    g6: Circle CenterX=23 CenterY=80 CenterZ=0 NormalX=0 NormalY=0 NormalZ=1 Radius=1.7
    g7: LineSegment StartX=-27 StartY=85 StartZ=0 EndX=-22 EndY=85 EndZ=0
    g8: LineSegment StartX=-19 StartY=82 StartZ=0 EndX=-19 EndY=78 EndZ=0
    g9: LineSegment StartX=-22 StartY=75 StartZ=0 EndX=-27 EndY=75 EndZ=0
    g10: LineSegment StartX=-27 StartY=75 StartZ=0 EndX=-27 EndY=85 EndZ=0
    g11: ArcOfCircle CenterX=-22 CenterY=82 CenterZ=0 NormalX=0 NormalY=0 NormalZ=1 Radius=3 StartAngle=0 EndAngle=1.5708
    g12: ArcOfCircle CenterX=-22 CenterY=78 CenterZ=0 NormalX=0 NormalY=0 NormalZ=1 Radius=3 StartAngle=4.71239 EndAngle=6.28319
    g13: Circle CenterX=-23 CenterY=80 CenterZ=0 NormalX=0 NormalY=0 NormalZ=1 Radius=1.7
    g14: LineSegment [constr] StartX=-22 StartY=75 StartZ=0 EndX=22 EndY=75 EndZ=0
    g15: LineSegment [constr] StartX=-23 StartY=80 StartZ=0 EndX=23 EndY=80 EndZ=0
  constraints (41):
    c: Horizontal(g0)
    c: Vertical(g1)
    c: Horizontal(g2)
    c: Vertical(g3)
    c: Coincident(g0,g3)
    c: Coincident(g2,g3)
    c: Tangent(g0,g4) = -1.5708
    c: Tangent(g1,g4) = -1.5708
    c: Radius(g4) = 3
    c: Tangent(g1,g5) = -1.5708
    c: Tangent(g2,g5) = -1.5708
    c: Radius(g5) = 3
    c: Radius(g6) = 1.7
    c: Distance(g5,g0) = 10
    c: DistanceX(g1,g0) = 8
    c: Coincident(g9,g10)
    c: Coincident(g10,g7)
    c: Horizontal(g7)
    c: Horizontal(g9)
    c: Vertical(g8)
    c: Vertical(g10)
    c: Tangent(g7,g11) = 1.5708
    c: Tangent(g8,g11) = 1.5708
    c: Tangent(g8,g12) = 1.5708
    c: Tangent(g9,g12) = 1.5708
    c: Radius(g12) = 3
    c: Radius(g11) = 3
    c: DistanceX(g7,g8) = 8
    c: Distance(g10) = 10
    c: Equal(g13,g6)
    c: Coincident(g14,g9)
    c: Coincident(g14,g2)
    c: Coincident(g15,g13)
    c: Coincident(g15,g6)
    c: Horizontal(g15)
    c: Symmetric(g0,g7,g-2)
    c: Symmetric(g6,g13,g-2)
    c: DistanceY(g9,g13) = 5
    c: DistanceX(g9,g13) = 4
    c: DistanceY(g-1,g2) = 75
    c: Distance(g15) = 46
FEATURE [PartDesign::Pad] Pad027
  Length = 5
  Length2 = 100
  Reversed = true
  Sketch = -> Sketch104
  Type = 0
FEATURE [Sketcher::SketchObject] Sketch105
  ExternalGeometry = -> [Pad027]
  Placement = pos=(0,0,-40) rot=(1,0,0;3.14159rad)
  Support = -> Pad027 [Face163]
  sketch-geometry (2):
    g0: Circle CenterX=-23 CenterY=-80 CenterZ=0 NormalX=0 NormalY=0 NormalZ=1 Radius=3
    g1: Circle CenterX=23 CenterY=-80 CenterZ=0 NormalX=0 NormalY=0 NormalZ=1 Radius=3
  constraints (4):
    c: Coincident(g0,g-3)
    c: Coincident(g1,g-4)
    c: Radius(g1) = 3
    c: Radius(g0) = 3
FEATURE [PartDesign::Pocket] Pocket053
  Length = 15
  Sketch = -> Sketch105
  Type = 0
FEATURE [PartDesign::Fillet] Fillet045
  Base = -> Pocket053 [Edge558,Edge557,Edge239,Edge238]
  Radius = 1
FEATURE [Sketcher::SketchObject] Sketch106
  Placement = pos=(0,30,0) rot=(0,0.707107,0.707107;3.14159rad)
  Support = -> Fillet045 [Face13]
  sketch-geometry (14):
    g0: LineSegment StartX=27 StartY=25 StartZ=0 EndX=22 EndY=25 EndZ=0
    g1: LineSegment StartX=19 StartY=22 StartZ=0 EndX=19 EndY=18 EndZ=0
    g2: LineSegment StartX=22 StartY=15 StartZ=0 EndX=27 EndY=15 EndZ=0
    g3: LineSegment StartX=27 StartY=15 StartZ=0 EndX=27 EndY=25 EndZ=0
    g4: ArcOfCircle CenterX=22 CenterY=22 CenterZ=0 NormalX=0 NormalY=0 NormalZ=1 Radius=3 StartAngle=1.5708 EndAngle=3.14159
    g5: ArcOfCircle CenterX=22 CenterY=18 CenterZ=0 NormalX=0 NormalY=0 NormalZ=1 Radius=3 StartAngle=3.14159 EndAngle=4.71239
    g6: LineSegment StartX=-27 StartY=15 StartZ=0 EndX=-22 EndY=15 EndZ=0
    g7: LineSegment StartX=-19 StartY=18 StartZ=0 EndX=-19 EndY=22 EndZ=0
    g8: LineSegment StartX=-22 StartY=25 StartZ=0 EndX=-27 EndY=25 EndZ=0
    g9: LineSegment StartX=-27 StartY=25 StartZ=0 EndX=-27 EndY=15 EndZ=0
    g10: ArcOfCircle CenterX=-22 CenterY=22 CenterZ=0 NormalX=0 NormalY=0 NormalZ=1 Radius=3 StartAngle=0 EndAngle=1.5708
    g11: ArcOfCircle CenterX=-22 CenterY=18 CenterZ=0 NormalX=0 NormalY=0 NormalZ=1 Radius=3 StartAngle=4.71239 EndAngle=6.28319
    g12: Circle CenterX=-23 CenterY=20 CenterZ=0 NormalX=0 NormalY=0 NormalZ=1 Radius=1.7
    g13: Circle CenterX=23 CenterY=20 CenterZ=0 NormalX=0 NormalY=0 NormalZ=1 Radius=1.7
  constraints (37):
    c: Coincident(g2,g3)
    c: Coincident(g3,g0)
    c: Horizontal(g0)
    c: Horizontal(g2)
    c: Vertical(g1)
    c: Vertical(g3)
    c: Tangent(g0,g4) = -1.5708
    c: Tangent(g1,g4) = -1.5708
    c: Tangent(g1,g5) = -1.5708
    c: Tangent(g2,g5) = -1.5708
    c: Radius(g4) = 3
    c: Radius(g5) = 3
    c: Distance(g0,g2) = 10
    c: DistanceX(g1,g0) = 8
    c: Coincident(g8,g9)
    c: Coincident(g9,g6)
    c: Horizontal(g6)
    c: Horizontal(g8)
    c: Vertical(g7)
    c: Vertical(g9)
    c: Tangent(g8,g10) = -1.5708
    c: Tangent(g7,g10) = -1.5708
    c: Tangent(g7,g11) = -1.5708
    c: Tangent(g6,g11) = -1.5708
    c: Radius(g11) = 3
    c: Radius(g10) = 3
    c: DistanceY(g6,g8) = 10
    c: DistanceX(g8,g7) = 8
    c: DistanceY(g6,g12) = 5
    c: DistanceX(g6,g12) = 4
    c: Radius(g12) = 1.7
    c: Radius(g13) = 1.7
    c: DistanceY(g2,g13) = 5
    c: DistanceX(g13,g2) = 4
    c: DistanceX(g6,g-1) = 27
    c: DistanceY(g-1,g12) = 20
    c: Symmetric(g8,g0,g-2)
FEATURE [PartDesign::Pad] Pad028
  Length = 5
  Length2 = 100
  Reversed = true
  Sketch = -> Sketch106
  Type = 0
FEATURE [Sketcher::SketchObject] Sketch107
  ExternalGeometry = -> [Pad028]
  Placement = pos=(0,-3,0) rot=(1,0,0;1.5708rad)
  Support = -> Pad028 [Face50]
  sketch-geometry (2):
    g0: Circle CenterX=-23 CenterY=20 CenterZ=0 NormalX=0 NormalY=0 NormalZ=1 Radius=3
    g1: Circle CenterX=23 CenterY=20 CenterZ=0 NormalX=0 NormalY=0 NormalZ=1 Radius=3
  constraints (4):
    c: Coincident(g0,g-3)
    c: Radius(g0) = 3
    c: Coincident(g1,g-4)
    c: Radius(g1) = 3
FEATURE [PartDesign::Pocket] Pocket054  label="body_bot_w_nuts"
  Length = 20
  Sketch = -> Sketch107
  Type = 0
